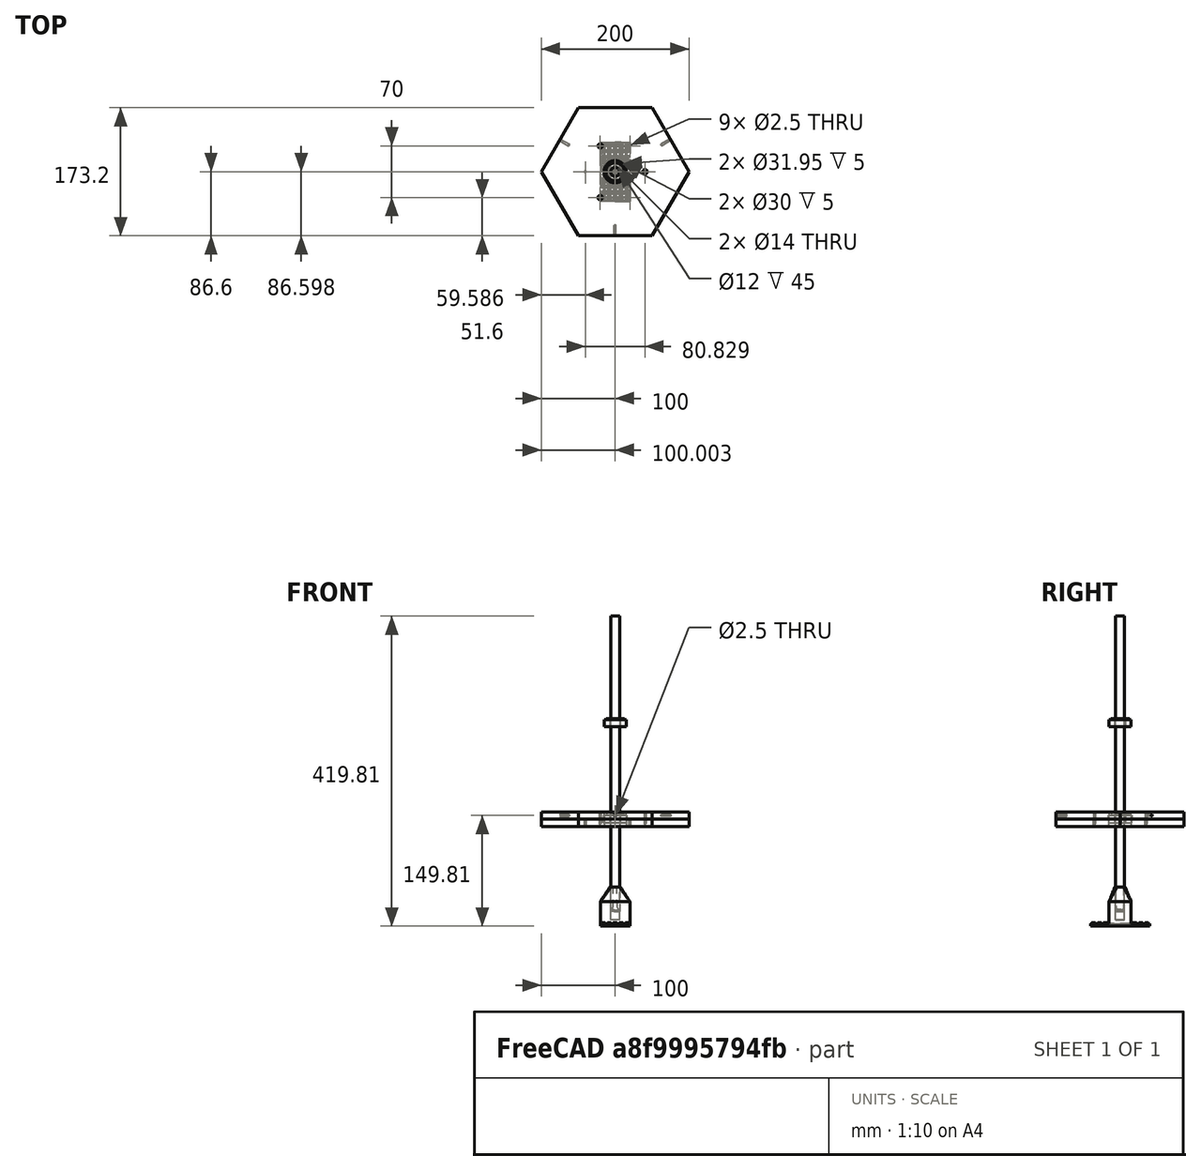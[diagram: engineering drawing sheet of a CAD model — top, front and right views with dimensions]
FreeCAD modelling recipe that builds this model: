
FCSTD DOCUMENT  (FreeCAD 0.20R29177 +426 (Git))
Label: assembly4
License: All rights reserved
LicenseURL: http://en.wikipedia.org/wiki/All_rights_reserved
objects: App::Link×35, Part::Feature×10, App::DocumentObjectGroup×5, App::Part×2, PartDesign::CoordinateSystem×1, App::FeaturePython×1, Part::MultiCommon×1
note: 12 computed .brp shape members not serialized (recipe doc carries the construction recipe); baked Part::Feature solids carry a one-line shape summary decoded from their .brp
EXTERNAL_REF file=lowershaftHolder.FCStd obj=LCS_1
EXTERNAL_REF file=lowershaftHolder.FCStd obj=Body
EXTERNAL_REF file=Main_Rod.FCStd obj=LCS_1
EXTERNAL_REF file=Main_Rod.FCStd obj=Body007
EXTERNAL_REF file=BearingRotator.FCStd obj=RotatorPosition
EXTERNAL_REF file=Main_Rod.FCStd obj=LCS_mid
EXTERNAL_REF file=BearingRotator.FCStd obj=Body
EXTERNAL_REF file=BearingRotator.FCStd obj=RotatorLCS
EXTERNAL_REF file=6201ZZ002_Bearing.FCStd obj=LCS_1
EXTERNAL_REF file=6201ZZ002_Bearing.FCStd obj=Body
EXTERNAL_REF file=Main_Rod.FCStd obj=LCS_mid_upper
EXTERNAL_REF file=mid_hexagon_cmmon_w_side_holes.FCStd obj=LCS_1
EXTERNAL_REF file=mid_hexagon_cmmon_w_side_holes.FCStd obj=Body019
EXTERNAL_REF file=6201ZZ002_Bearing.FCStd obj=bottom_LCS
EXTERNAL_REF file=mid_hexagon_cmmon.FCStd obj=LCS_1
EXTERNAL_REF file=mid_hexagon_cmmon.FCStd obj=Body002
EXTERNAL_REF file=classifier_middle_verPartial3.FCStd obj=LCS_1
EXTERNAL_REF file=mid_hexagon_cmmon_w_side_holes.FCStd obj=LCS_2
EXTERNAL_REF file=classifier_middle_verPartial3.FCStd obj=Body
EXTERNAL_REF file=mid_hexagon_cmmon_w_side_holes.FCStd obj=LCS_3
EXTERNAL_REF file=mid_hexagon_cmmon_w_side_holes.FCStd obj=LCS_4
EXTERNAL_REF file=classifier_middle_verPartial3.FCStd obj=LCS_3
EXTERNAL_REF file=classifier_part.FCStd obj=LCS_1
EXTERNAL_REF file=classifier_part.FCStd obj=Body
EXTERNAL_REF file=classifier_middle_verPartial3.FCStd obj=LCS_2
EXTERNAL_REF file=ImageRecogBox.FCStd obj=LCS_forRod
EXTERNAL_REF file=Main_Rod.FCStd obj=LCS_ImageRecogBox
EXTERNAL_REF file=ImageRecogBox.FCStd obj=Body
EXTERNAL_REF file=ImageRecogBox.FCStd obj=LCS_1
EXTERNAL_REF file=MG90S_servo_refined.FCStd obj=LCS_1
EXTERNAL_REF file=MG90S_servo_refined.FCStd obj=Body
EXTERNAL_REF file=ImageRecogBox.FCStd obj=LCS_cam
EXTERNAL_REF file=esp32camMountRefined.FCStd obj=LCS_1
EXTERNAL_REF file=esp32camMountRefined.FCStd obj=Body
EXTERNAL_REF file=MG90S_servo_refined.FCStd obj=LCS_2
EXTERNAL_REF file=PortalRotatorSketch.FCStd obj=LCS_Origin
EXTERNAL_REF file=PortalRotatorSketch.FCStd obj=PortalRotatorBody
EXTERNAL_REF file=PortalRotatorSketch.FCStd obj=LCSRotator
EXTERNAL_REF file=refinedHorn.FCStd obj=LCS_1
EXTERNAL_REF file=refinedHorn.FCStd obj=Body
EXTERNAL_REF file=hornHexagonModified.FCStd obj=hexagonPlacement
EXTERNAL_REF file=refinedHorn.FCStd obj=hexagonPlacement_LCS
EXTERNAL_REF file=hornHexagonModified.FCStd obj=Body
EXTERNAL_REF file=gear66.FCStd obj=LCS_1
EXTERNAL_REF file=mid_hexagon_cmmon.FCStd obj=LCS_bottom
EXTERNAL_REF file=gear66.FCStd obj=Body003
EXTERNAL_REF file=belt.FCStd obj=LCS_gear66
EXTERNAL_REF file=gear66.FCStd obj=LCS_belt
EXTERNAL_REF file=belt.FCStd obj=Body
EXTERNAL_REF file=belt.FCStd obj=LCS_gear60
EXTERNAL_REF file=gear60_upper.FCStd obj=LCS_belt
EXTERNAL_REF file=gear60_upper.FCStd obj=Body006
EXTERNAL_REF file=gear60_lower.FCStd obj=LCS_1
EXTERNAL_REF file=gear60_upper.FCStd obj=LCS_for_gear60lower
EXTERNAL_REF file=gear60_lower.FCStd obj=Body004
EXTERNAL_REF file=gear60_lower.FCStd obj=LCS_Belt
EXTERNAL_REF file=smallerBelt.FCStd obj=LCS_gear60
EXTERNAL_REF file=smallerBelt.FCStd obj=Body
EXTERNAL_REF file=gear20.FCStd obj=LCS_belt
EXTERNAL_REF file=smallerBelt.FCStd obj=LCS_gear20
EXTERNAL_REF file=gear20.FCStd obj=Body005
EXTERNAL_REF file=17HS4401S_stepper_motor.FCStd obj=LCS_shaft
EXTERNAL_REF file=gear20.FCStd obj=LCS_shaftStepper
EXTERNAL_REF file=17HS4401S_stepper_motor.FCStd obj=Part
EXTERNAL_REF file=17HS4401S_stepper_motor.FCStd obj=LCS_forStand
EXTERNAL_REF file=stepperMotorStand.FCStd obj=LCS_forStepper
EXTERNAL_REF file=stepperMotorStand.FCStd obj=Body
EXTERNAL_REF file=FallAnim.FCStd obj=LCS_Origin
EXTERNAL_REF file=ImageRecogBox.FCStd obj=LCS_fall
EXTERNAL_REF file=FallAnim.FCStd obj=fallSketchBody
EXTERNAL_REF file=FallAnim.FCStd obj=LCS_fallhandler
EXTERNAL_REF file=banana.FCStd obj=LCS_1
EXTERNAL_REF file=banana.FCStd obj=Body

FEATURE [App::DocumentObjectGroup] Parts
FEATURE [PartDesign::CoordinateSystem] LCS_Origin
  AttacherType = Attacher::AttachEngine3D
  MapMode = 2
  Support = -> [X_Axis]
FEATURE [App::DocumentObjectGroup] Constraints
FEATURE [App::FeaturePython] Variables  # WARN: FeaturePython — macro-defined, semantics opaque (R4)
  BearingRotatorVar = -120
  FallHandlerVar = 900
  PortalRotatorDeg = -70
  Type = App::PropertyContainer
FEATURE [App::DocumentObjectGroup] Configurations
FEATURE [App::Link] Body
  AttachedBy = #LCS_1
  AttachedTo = Parent Assembly#LCS_Origin
  AttachmentOffset = pos=(0,0,0) rot=(0.57735,0.57735,0.57735;2.0944rad)
  LinkPlacement = pos=(18.0427,39.9807,-19.8007) rot=(0.109739,0.239494,-0.964676;0.001284rad)
  LinkedObject = -> <external lowershaftHolder.FCStd>#Body
  Placement = pos=(18.0427,39.9807,-19.8007) rot=(0.109739,0.239494,-0.964676;0.001284rad)
  SolverId = Asm4EE
  expr: Placement = LCS_Origin.Placement * AttachmentOffset * lowershaftHolder#LCS_1.Placement ^ -1
FEATURE [App::Link] Rod
  AttachedBy = #LCS_1
  AttachedTo = Parent Assembly#LCS_Origin
  LinkPlacement = pos=(-9e-16,4e-16,400) rot=(0,0,1;0rad)
  LinkedObject = -> <external Main_Rod.FCStd>#Body007
  Placement = pos=(-9e-16,4e-16,400) rot=(0,0,1;0rad)
  SolverId = Asm4EE
  expr: Placement = LCS_Origin.Placement * AttachmentOffset * Main_Rod#LCS_1.Placement ^ -1
FEATURE [App::Link] RotatorBody
  AttachedBy = #RotatorPosition
  AttachedTo = Rod#LCS_mid
  LinkPlacement = pos=(2.7e-15,-1e-15,130) rot=(0,0,1;0rad)
  LinkedObject = -> <external BearingRotator.FCStd>#Body
  Placement = pos=(2.7e-15,-1e-15,130) rot=(0,0,1;0rad)
  SolverId = Asm4EE
  expr: Placement = Rod.Placement * Main_Rod#LCS_mid.Placement * AttachmentOffset * BearingRotator#RotatorPosition.Placement ^ -1
FEATURE [App::Link] Fake_bearing
  AttachedBy = #LCS_1
  AttachedTo = RotatorBody#RotatorLCS
  AttachmentOffset = pos=(0,0,0) rot=(1,0,0;4.71239rad)
  LinkPlacement = pos=(-3.4e-15,1.7e-15,120) rot=(0,0,-1;3.66519rad)
  LinkedObject = -> <external 6201ZZ002_Bearing.FCStd>#Body
  Placement = pos=(-3.4e-15,1.7e-15,120) rot=(0,0,-1;3.66519rad)
  SolverId = Asm4EE
  expr: Placement = RotatorBody.Placement * BearingRotator#RotatorLCS.Placement * AttachmentOffset * _201ZZ002_Bearing#LCS_1.Placement ^ -1
FEATURE [App::Link] RotatorBody001
  AttachedBy = #RotatorPosition
  AttachedTo = Rod#LCS_mid_upper
  LinkPlacement = pos=(2.7e-15,-1e-15,260) rot=(0,0,1;0rad)
  LinkedObject = -> <external BearingRotator.FCStd>#Body
  Placement = pos=(2.7e-15,-1e-15,260) rot=(0,0,1;0rad)
  SolverId = Asm4EE
  expr: Placement = Rod.Placement * Main_Rod#LCS_mid_upper.Placement * AttachmentOffset * BearingRotator#RotatorPosition.Placement ^ -1
FEATURE [App::Link] Fake_bearing001
  AttachedBy = #LCS_1
  AttachedTo = RotatorBody001#RotatorLCS
  AttachmentOffset = pos=(0,0,0) rot=(1,0,0;4.71239rad)
  LinkPlacement = pos=(-3.4e-15,1.7e-15,250) rot=(0,0,-1;3.66519rad)
  LinkedObject = -> <external 6201ZZ002_Bearing.FCStd>#Body
  Placement = pos=(-3.4e-15,1.7e-15,250) rot=(0,0,-1;3.66519rad)
  SolverId = Asm4EE
  expr: Placement = RotatorBody001.Placement * BearingRotator#RotatorLCS.Placement * AttachmentOffset * _201ZZ002_Bearing#LCS_1.Placement ^ -1
FEATURE [App::Link] Rod001
  AttachedBy = #LCS_1
  AttachedTo = Fake_bearing#LCS_1
  AttachmentOffset = pos=(0,0,0) rot=(1,0,0;1.5708rad)
  LinkPlacement = pos=(2.9e-15,-1.4e-15,125) rot=(0,0,-1;3.66519rad)
  LinkedObject = -> <external mid_hexagon_cmmon_w_side_holes.FCStd>#Body019
  Placement = pos=(2.9e-15,-1.4e-15,125) rot=(0,0,-1;3.66519rad)
  SolverId = Asm4EE
  expr: Placement = Fake_bearing.Placement * _201ZZ002_Bearing#LCS_1.Placement * AttachmentOffset * mid_hexagon_cmmon_w_side_holes#LCS_1.Placement ^ -1
FEATURE [App::Link] mid_hexagon
  AttachedBy = #LCS_1
  AttachedTo = Fake_bearing#bottom_LCS
  AttachmentOffset = pos=(0,0,0) rot=(1,0,0;4.71239rad)
  LinkPlacement = pos=(-3.7e-15,1.5e-15,125) rot=(-0.258819,-0.965926,0;3.14159rad)
  LinkedObject = -> <external mid_hexagon_cmmon.FCStd>#Body002
  Placement = pos=(-3.7e-15,1.5e-15,125) rot=(-0.258819,-0.965926,0;3.14159rad)
  SolverId = Asm4EE
  expr: Placement = Fake_bearing.Placement * _201ZZ002_Bearing#bottom_LCS.Placement * AttachmentOffset * mid_hexagon_cmmon#LCS_1.Placement ^ -1
FEATURE [App::Link] mid_hexagon_w_holes
  AttachedBy = #LCS_1
  AttachedTo = Fake_bearing001#LCS_1
  AttachmentOffset = pos=(0,0,0) rot=(1,0,0;1.5708rad)
  LinkPlacement = pos=(2.9e-15,-1.4e-15,255) rot=(0,0,-1;3.66519rad)
  LinkedObject = -> <external mid_hexagon_cmmon_w_side_holes.FCStd>#Body019
  Placement = pos=(2.9e-15,-1.4e-15,255) rot=(0,0,-1;3.66519rad)
  SolverId = Asm4EE
  expr: Placement = Fake_bearing001.Placement * _201ZZ002_Bearing#LCS_1.Placement * AttachmentOffset * mid_hexagon_cmmon_w_side_holes#LCS_1.Placement ^ -1
FEATURE [App::Link] mid_hexagon001
  AttachedBy = #LCS_1
  AttachedTo = Fake_bearing001#bottom_LCS
  AttachmentOffset = pos=(0,0,0) rot=(1,0,0;4.71239rad)
  LinkPlacement = pos=(-3.7e-15,1.5e-15,255) rot=(-0.258819,-0.965926,0;3.14159rad)
  LinkedObject = -> <external mid_hexagon_cmmon.FCStd>#Body002
  Placement = pos=(-3.7e-15,1.5e-15,255) rot=(-0.258819,-0.965926,0;3.14159rad)
  SolverId = Asm4EE
  expr: Placement = Fake_bearing001.Placement * _201ZZ002_Bearing#bottom_LCS.Placement * AttachmentOffset * mid_hexagon_cmmon#LCS_1.Placement ^ -1
FEATURE [Part::Feature] Body001
  Placement = pos=(18.0427,39.9807,-19.8007) rot=(0.109739,0.239494,-0.964676;0.001284rad)
  shape: bbox 40.09 x 80.05 x 53.21 mm, 12357 faces (baked)
FEATURE [Part::Feature] Rod002
  Placement = pos=(-1e-15,0,400) rot=(0,0,1;0rad)
  shape: bbox 25 x 25 x 400 mm, 11 faces (baked)
FEATURE [Part::Feature] Body002
  Placement = pos=(18.0427,39.9807,-19.8007) rot=(0.109739,0.239494,-0.964676;0.001284rad)
  shape: bbox 40.09 x 80.05 x 53.21 mm, 12357 faces (baked)
FEATURE [Part::Feature] Rod003
  Placement = pos=(-1e-15,0,400) rot=(0,0,1;0rad)
  shape: bbox 25 x 25 x 400 mm, 11 faces (baked)
FEATURE [Part::MultiCommon] Common  label="Common 1 - 1 - Body002 - Rod003"
  Shapes = -> [Body002,Rod003]
FEATURE [App::DocumentObjectGroup] Intersections
  Group = -> [Common]
FEATURE [Part::Feature] RotatorBody002
FEATURE [Part::Feature] Fake_bearing002
  Placement = pos=(2e-15,-8e-15,120) rot=(0,0,-1;1.5708rad)
  shape: bbox 30 x 30 x 10 mm, 4 faces (baked)
FEATURE [Part::Feature] RotatorBody001001
FEATURE [Part::Feature] Fake_bearing001001
  Placement = pos=(2e-15,-8e-15,250) rot=(0,0,-1;1.5708rad)
  shape: bbox 30 x 30 x 10 mm, 4 faces (baked)
FEATURE [Part::Feature] Rod001001
  Placement = pos=(3e-15,-1e-15,125) rot=(0,0,-1;1.5708rad)
  shape: bbox 200 x 173.2 x 10 mm, 23 faces (baked)
FEATURE [Part::Feature] mid_hexagon002
  Placement = pos=(3e-15,-8e-15,125) rot=(0.707107,-0.707107,0;3.14159rad)
  shape: bbox 200 x 173.2 x 10 mm, 20 faces (baked)
FEATURE [App::Part] Assembly_copy
  Group = -> [Body001,Rod002,RotatorBody002,Fake_bearing002,RotatorBody001001,Fake_bearing001001,Rod001001,mid_hexagon002]
  Origin = -> Origin001
FEATURE [App::DocumentObjectGroup] Interferences
  Group = -> [Assembly_copy,Intersections]
FEATURE [App::Link] MiddlePartialBody
  AttachedBy = #LCS_1
  AttachedTo = mid_hexagon_w_holes#LCS_2
  LinkPlacement = pos=(-25,43.3013,115) rot=(0,0,-1;5.75959rad)
  LinkedObject = -> <external classifier_middle_verPartial3.FCStd>#Body
  Placement = pos=(-25,43.3013,115) rot=(0,0,-1;5.75959rad)
  SolverId = Asm4EE
  expr: Placement = mid_hexagon_w_holes.Placement * mid_hexagon_cmmon_w_side_holes#LCS_2.Placement * AttachmentOffset * classifier_middle_verPartial3#LCS_1.Placement ^ -1
FEATURE [App::Link] MiddlePartialBody001
  AttachedBy = #LCS_1
  AttachedTo = mid_hexagon_w_holes#LCS_3
  LinkPlacement = pos=(-25,-43.3013,115) rot=(0,0,-1;3.66519rad)
  LinkedObject = -> <external classifier_middle_verPartial3.FCStd>#Body
  Placement = pos=(-25,-43.3013,115) rot=(0,0,-1;3.66519rad)
  SolverId = Asm4EE
  expr: Placement = mid_hexagon_w_holes.Placement * mid_hexagon_cmmon_w_side_holes#LCS_3.Placement * AttachmentOffset * classifier_middle_verPartial3#LCS_1.Placement ^ -1
FEATURE [App::Link] MiddlePartialBody002
  AttachedBy = #LCS_1
  AttachedTo = mid_hexagon_w_holes#LCS_4
  LinkPlacement = pos=(50,2e-16,115) rot=(0,0,1;4.71239rad)
  LinkedObject = -> <external classifier_middle_verPartial3.FCStd>#Body
  Placement = pos=(50,2e-16,115) rot=(0,0,1;4.71239rad)
  SolverId = Asm4EE
  expr: Placement = mid_hexagon_w_holes.Placement * mid_hexagon_cmmon_w_side_holes#LCS_4.Placement * AttachmentOffset * classifier_middle_verPartial3#LCS_1.Placement ^ -1
FEATURE [App::Link] ClassifierPartBody
  AttachedBy = #LCS_1
  AttachedTo = MiddlePartialBody002#LCS_3
  LinkPlacement = pos=(154.11,87.477,120) rot=(0,0,1;3.6566rad)
  LinkedObject = -> <external classifier_part.FCStd>#Body
  Placement = pos=(154.11,87.477,120) rot=(0,0,1;3.6566rad)
  SolverId = Asm4EE
  expr: Placement = MiddlePartialBody002.Placement * classifier_middle_verPartial3#LCS_3.Placement * AttachmentOffset * classifier_part#LCS_1.Placement ^ -1
FEATURE [App::Link] ClassifierPartBody001
  AttachedBy = #LCS_1
  AttachedTo = MiddlePartialBody001#LCS_3
  LinkPlacement = pos=(-1.29784,-177.202,120) rot=(0,0,-1;4.72098rad)
  LinkedObject = -> <external classifier_part.FCStd>#Body
  Placement = pos=(-1.29784,-177.202,120) rot=(0,0,-1;4.72098rad)
  SolverId = Asm4EE
  expr: Placement = MiddlePartialBody001.Placement * classifier_middle_verPartial3#LCS_3.Placement * AttachmentOffset * classifier_part#LCS_1.Placement ^ -1
FEATURE [App::Link] ClassifierPartBody002
  AttachedBy = #LCS_1
  AttachedTo = MiddlePartialBody#LCS_3
  LinkPlacement = pos=(-152.813,89.725,120) rot=(0,0,1;5.75099rad)
  LinkedObject = -> <external classifier_part.FCStd>#Body
  Placement = pos=(-152.813,89.725,120) rot=(0,0,1;5.75099rad)
  SolverId = Asm4EE
  expr: Placement = MiddlePartialBody.Placement * classifier_middle_verPartial3#LCS_3.Placement * AttachmentOffset * classifier_part#LCS_1.Placement ^ -1
FEATURE [App::Link] ClassifierPartBody003
  AttachedBy = #LCS_1
  AttachedTo = MiddlePartialBody001#LCS_2
  LinkPlacement = pos=(-153.088,-89.7186,120) rot=(0,0,-1;5.75959rad)
  LinkedObject = -> <external classifier_part.FCStd>#Body
  Placement = pos=(-153.088,-89.7186,120) rot=(0,0,-1;5.75959rad)
  SolverId = Asm4EE
  expr: Placement = MiddlePartialBody001.Placement * classifier_middle_verPartial3#LCS_2.Placement * AttachmentOffset * classifier_part#LCS_1.Placement ^ -1
FEATURE [App::Link] ClassifierPartBody004
  AttachedBy = #LCS_1
  AttachedTo = MiddlePartialBody002#LCS_2
  LinkPlacement = pos=(154.242,-87.7186,120) rot=(0,0,1;2.61799rad)
  LinkedObject = -> <external classifier_part.FCStd>#Body
  Placement = pos=(154.242,-87.7186,120) rot=(0,0,1;2.61799rad)
  SolverId = Asm4EE
  expr: Placement = MiddlePartialBody002.Placement * classifier_middle_verPartial3#LCS_2.Placement * AttachmentOffset * classifier_part#LCS_1.Placement ^ -1
FEATURE [App::Link] ClassifierPartBody005
  AttachedBy = #LCS_1
  AttachedTo = MiddlePartialBody#LCS_2
  LinkPlacement = pos=(-1.1547,177.437,120) rot=(0,0,1;4.71239rad)
  LinkedObject = -> <external classifier_part.FCStd>#Body
  Placement = pos=(-1.1547,177.437,120) rot=(0,0,1;4.71239rad)
  SolverId = Asm4EE
  expr: Placement = MiddlePartialBody.Placement * classifier_middle_verPartial3#LCS_2.Placement * AttachmentOffset * classifier_part#LCS_1.Placement ^ -1
FEATURE [App::Link] ImageRecogBox_body  label="ImageRecogBox-body"
  AttachedBy = #LCS_forRod
  AttachedTo = Rod#LCS_ImageRecogBox
  LinkPlacement = pos=(-0.00816561,-167.469,384) rot=(0,0,-1;0.523648rad)
  LinkedObject = -> <external ImageRecogBox.FCStd>#Body
  Placement = pos=(-0.00816561,-167.469,384) rot=(0,0,-1;0.523648rad)
  SolverId = Asm4EE
  expr: Placement = Rod.Placement * Main_Rod#LCS_ImageRecogBox.Placement * AttachmentOffset * ImageRecogBox#LCS_forRod.Placement ^ -1
FEATURE [App::Link] Body003
  AttachedBy = #LCS_1
  AttachedTo = ImageRecogBox_body#LCS_1
  AttachmentOffset = pos=(0,0,0) rot=(0.57735,0.57735,0.57735;2.0944rad)
  LinkPlacement = pos=(-1546.53,182.702,-393.809) rot=(0.774614,0.447198,0.447198;1.82346rad)
  LinkedObject = -> <external MG90S_servo_refined.FCStd>#Body
  Placement = pos=(-1546.53,182.702,-393.809) rot=(0.774614,0.447198,0.447198;1.82346rad)
  SolverId = Asm4EE
  expr: Placement = ImageRecogBox_body.Placement * ImageRecogBox#LCS_1.Placement * AttachmentOffset * MG90S_servo_refined#LCS_1.Placement ^ -1
FEATURE [App::Link] mountBody
  AttachedBy = #LCS_1
  AttachedTo = ImageRecogBox_body#LCS_cam
  LinkPlacement = pos=(3.98719,-262.811,482.589) rot=(-2e-06,-0.087156,-0.996195;3.14164rad)
  LinkedObject = -> <external esp32camMountRefined.FCStd>#Body
  Placement = pos=(3.98719,-262.811,482.589) rot=(-2e-06,-0.087156,-0.996195;3.14164rad)
  SolverId = Asm4EE
  expr: Placement = ImageRecogBox_body.Placement * ImageRecogBox#LCS_cam.Placement * AttachmentOffset * esp32camMountRefined#LCS_1.Placement ^ -1
FEATURE [App::Link] PortalRotatorBody
  AttachedBy = #LCS_Origin
  AttachedTo = Body003#LCS_2
  LinkPlacement = pos=(58.8831,-230.669,373.4) rot=(0,0,1;1.04715rad)
  LinkedObject = -> <external PortalRotatorSketch.FCStd>#PortalRotatorBody
  Placement = pos=(58.8831,-230.669,373.4) rot=(0,0,1;1.04715rad)
  SolverId = Asm4EE
  expr: Placement = Body003.Placement * MG90S_servo_refined#LCS_2.Placement * AttachmentOffset * PortalRotatorSketch#LCS_Origin.Placement ^ -1
FEATURE [App::Link] HornBody
  AttachedBy = #LCS_1
  AttachedTo = PortalRotatorBody#LCSRotator
  AttachmentOffset = pos=(0,0,0) rot=(1,0,0;4.71239rad)
  LinkPlacement = pos=(-154.381,-489.726,375.091) rot=(-0.893584,0.448895,0;3.14159rad)
  LinkedObject = -> <external refinedHorn.FCStd>#Body
  Placement = pos=(-154.381,-489.726,375.091) rot=(-0.893584,0.448895,0;3.14159rad)
  SolverId = Asm4EE
  expr: Placement = PortalRotatorBody.Placement * PortalRotatorSketch#LCSRotator.Placement * AttachmentOffset * refinedHorn#LCS_1.Placement ^ -1
FEATURE [App::Link] hornHexagonBody
  AttachedBy = #hexagonPlacement
  AttachedTo = HornBody#hexagonPlacement_LCS
  LinkPlacement = pos=(29.3352,-148.735,372.089) rot=(0,0,1;5.33754rad)
  LinkedObject = -> <external hornHexagonModified.FCStd>#Body
  Placement = pos=(29.3352,-148.735,372.089) rot=(0,0,1;5.33754rad)
  SolverId = Asm4EE
  expr: Placement = HornBody.Placement * refinedHorn#hexagonPlacement_LCS.Placement * AttachmentOffset * hornHexagonModified#hexagonPlacement.Placement ^ -1
FEATURE [App::Link] gear66Body
  AttachedBy = #LCS_1
  AttachedTo = mid_hexagon#LCS_bottom
  LinkPlacement = pos=(-5.9e-15,1.6e-14,88.5) rot=(0,0,1;2.61799rad)
  LinkedObject = -> <external gear66.FCStd>#Body003
  Placement = pos=(-5.9e-15,1.6e-14,88.5) rot=(0,0,1;2.61799rad)
  SolverId = Asm4EE
  expr: Placement = mid_hexagon.Placement * mid_hexagon_cmmon#LCS_bottom.Placement * AttachmentOffset * gear66#LCS_1.Placement ^ -1
FEATURE [App::Link] belt_Body
  AttachedBy = #LCS_gear66
  AttachedTo = gear66Body#LCS_belt
  AttachmentOffset = pos=(0,0,0) rot=(1,0,0;1.5708rad)
  LinkPlacement = pos=(15.0572,27.5548,87.5) rot=(0,0,1;1.07069rad)
  LinkedObject = -> <external belt.FCStd>#Body
  Placement = pos=(15.0572,27.5548,87.5) rot=(0,0,1;1.07069rad)
  SolverId = Asm4EE
  expr: Placement = gear66Body.Placement * gear66#LCS_belt.Placement * AttachmentOffset * belt#LCS_gear66.Placement ^ -1
FEATURE [App::Link] gear60_upperBody
  AttachedBy = #LCS_belt
  AttachedTo = belt_Body#LCS_gear60
  AttachmentOffset = pos=(0,0,0) rot=(1,0,0;4.71239rad)
  LinkPlacement = pos=(40.8358,74.7297,87.5) rot=(0,0,1;5.80656rad)
  LinkedObject = -> <external gear60_upper.FCStd>#Body006
  Placement = pos=(40.8358,74.7297,87.5) rot=(0,0,1;5.80656rad)
  SolverId = Asm4EE
  expr: Placement = belt_Body.Placement * belt#LCS_gear60.Placement * AttachmentOffset * gear60_upper#LCS_belt.Placement ^ -1
FEATURE [App::Link] gear60_lower_body
  AttachedBy = #LCS_1
  AttachedTo = gear60_upperBody#LCS_for_gear60lower
  LinkPlacement = pos=(40.8358,74.7297,76) rot=(0,0,1;5.80656rad)
  LinkedObject = -> <external gear60_lower.FCStd>#Body004
  Placement = pos=(40.8358,74.7297,76) rot=(0,0,1;5.80656rad)
  SolverId = Asm4EE
  expr: Placement = gear60_upperBody.Placement * gear60_upper#LCS_for_gear60lower.Placement * AttachmentOffset * gear60_lower#LCS_1.Placement ^ -1
FEATURE [App::Link] smallerBelt_Body
  AttachedBy = #LCS_gear60
  AttachedTo = gear60_lower_body#LCS_Belt
  LinkPlacement = pos=(-5.71516,89.0849,76) rot=(0,0,1;2.84247rad)
  LinkedObject = -> <external smallerBelt.FCStd>#Body
  Placement = pos=(-5.71516,89.0849,76) rot=(0,0,1;2.84247rad)
  SolverId = Asm4EE
  expr: Placement = gear60_lower_body.Placement * gear60_lower#LCS_Belt.Placement * AttachmentOffset * smallerBelt#LCS_gear60.Placement ^ -1
FEATURE [App::Link] gear20_body
  AttachedBy = #LCS_belt
  AttachedTo = smallerBelt_Body#LCS_gear20
  LinkPlacement = pos=(-32.2262,97.2603,76) rot=(0,0,1;3.01997rad)
  LinkedObject = -> <external gear20.FCStd>#Body005
  Placement = pos=(-32.2262,97.2603,76) rot=(0,0,1;3.01997rad)
  SolverId = Asm4EE
  expr: Placement = smallerBelt_Body.Placement * smallerBelt#LCS_gear20.Placement * AttachmentOffset * gear20#LCS_belt.Placement ^ -1
FEATURE [App::Link] _7HS4401S_Stepper_Motor  label="17HS4401S Stepper Motor"
  AttachedBy = #LCS_shaft
  AttachedTo = gear20_body#LCS_shaftStepper
  LinkPlacement = pos=(-68.0048,-76.3424,26.5) rot=(0,0,1;1.05307rad)
  LinkedObject = -> <external 17HS4401S_stepper_motor.FCStd>#Part
  Placement = pos=(-68.0048,-76.3424,26.5) rot=(0,0,1;1.05307rad)
  SolverId = Asm4EE
  expr: Placement = gear20_body.Placement * gear20#LCS_shaftStepper.Placement * AttachmentOffset * _7HS4401S_stepper_motor#LCS_shaft.Placement ^ -1
FEATURE [App::Link] stand_Body
  AttachedBy = #LCS_forStepper
  AttachedTo = _7HS4401S_Stepper_Motor#LCS_forStand
  AttachmentOffset = pos=(0,0,0) rot=(0,0,1;1.5708rad)
  LinkPlacement = pos=(-36.9523,-21.8204,-19.8) rot=(0,0,1;3.14747rad)
  LinkedObject = -> <external stepperMotorStand.FCStd>#Body
  Placement = pos=(-36.9523,-21.8204,-19.8) rot=(0,0,1;3.14747rad)
  SolverId = Asm4EE
  expr: Placement = _7HS4401S_Stepper_Motor.Placement * _7HS4401S_stepper_motor#LCS_forStand.Placement * AttachmentOffset * stepperMotorStand#LCS_forStepper.Placement ^ -1
FEATURE [App::Link] fallSketchBody
  AttachedBy = #LCS_Origin
  AttachedTo = ImageRecogBox_body#LCS_fall
  AttachmentOffset = pos=(0,0,0) rot=(0.57735,-0.57735,-0.57735;4.18879rad)
  LinkPlacement = pos=(-0.00912142,-187.071,984) rot=(0,0,-1;3.14164rad)
  LinkedObject = -> <external FallAnim.FCStd>#fallSketchBody
  Placement = pos=(-0.00912142,-187.071,984) rot=(0,0,-1;3.14164rad)
  SolverId = Asm4EE
  expr: Placement = ImageRecogBox_body.Placement * ImageRecogBox#LCS_fall.Placement * AttachmentOffset * FallAnim#LCS_Origin.Placement ^ -1
FEATURE [App::Link] Banana_Body
  AttachedBy = #LCS_1
  AttachedTo = fallSketchBody#LCS_fallhandler
  LinkPlacement = pos=(-0.00912142,-187.071,84) rot=(0,0,-1;3.14164rad)
  LinkedObject = -> <external banana.FCStd>#Body
  Placement = pos=(-0.00912142,-187.071,84) rot=(0,0,-1;3.14164rad)
  SolverId = Asm4EE
  expr: Placement = fallSketchBody.Placement * FallAnim#LCS_fallhandler.Placement * AttachmentOffset * banana#LCS_1.Placement ^ -1
FEATURE [App::Part] Assembly
  AssemblyType = Part::Link
  Group = -> [LCS_Origin,Constraints,Variables,Configurations,Body,Rod,RotatorBody,Fake_bearing,RotatorBody001,Fake_bearing001,Rod001,mid_hexagon,mid_hexagon_w_holes,mid_hexagon001,MiddlePartialBody,MiddlePartialBody001,MiddlePartialBody002,ClassifierPartBody,ClassifierPartBody001,ClassifierPartBody002,ClassifierPartBody003,ClassifierPartBody004,ClassifierPartBody005,ImageRecogBox_body,Body003,mountBody,+13 more]
  Origin = -> Origin
  Type = Assembly

RESOLVED EXTERNAL PARTS (link-assembly join: the EXTERNAL_REF files above that resolve inside this repo's crawl, each included once):
---- part 17HS4401S_stepper_motor.FCStd = doc fcstd_67801616e878 ----
FCSTD DOCUMENT  (FreeCAD 0.20R29177 +426 (Git))
Label: 17HS4401S_stepper_motor
License: All rights reserved
LicenseURL: http://en.wikipedia.org/wiki/All_rights_reserved
objects: Sketcher::SketchObject×18, PartDesign::Pad×10, PartDesign::Body×7, PartDesign::Pocket×5, PartDesign::Chamfer×4, Part::FeaturePython×4, PartDesign::Fillet×3, PartDesign::Revolution×2, PartDesign::CoordinateSystem×2, PartDesign::LinearPattern×1, App::Part×1
note: 80 computed .brp shape members not serialized (recipe doc carries the construction recipe); baked Part::Feature solids carry a one-line shape summary decoded from their .brp

FEATURE [PartDesign::Body] Body  label="rear end cap"
  Origin = -> Origin
FEATURE [Sketcher::SketchObject] Sketch  label=" rear outline"
  FullyConstrained = true
  MapMode = 5
  Support = -> [XY_Plane]
  sketch-geometry (17):
    g0: ArcOfCircle CenterX=0 CenterY=0 CenterZ=0 NormalX=0 NormalY=0 NormalZ=1 AngleXU=0 Radius=26.8 StartAngle=2.24118 EndAngle=2.47121
    g1: ArcOfCircle CenterX=0 CenterY=0 CenterZ=0 NormalX=0 NormalY=0 NormalZ=1 AngleXU=0 Radius=26.8 StartAngle=5.38277 EndAngle=5.6128
    g2: ArcOfCircle CenterX=0 CenterY=0 CenterZ=0 NormalX=0 NormalY=0 NormalZ=1 AngleXU=0 Radius=26.8 StartAngle=0.670386 EndAngle=0.900411
    g3: ArcOfCircle CenterX=0 CenterY=0 CenterZ=0 NormalX=0 NormalY=0 NormalZ=1 AngleXU=0 Radius=26.8 StartAngle=3.81198 EndAngle=4.042
    g4: LineSegment StartX=-16.6505 StartY=21 StartZ=0 EndX=16.6505 EndY=21 EndZ=0
    g5: LineSegment StartX=21 StartY=16.6505 StartZ=0 EndX=21 EndY=8.3 EndZ=0
    g6: LineSegment StartX=-16.6505 StartY=-21 StartZ=0 EndX=16.6505 EndY=-21 EndZ=0
    g7: LineSegment StartX=-21 StartY=16.6505 StartZ=0 EndX=-21 EndY=-16.6505 EndZ=0
    g8: Circle CenterX=0 CenterY=0 CenterZ=0 NormalX=0 NormalY=0 NormalZ=1 AngleXU=0 Radius=4.5
    g9: Circle CenterX=-15.5 CenterY=15.5 CenterZ=0 NormalX=0 NormalY=0 NormalZ=1 AngleXU=0 Radius=1.5
    g10: Circle CenterX=15.5 CenterY=15.5 CenterZ=0 NormalX=0 NormalY=0 NormalZ=1 AngleXU=0 Radius=1.5
    g11: Circle CenterX=15.5 CenterY=-15.5 CenterZ=0 NormalX=0 NormalY=0 NormalZ=1 AngleXU=0 Radius=1.5
    g12: Circle CenterX=-15.5 CenterY=-15.5 CenterZ=0 NormalX=0 NormalY=0 NormalZ=1 AngleXU=0 Radius=1.5
    g13: LineSegment StartX=21 StartY=8.3 StartZ=0 EndX=25.4 EndY=8.3 EndZ=0
    g14: LineSegment StartX=25.4 StartY=8.3 StartZ=0 EndX=25.4 EndY=-8.3 EndZ=0
    g15: LineSegment StartX=25.4 StartY=-8.3 StartZ=0 EndX=21 EndY=-8.3 EndZ=0
    g16: LineSegment StartX=21 StartY=-8.3 StartZ=0 EndX=21 EndY=-16.6505 EndZ=0
  constraints (50):
    c: Coincident(g0,g-1)
    c: Coincident(g1,g0)
    c: Coincident(g2,g0)
    c: Coincident(g3,g0)
    c: Equal(g0,g1)
    c: Equal(g1,g2)
    c: Equal(g2,g3)
    c: Radius(g0) = 26.8
    c: Coincident(g4,g0)
    c: Coincident(g4,g2)
    c: Horizontal(g4)
    c: Coincident(g5,g2)
    c: Coincident(g16,g1)
    c: Vertical(g5)
    c: Coincident(g6,g3)
    c: Coincident(g6,g1)
    c: Coincident(g7,g0)
    c: Coincident(g7,g3)
    c: Vertical(g7)
    c: Horizontal(g6)
    c: DistanceX(g0,g2) = 42
    c: DistanceY(g1,g2) = 42
    c: DistanceY(g0,g2) = 21
    c: DistanceX(g0,g0) = 21
    c: Coincident(g8,g0)
    c: Diameter(g8) = 9
    c: Vertical(g9,g12)
    c: Vertical(g11,g10)
    c: Horizontal(g9,g10)
    c: Horizontal(g12,g11)
    c: Equal(g9,g10)
    c: Equal(g11,g10)
    c: Equal(g11,g12)
    c: Diameter(g9) = 3
    c: DistanceX(g9,g10) = 31
    c: DistanceY(g11,g10) = 31
    c: DistanceY(g0,g10) = 15.5
    c: DistanceX(g0,g10) = 15.5
    c: Horizontal(g13)
    c: Coincident(g14,g13)
    c: Vertical(g14)
    c: Coincident(g15,g14)
    c: Horizontal(g15)
    c: DistanceY(g14,g14) = 16.6
    c: DistanceY(g0,g13) = 8.3
    c: DistanceX(g13,g13) = 4.4
    c: Coincident(g5,g13)
    c: Coincident(g16,g15)
    c: Vertical(g5,g15)
    c: Vertical(g16)
FEATURE [Sketcher::SketchObject] Sketch001  label="basic outline"
  FullyConstrained = true
  MapMode = 5
  Support = -> [XY_Plane001]
  sketch-geometry (13):
    g0: ArcOfCircle CenterX=0 CenterY=0 CenterZ=0 NormalX=0 NormalY=0 NormalZ=1 AngleXU=0 Radius=26.8 StartAngle=2.24118 EndAngle=2.47121
    g1: ArcOfCircle CenterX=0 CenterY=0 CenterZ=0 NormalX=0 NormalY=0 NormalZ=1 AngleXU=0 Radius=26.8 StartAngle=5.38277 EndAngle=5.6128
    g2: ArcOfCircle CenterX=0 CenterY=0 CenterZ=0 NormalX=0 NormalY=0 NormalZ=1 AngleXU=0 Radius=26.8 StartAngle=0.670386 EndAngle=0.900411
    g3: ArcOfCircle CenterX=0 CenterY=0 CenterZ=0 NormalX=0 NormalY=0 NormalZ=1 AngleXU=0 Radius=26.8 StartAngle=3.81198 EndAngle=4.042
    g4: LineSegment StartX=-16.6505 StartY=21 StartZ=0 EndX=16.6505 EndY=21 EndZ=0
    g5: LineSegment StartX=21 StartY=16.6505 StartZ=0 EndX=21 EndY=-16.6505 EndZ=0
    g6: LineSegment StartX=-16.6505 StartY=-21 StartZ=0 EndX=16.6505 EndY=-21 EndZ=0
    g7: LineSegment StartX=-21 StartY=16.6505 StartZ=0 EndX=-21 EndY=-16.6505 EndZ=0
    g8: Circle CenterX=0 CenterY=0 CenterZ=0 NormalX=0 NormalY=0 NormalZ=1 AngleXU=0 Radius=4.5
    g9: Circle CenterX=-15.5 CenterY=15.5 CenterZ=0 NormalX=0 NormalY=0 NormalZ=1 AngleXU=0 Radius=1.5
    g10: Circle CenterX=15.5 CenterY=15.5 CenterZ=0 NormalX=0 NormalY=0 NormalZ=1 AngleXU=0 Radius=1.5
    g11: Circle CenterX=15.5 CenterY=-15.5 CenterZ=0 NormalX=0 NormalY=0 NormalZ=1 AngleXU=0 Radius=1.5
    g12: Circle CenterX=-15.5 CenterY=-15.5 CenterZ=0 NormalX=0 NormalY=0 NormalZ=1 AngleXU=0 Radius=1.5
  constraints (38):
    c: Coincident(g0,g-1)
    c: Coincident(g1,g0)
    c: Coincident(g2,g0)
    c: Coincident(g3,g0)
    c: Equal(g0,g1)
    c: Equal(g1,g2)
    c: Equal(g2,g3)
    c: Radius(g0) = 26.8
    c: Coincident(g4,g0)
    c: Coincident(g4,g2)
    c: Horizontal(g4)
    c: Coincident(g5,g2)
    c: Coincident(g5,g1)
    c: Vertical(g5)
    c: Coincident(g6,g3)
    c: Coincident(g6,g1)
    c: Coincident(g7,g0)
    c: Coincident(g7,g3)
    c: Vertical(g7)
    c: Horizontal(g6)
    c: DistanceX(g0,g2) = 42
    c: DistanceY(g1,g2) = 42
    c: DistanceY(g0,g2) = 21
    c: DistanceX(g0,g0) = 21
    c: Coincident(g8,g0)
    c: Diameter(g8) = 9
    c: Vertical(g9,g12)
    c: Vertical(g11,g10)
    c: Horizontal(g9,g10)
    c: Horizontal(g12,g11)
    c: Equal(g9,g10)
    c: Equal(g11,g10)
    c: Equal(g11,g12)
    c: Diameter(g9) = 3
    c: DistanceX(g9,g10) = 31
    c: DistanceY(g11,g10) = 31
    c: DistanceY(g0,g10) = 15.5
    c: DistanceX(g0,g10) = 15.5
FEATURE [PartDesign::Pad] Pad
  Direction = (0,0,1)
  Length = 9.4
  Length2 = 10
  Profile = -> Sketch
  ReferenceAxis = -> Sketch [N_Axis]
  Type = 0
FEATURE [Sketcher::SketchObject] Sketch002
  FullyConstrained = true
  MapMode = 5
  Support = -> [XY_Plane]
  sketch-geometry (4):
    g0: Circle CenterX=-15.5 CenterY=15.5 CenterZ=0 NormalX=0 NormalY=0 NormalZ=1 AngleXU=0 Radius=3.2
    g1: Circle CenterX=15.5 CenterY=15.5 CenterZ=0 NormalX=0 NormalY=0 NormalZ=1 AngleXU=0 Radius=3.2
    g2: Circle CenterX=15.5 CenterY=-15.5 CenterZ=0 NormalX=0 NormalY=0 NormalZ=1 AngleXU=0 Radius=3.2
    g3: Circle CenterX=-15.5 CenterY=-15.5 CenterZ=0 NormalX=0 NormalY=0 NormalZ=1 AngleXU=0 Radius=3.2
  constraints (12):
    c: Equal(g0,g1)
    c: Equal(g1,g2)
    c: Equal(g2,g3)
    c: Horizontal(g0,g1)
    c: Horizontal(g3,g2)
    c: Vertical(g1,g2)
    c: Vertical(g0,g3)
    c: Diameter(g0) = 6.4
    c: DistanceY(g2,g1) = 31
    c: DistanceY(g2,g-1) = 15.5
    c: DistanceX(g0,g1) = 31
    c: DistanceX(g-1,g1) = 15.5
FEATURE [PartDesign::Pocket] Pocket  label="screw counterbore"
  BaseFeature = -> Pad
  Direction = (0,0,-1)
  Length = 3
  Length2 = 5
  Profile = -> Sketch002
  ReferenceAxis = -> Sketch002 [N_Axis]
  Reversed = true
  Type = 0
FEATURE [Sketcher::SketchObject] Sketch003
  AttachmentOffset = pos=(0,0,10) rot=(0,0,1;0rad)
  FullyConstrained = true
  MapMode = 5
  Placement = pos=(0,0,10) rot=(0,0,1;0rad)
  Support = -> [XY_Plane]
  sketch-geometry (1):
    g0: Circle CenterX=0 CenterY=0 CenterZ=0 NormalX=0 NormalY=0 NormalZ=1 AngleXU=0 Radius=8
  constraints (2):
    c: Coincident(g0,g-1)
    c: Diameter(g0) = 16
FEATURE [PartDesign::Pocket] Pocket001  label="bearing pocket"
  BaseFeature = -> Pocket
  Direction = (0,0,-1)
  Length = 8
  Length2 = 5
  Profile = -> Sketch003
  ReferenceAxis = -> Sketch003 [N_Axis]
  Type = 0
FEATURE [Sketcher::SketchObject] Sketch004
  AttachmentOffset = pos=(0,0,26) rot=(0,0,1;0rad)
  FullyConstrained = true
  MapMode = 5
  Placement = pos=(26,-5.8e-15,5.8e-15) rot=(0.57735,0.57735,0.57735;2.0944rad)
  Support = -> [YZ_Plane]
  sketch-geometry (4):
    g0: LineSegment StartX=-8.3 StartY=9.4 StartZ=0 EndX=8.3 EndY=9.4 EndZ=0
    g1: LineSegment StartX=8.3 StartY=9.4 StartZ=0 EndX=8.3 EndY=3 EndZ=0
    g2: LineSegment StartX=8.3 StartY=3 StartZ=0 EndX=-8.3 EndY=3 EndZ=0
    g3: LineSegment StartX=-8.3 StartY=3 StartZ=0 EndX=-8.3 EndY=9.4 EndZ=0
  constraints (12):
    c: Coincident(g0,g1)
    c: Coincident(g1,g2)
    c: Coincident(g2,g3)
    c: Coincident(g3,g0)
    c: Horizontal(g0)
    c: Horizontal(g2)
    c: Vertical(g1)
    c: Vertical(g3)
    c: DistanceX(g0,g0) = 16.6
    c: DistanceX(g-1,g0) = 8.3
    c: DistanceY(g-1,g0) = 9.4
    c: DistanceY(g-1,g1) = 3
FEATURE [PartDesign::Pocket] Pocket002
  BaseFeature = -> Pocket
  Direction = (-1,2e-16,-3e-16)
  Length = 10
  Length2 = 5
  Profile = -> Sketch004
  ReferenceAxis = -> Sketch004 [N_Axis]
  Type = 0
FEATURE [Sketcher::SketchObject] Sketch005
  FullyConstrained = true
  MapMode = 5
  Placement = pos=(0,0,0) rot=(1,0,0;1.5708rad)
  Support = -> [XZ_Plane002]
  sketch-geometry (12):
    g0: LineSegment StartX=2.5 StartY=2.55 StartZ=0 EndX=8 EndY=2.55 EndZ=0
    g1: LineSegment StartX=8 StartY=2.55 StartZ=0 EndX=8 EndY=-2.45 EndZ=0
    g2: LineSegment StartX=8 StartY=-2.45 StartZ=0 EndX=6.5 EndY=-2.45 EndZ=0
    g3: LineSegment StartX=2.5 StartY=-2.5 StartZ=0 EndX=2.5 EndY=2.55 EndZ=0
    g4: LineSegment StartX=4.2 StartY=-2.45 StartZ=0 EndX=4.1 EndY=-1.95 EndZ=0
    g5: LineSegment StartX=4.1 StartY=-1.95 StartZ=0 EndX=4 EndY=-2.5 EndZ=0
    g6: LineSegment StartX=5.2 StartY=-2.45 StartZ=0 EndX=6.13734 EndY=-1.97682 EndZ=0
    g7: LineSegment StartX=6.5 StartY=-2.2 StartZ=0 EndX=6.5 EndY=-2.45 EndZ=0
    g8: LineSegment StartX=4 StartY=-2.5 StartZ=0 EndX=2.5 EndY=-2.5 EndZ=0
    g9: LineSegment StartX=5.2 StartY=-2.45 StartZ=0 EndX=4.2 EndY=-2.45 EndZ=0
    g10: ArcOfCircle CenterX=6.25 CenterY=-2.2 CenterZ=0 NormalX=0 NormalY=0 NormalZ=1 AngleXU=0 Radius=0.25 StartAngle=2.03828 EndAngle=6.28319
    g11: LineSegment StartX=6.5 StartY=-2.45 StartZ=0 EndX=5.2 EndY=-2.45 EndZ=0
  constraints (34):
    c: Coincident(g0,g1)
    c: Coincident(g1,g2)
    c: Coincident(g8,g3)
    c: Coincident(g3,g0)
    c: Horizontal(g0)
    c: Horizontal(g2)
    c: Vertical(g1)
    c: Vertical(g3)
    c: Coincident(g5,g4)
    c: DistanceX(g-1,g8) = 2.5
    c: DistanceX(g-1,g1) = 8
    c: DistanceY(g1,g1) = 5
    c: DistanceY(g8,g-1) = 2.5
    c: Coincident(g9,g4)
    c: Coincident(g8,g5)
    c: Coincident(g9,g6)
    c: Coincident(g2,g7)
    c: Horizontal(g9)
    c: Horizontal(g8)
    c: Vertical(g7)
    c: Horizontal(g6,g2)
    c: DistanceX(g5,g4) = 0.2
    c: Coincident(g11,g2)
    c: Coincident(g11,g6)
    c: Diameter(g10) = 0.5
    c: DistanceX(g2,g2) = 1.5
    c: Tangent(g10,g11)
    c: DistanceX(g4,g4) = 0.1
    c: DistanceX(g8,g8) = 1.5
    c: DistanceX(g9,g9) = 1
    c: Tangent(g7,g10) = 1.5708
    c: Tangent(g6,g10) = 1.5708
    c: DistanceY(g4,g4) = 0.5
    c: DistanceY(g5,g4) = 0.05
FEATURE [PartDesign::Revolution] Revolution
  Angle = 360
  Axis = (0,2e-16,1)
  Base = (0,0,0)
  Placement = pos=(0,0,0) rot=(1,0,0;1.5708rad)
  Profile = -> Sketch005
  ReferenceAxis = -> Sketch005 [V_Axis]
  Reversed = true
FEATURE [PartDesign::Chamfer] Chamfer
  Angle = 45
  Base = -> Revolution [Edge11,Edge7]
  BaseFeature = -> Revolution
  ChamferType = 0
  FlipDirection = false
  Placement = pos=(0,0,0) rot=(1,0,0;1.5708rad)
  Size = 0.4
  Size2 = 1
  SupportTransform = false
  UseAllEdges = false
FEATURE [PartDesign::Body] Body001  label="rear bearing"
  Group = -> [Sketch005,Revolution,Chamfer]
  Origin = -> Origin002
  Placement = pos=(0,0,6.6) rot=(0,0,1;0rad)
  Tip = -> Chamfer
FEATURE [Sketcher::SketchObject] Sketch006
  AttachmentOffset = pos=(0,0,16) rot=(0,0,1;0rad)
  FullyConstrained = true
  MapMode = 5
  Placement = pos=(16,-3.6e-15,3.6e-15) rot=(0.57735,0.57735,0.57735;2.0944rad)
  Support = -> [YZ_Plane003]
  sketch-geometry (4):
    g0: LineSegment StartX=-7 StartY=3.8 StartZ=0 EndX=7 EndY=3.8 EndZ=0
    g1: LineSegment StartX=7 StartY=3.8 StartZ=0 EndX=7 EndY=3.2 EndZ=0
    g2: LineSegment StartX=7 StartY=3.2 StartZ=0 EndX=-7 EndY=3.2 EndZ=0
    g3: LineSegment StartX=-7 StartY=3.2 StartZ=0 EndX=-7 EndY=3.8 EndZ=0
  constraints (12):
    c: Coincident(g0,g1)
    c: Coincident(g1,g2)
    c: Coincident(g2,g3)
    c: Coincident(g3,g0)
    c: Horizontal(g0)
    c: Horizontal(g2)
    c: Vertical(g1)
    c: Vertical(g3)
    c: DistanceY(g1,g1) = 0.6
    c: DistanceX(g0,g0) = 14
    c: DistanceX(g-1,g0) = 7
    c: DistanceY(g-1,g1) = 3.2
FEATURE [PartDesign::Pad] Pad001  label="PCB"
  Direction = (1,-2e-16,3e-16)
  Length = 9.6
  Length2 = 10
  Placement = pos=(0,0,0) rot=(0.57735,0.57735,0.57735;2.0944rad)
  Profile = -> Sketch006
  ReferenceAxis = -> Sketch006 [N_Axis]
  Type = 0
FEATURE [Sketcher::SketchObject] Sketch007
  AttachmentOffset = pos=(0,0,16) rot=(0,0,1;0rad)
  FullyConstrained = true
  MapMode = 5
  Placement = pos=(16,-3.6e-15,3.6e-15) rot=(0.57735,0.57735,0.57735;2.0944rad)
  Support = -> [YZ_Plane003]
  sketch-geometry (11):
    g0: LineSegment StartX=7.8 StartY=8.8 StartZ=0 EndX=7.8 EndY=3.8 EndZ=0
    g1: LineSegment StartX=7.8 StartY=3.8 StartZ=0 EndX=0.5 EndY=3.8 EndZ=0
    g2: LineSegment StartX=-7.8 StartY=3.8 StartZ=0 EndX=-7.8 EndY=8.8 EndZ=0
    g3: LineSegment StartX=7.3 StartY=8.8 StartZ=0 EndX=7.3 EndY=4.2 EndZ=0
    g4: LineSegment StartX=7.3 StartY=4.2 StartZ=0 EndX=-7.3 EndY=4.2 EndZ=0
    g5: LineSegment StartX=-7.3 StartY=4.2 StartZ=0 EndX=-7.3 EndY=8.8 EndZ=0
    g6: LineSegment StartX=7.3 StartY=8.8 StartZ=0 EndX=7.8 EndY=8.8 EndZ=0
    g7: LineSegment StartX=-7.3 StartY=8.8 StartZ=0 EndX=-7.8 EndY=8.8 EndZ=0
    g8: LineSegment StartX=-0.5 StartY=3.8 StartZ=0 EndX=1e-16 EndY=3.4 EndZ=0
    g9: LineSegment StartX=0 StartY=3.4 StartZ=0 EndX=0.5 EndY=3.8 EndZ=0
    g10: LineSegment StartX=-0.5 StartY=3.8 StartZ=0 EndX=-7.8 EndY=3.8 EndZ=0
  constraints (33):
    c: Coincident(g0,g1)
    c: Coincident(g10,g2)
    c: Horizontal(g1)
    c: Vertical(g0)
    c: Vertical(g2)
    c: Coincident(g3,g4)
    c: Coincident(g4,g5)
    c: Horizontal(g4)
    c: Vertical(g3)
    c: Vertical(g5)
    c: DistanceX(g10,g0) = 15.6
    c: DistanceX(g-1,g0) = 7.8
    c: DistanceY(g-1,g0) = 3.8
    c: DistanceY(g10,g4) = 0.4
    c: DistanceX(g2,g5) = 0.5
    c: DistanceX(g3,g0) = 0.5
    c: Horizontal(g5,g3)
    c: DistanceY(g0,g0) = 5
    c: Coincident(g6,g3)
    c: Coincident(g6,g0)
    c: Coincident(g7,g5)
    c: Coincident(g7,g2)
    c: Horizontal(g7)
    c: Horizontal(g6)
    c: PointOnObject(g8,g-2)
    c: Coincident(g9,g8)
    c: DistanceX(g8,g9) = 1
    c: DistanceX(g-1,g9) = 0.5
    c: DistanceY(g8,g9) = 0.4
    c: Coincident(g1,g9)
    c: Coincident(g10,g8)
    c: Horizontal(g8,g1)
    c: Horizontal(g10)
FEATURE [PartDesign::Pad] Pad002  label="shell"
  BaseFeature = -> Pad001
  Direction = (1,-2e-16,3e-16)
  Length = 9
  Length2 = 10
  Placement = pos=(0,0,0) rot=(0.57735,0.57735,0.57735;2.0944rad)
  Profile = -> Sketch007
  ReferenceAxis = -> Sketch007 [N_Axis]
  Type = 0
FEATURE [Sketcher::SketchObject] Sketch008
  AttachmentOffset = pos=(0,0,16) rot=(0,0,1;0rad)
  FullyConstrained = true
  MapMode = 5
  Placement = pos=(16,-3.6e-15,3.6e-15) rot=(0.57735,0.57735,0.57735;2.0944rad)
  Support = -> [YZ_Plane003]
  sketch-geometry (8):
    g0: LineSegment StartX=-7 StartY=9.4 StartZ=0 EndX=7 EndY=9.4 EndZ=0
    g1: LineSegment StartX=7 StartY=9.4 StartZ=0 EndX=7 EndY=4.2 EndZ=0
    g2: LineSegment StartX=7 StartY=4.2 StartZ=0 EndX=6.1 EndY=4.2 EndZ=0
    g3: LineSegment StartX=-7 StartY=4.2 StartZ=0 EndX=-7 EndY=9.4 EndZ=0
    g4: LineSegment StartX=-6.1 StartY=4.2 StartZ=0 EndX=-6.1 EndY=4.5 EndZ=0
    g5: LineSegment StartX=-6.1 StartY=4.5 StartZ=0 EndX=6.1 EndY=4.5 EndZ=0
    g6: LineSegment StartX=6.1 StartY=4.5 StartZ=0 EndX=6.1 EndY=4.2 EndZ=0
    g7: LineSegment StartX=-6.1 StartY=4.2 StartZ=0 EndX=-7 EndY=4.2 EndZ=0
  constraints (24):
    c: Coincident(g0,g1)
    c: Coincident(g1,g2)
    c: Coincident(g7,g3)
    c: Coincident(g3,g0)
    c: Horizontal(g0)
    c: Horizontal(g2)
    c: Vertical(g1)
    c: Vertical(g3)
    c: DistanceX(g0,g0) = 14
    c: Vertical(g4)
    c: Coincident(g5,g4)
    c: Horizontal(g5)
    c: Coincident(g6,g5)
    c: Vertical(g6)
    c: Coincident(g2,g6)
    c: Coincident(g7,g4)
    c: DistanceY(g3,g3) = 5.2
    c: Horizontal(g7)
    c: Horizontal(g4,g2)
    c: DistanceY(g-1,g4) = 4.2
    c: DistanceX(g-1,g0) = 7
    c: DistanceY(g4,g4) = 0.3
    c: DistanceX(g7,g7) = 0.9
    c: DistanceX(g2,g2) = 0.9
FEATURE [PartDesign::Pad] Pad003  label="connectorBase"
  BaseFeature = -> Pad002
  Direction = (1,-2e-16,3e-16)
  Length = 6.4
  Length2 = 10
  Placement = pos=(0,0,0) rot=(0.57735,0.57735,0.57735;2.0944rad)
  Profile = -> Sketch008
  ReferenceAxis = -> Sketch008 [N_Axis]
  Type = 0
FEATURE [Sketcher::SketchObject] Sketch009
  FullyConstrained = true
  MapMode = 5
  Placement = pos=(22.4,-4.5e-15,4e-15) rot=(0.57735,0.57735,0.57735;2.0944rad)
  Support = -> [Pad003]
  sketch-geometry (24):
    g0: LineSegment StartX=-7 StartY=9.4 StartZ=0 EndX=-4 EndY=9.4 EndZ=0
    g1: LineSegment StartX=-4 StartY=9.4 StartZ=0 EndX=-4 EndY=8.8 EndZ=0
    g2: LineSegment StartX=-4 StartY=8.8 StartZ=0 EndX=-6.4 EndY=8.8 EndZ=0
    g3: LineSegment StartX=-6.4 StartY=8.8 StartZ=0 EndX=-6.4 EndY=7.8 EndZ=0
    g4: LineSegment StartX=-6.4 StartY=7.8 StartZ=0 EndX=-7 EndY=7.8 EndZ=0
    g5: LineSegment StartX=-7 StartY=7.8 StartZ=0 EndX=-7 EndY=9.4 EndZ=0
    g6: LineSegment StartX=4 StartY=9.4 StartZ=0 EndX=7 EndY=9.4 EndZ=0
    g7: LineSegment StartX=7 StartY=9.4 StartZ=0 EndX=7 EndY=7.8 EndZ=0
    g8: LineSegment StartX=7 StartY=7.8 StartZ=0 EndX=6.4 EndY=7.8 EndZ=0
    g9: LineSegment StartX=6.4 StartY=7.8 StartZ=0 EndX=6.4 EndY=8.8 EndZ=0
    g10: LineSegment StartX=6.4 StartY=8.8 StartZ=0 EndX=4 EndY=8.8 EndZ=0
    g11: LineSegment StartX=4 StartY=8.8 StartZ=0 EndX=4 EndY=9.4 EndZ=0
    g12: LineSegment StartX=7 StartY=7 StartZ=0 EndX=7 EndY=4.2 EndZ=0
    g13: LineSegment StartX=7 StartY=4.2 StartZ=0 EndX=6.1 EndY=4.2 EndZ=0
    g14: LineSegment StartX=6.1 StartY=4.2 StartZ=0 EndX=6.1 EndY=4.5 EndZ=0
    g15: LineSegment StartX=6.1 StartY=4.5 StartZ=0 EndX=-6.1 EndY=4.5 EndZ=0
    g16: LineSegment StartX=-6.1 StartY=4.5 StartZ=0 EndX=-6.1 EndY=4.2 EndZ=0
    g17: LineSegment StartX=-6.1 StartY=4.2 StartZ=0 EndX=-7 EndY=4.2 EndZ=0
    g18: LineSegment StartX=-7 StartY=4.2 StartZ=0 EndX=-7 EndY=7 EndZ=0
    g19: LineSegment StartX=-7 StartY=7 StartZ=0 EndX=-6.4 EndY=7 EndZ=0
    g20: LineSegment StartX=-6.4 StartY=7 StartZ=0 EndX=-6.4 EndY=5.3 EndZ=0
    g21: LineSegment StartX=-6.4 StartY=5.3 StartZ=0 EndX=6.4 EndY=5.3 EndZ=0
    g22: LineSegment StartX=6.4 StartY=5.3 StartZ=0 EndX=6.4 EndY=7 EndZ=0
    g23: LineSegment StartX=6.4 StartY=7 StartZ=0 EndX=7 EndY=7 EndZ=0
  constraints (72):
    c: Horizontal(g0)
    c: Coincident(g0,g1)
    c: Coincident(g1,g2)
    c: Horizontal(g2)
    c: Coincident(g2,g3)
    c: Vertical(g3)
    c: Coincident(g3,g4)
    c: Coincident(g4,g5)
    c: Coincident(g5,g0)
    c: Vertical(g5)
    c: Horizontal(g6)
    c: Coincident(g6,g7)
    c: Vertical(g7)
    c: Coincident(g7,g8)
    c: Horizontal(g8)
    c: Coincident(g8,g9)
    c: Vertical(g9)
    c: Coincident(g9,g10)
    c: Horizontal(g10)
    c: Coincident(g10,g11)
    c: Coincident(g11,g6)
    c: Vertical(g12)
    c: Coincident(g12,g13)
    c: Coincident(g13,g14)
    c: Coincident(g14,g15)
    c: Horizontal(g15)
    c: Coincident(g15,g16)
    c: Coincident(g16,g17)
    c: Coincident(g17,g18)
    c: Vertical(g18)
    c: Coincident(g18,g19)
    c: Horizontal(g19)
    c: Coincident(g19,g20)
    c: Vertical(g20)
    c: Coincident(g20,g21)
    c: Horizontal(g21)
    c: Coincident(g21,g22)
    c: Vertical(g22)
    c: Coincident(g22,g23)
    c: Coincident(g23,g12)
    c: Vertical(g14)
    c: Vertical(g11)
    c: Vertical(g1)
    c: Vertical(g16)
    c: Horizontal(g17)
    c: Horizontal(g13)
    c: Horizontal(g23)
    c: Horizontal(g4)
    c: DistanceY(g15,g20) = 0.8
    c: DistanceX(g17,g17) = 0.9
    c: DistanceX(g13,g13) = 0.9
    c: DistanceX(g17,g12) = 14
    c: DistanceX(g-1,g12) = 7
    c: DistanceY(g16,g16) = 0.3
    c: DistanceY(g-1,g16) = 4.2
    c: Horizontal(g19,g22)
    c: DistanceX(g23,g23) = 0.6
    c: DistanceX(g19,g19) = 0.6
    c: DistanceY(g18,g18) = 2.8
    c: Horizontal(g16,g13)
    c: Vertical(g8,g22)
    c: Vertical(g19,g3)
    c: Vertical(g4,g18)
    c: Vertical(g7,g12)
    c: Horizontal(g0,g6)
    c: Horizontal(g1,g10)
    c: DistanceY(g12,g6) = 5.2
    c: DistanceY(g7,g7) = 1.6
    c: Horizontal(g3,g8)
    c: DistanceY(g1,g1) = 0.6
    c: DistanceX(g0,g6) = 8
    c: DistanceX(g-1,g6) = 4
FEATURE [PartDesign::Pad] Pad004  label="connectorShell"
  BaseFeature = -> Pad003
  Direction = (1,-7e-16,3e-16)
  Length = 4.4
  Length2 = 10
  Placement = pos=(0,0,0) rot=(0.57735,0.57735,0.57735;2.0944rad)
  Profile = -> Sketch009
  ReferenceAxis = -> Sketch009 [N_Axis]
  Type = 0
FEATURE [Sketcher::SketchObject] Sketch010
  FullyConstrained = true
  MapMode = 5
  Placement = pos=(22.4,-4.5e-15,4e-15) rot=(0.57735,0.57735,0.57735;2.0944rad)
  Support = -> [Pad004]
  sketch-geometry (24):
    g0: LineSegment StartX=-5.3 StartY=7.7 StartZ=0 EndX=-4.7 EndY=7.7 EndZ=0
    g1: LineSegment StartX=-4.7 StartY=7.7 StartZ=0 EndX=-4.7 EndY=7.1 EndZ=0
    g2: LineSegment StartX=-4.7 StartY=7.1 StartZ=0 EndX=-5.3 EndY=7.1 EndZ=0
    g3: LineSegment StartX=-5.3 StartY=7.1 StartZ=0 EndX=-5.3 EndY=7.7 EndZ=0
    g4: LineSegment StartX=-3.3 StartY=7.7 StartZ=0 EndX=-2.7 EndY=7.7 EndZ=0
    g5: LineSegment StartX=-2.7 StartY=7.7 StartZ=0 EndX=-2.7 EndY=7.1 EndZ=0
    g6: LineSegment StartX=-2.7 StartY=7.1 StartZ=0 EndX=-3.3 EndY=7.1 EndZ=0
    g7: LineSegment StartX=-3.3 StartY=7.1 StartZ=0 EndX=-3.3 EndY=7.7 EndZ=0
    g8: LineSegment StartX=-1.3 StartY=7.7 StartZ=0 EndX=-0.7 EndY=7.7 EndZ=0
    g9: LineSegment StartX=-0.7 StartY=7.7 StartZ=0 EndX=-0.7 EndY=7.1 EndZ=0
    g10: LineSegment StartX=-0.7 StartY=7.1 StartZ=0 EndX=-1.3 EndY=7.1 EndZ=0
    g11: LineSegment StartX=-1.3 StartY=7.1 StartZ=0 EndX=-1.3 EndY=7.7 EndZ=0
    g12: LineSegment StartX=0.7 StartY=7.7 StartZ=0 EndX=1.3 EndY=7.7 EndZ=0
    g13: LineSegment StartX=1.3 StartY=7.7 StartZ=0 EndX=1.3 EndY=7.1 EndZ=0
    g14: LineSegment StartX=1.3 StartY=7.1 StartZ=0 EndX=0.7 EndY=7.1 EndZ=0
    g15: LineSegment StartX=0.7 StartY=7.1 StartZ=0 EndX=0.7 EndY=7.7 EndZ=0
    g16: LineSegment StartX=2.7 StartY=7.7 StartZ=0 EndX=3.3 EndY=7.7 EndZ=0
    g17: LineSegment StartX=3.3 StartY=7.7 StartZ=0 EndX=3.3 EndY=7.1 EndZ=0
    g18: LineSegment StartX=3.3 StartY=7.1 StartZ=0 EndX=2.7 EndY=7.1 EndZ=0
    g19: LineSegment StartX=2.7 StartY=7.1 StartZ=0 EndX=2.7 EndY=7.7 EndZ=0
    g20: LineSegment StartX=4.7 StartY=7.7 StartZ=0 EndX=5.3 EndY=7.7 EndZ=0
    g21: LineSegment StartX=5.3 StartY=7.7 StartZ=0 EndX=5.3 EndY=7.1 EndZ=0
    g22: LineSegment StartX=5.3 StartY=7.1 StartZ=0 EndX=4.7 EndY=7.1 EndZ=0
    g23: LineSegment StartX=4.7 StartY=7.1 StartZ=0 EndX=4.7 EndY=7.7 EndZ=0
  constraints (72):
    c: Coincident(g0,g1)
    c: Coincident(g1,g2)
    c: Coincident(g2,g3)
    c: Coincident(g3,g0)
    c: Horizontal(g0)
    c: Horizontal(g2)
    c: Vertical(g1)
    c: Vertical(g3)
    c: Coincident(g4,g5)
    c: Coincident(g5,g6)
    c: Coincident(g6,g7)
    c: Coincident(g7,g4)
    c: Horizontal(g4)
    c: Horizontal(g6)
    c: Vertical(g5)
    c: Vertical(g7)
    c: Coincident(g8,g9)
    c: Coincident(g9,g10)
    c: Coincident(g10,g11)
    c: Coincident(g11,g8)
    c: Horizontal(g8)
    c: Horizontal(g10)
    c: Vertical(g9)
    c: Vertical(g11)
    c: Coincident(g12,g13)
    c: Coincident(g13,g14)
    c: Coincident(g14,g15)
    c: Coincident(g15,g12)
    c: Horizontal(g12)
    c: Horizontal(g14)
    c: Vertical(g13)
    c: Vertical(g15)
    c: Coincident(g16,g17)
    c: Coincident(g17,g18)
    c: Coincident(g18,g19)
    c: Coincident(g19,g16)
    c: Horizontal(g16)
    c: Horizontal(g18)
    c: Vertical(g17)
    c: Vertical(g19)
    c: Coincident(g20,g21)
    c: Coincident(g21,g22)
    c: Coincident(g22,g23)
    c: Coincident(g23,g20)
    c: Horizontal(g20)
    c: Horizontal(g22)
    c: Vertical(g21)
    c: Vertical(g23)
    c: Horizontal(g0,g4)
    c: Horizontal(g4,g8)
    c: Horizontal(g8,g12)
    c: Horizontal(g12,g16)
    c: Horizontal(g16,g20)
    c: Horizontal(g1,g6)
    c: Horizontal(g5,g10)
    c: Horizontal(g9,g14)
    c: Horizontal(g13,g18)
    c: Horizontal(g17,g22)
    c: Equal(g2,g6)
    c: Equal(g6,g10)
    c: Equal(g10,g14)
    c: Equal(g14,g18)
    c: Equal(g18,g22)
    c: DistanceX(g0,g0) = 0.6
    c: DistanceY(g3,g3) = 0.6
    c: Distance(g0,g4) = 2
    c: Distance(g4,g8) = 2
    c: Distance(g8,g12) = 2
    c: Distance(g12,g16) = 2
    c: Distance(g16,g20) = 2
    c: DistanceX(g-1,g14) = 0.7
    c: DistanceY(g-1,g14) = 7.1
FEATURE [PartDesign::Pad] Pad005  label="connectorPins"
  BaseFeature = -> Pad004
  Direction = (1,-6e-16,3e-16)
  Length = 3.5
  Length2 = 10
  Placement = pos=(0,0,0) rot=(0.57735,0.57735,0.57735;2.0944rad)
  Profile = -> Sketch010
  ReferenceAxis = -> Sketch010 [N_Axis]
  Type = 0
FEATURE [PartDesign::Body] Body002  label="connector"
  Group = -> [Sketch006,Pad001,Sketch007,Pad002,Sketch008,Pad003,Sketch009,Pad004,Sketch010,Pad005]
  Origin = -> Origin003
  Tip = -> Pad005
FEATURE [PartDesign::Body] Body003  label="shaft"
  Origin = -> Origin004
  Placement = pos=(0,0,2.8) rot=(0,0,1;0rad)
FEATURE [Sketcher::SketchObject] Sketch012
  FullyConstrained = true
  MapMode = 5
  Support = -> [XY_Plane004]
  sketch-geometry (1):
    g0: Circle CenterX=0 CenterY=0 CenterZ=0 NormalX=0 NormalY=0 NormalZ=1 AngleXU=0 Radius=2.5
  constraints (2):
    c: Coincident(g0,g-1)
    c: Diameter(g0) = 5
FEATURE [PartDesign::Pad] Pad006
  Direction = (0,0,1)
  Length = 58
  Length2 = 10
  Profile = -> Sketch012
  ReferenceAxis = -> Sketch012 [N_Axis]
  Type = 0
FEATURE [Sketcher::SketchObject] Sketch013
  FullyConstrained = true
  MapMode = 5
  Placement = pos=(0,0,58) rot=(0,0,1;0rad)
  Support = -> [Pad006]
  sketch-geometry (2):
    g0: ArcOfCircle CenterX=0 CenterY=0 CenterZ=0 NormalX=0 NormalY=0 NormalZ=1 AngleXU=0 Radius=2.5 StartAngle=5.63968 EndAngle=6.92669
    g1: LineSegment StartX=2 StartY=1.5 StartZ=0 EndX=2 EndY=-1.5 EndZ=0
  constraints (6):
    c: Coincident(g0,g-1)
    c: Coincident(g1,g0)
    c: Coincident(g1,g0)
    c: Vertical(g1)
    c: Diameter(g0) = 5
    c: DistanceX(g0,g0) = 2
FEATURE [PartDesign::Pocket] Pocket003
  Direction = (0,0,-1)
  Length = 18
  Length2 = 5
  Profile = -> Sketch013
  ReferenceAxis = -> Sketch013 [N_Axis]
  Type = 0
FEATURE [Sketcher::SketchObject] Sketch014  label="basic outline001"
  FullyConstrained = true
  MapMode = 5
  Support = -> [XY_Plane005]
  sketch-geometry (9):
    g0: ArcOfCircle CenterX=0 CenterY=0 CenterZ=0 NormalX=0 NormalY=0 NormalZ=1 AngleXU=0 Radius=25.2 StartAngle=2.15648 EndAngle=2.55591
    g1: ArcOfCircle CenterX=0 CenterY=0 CenterZ=0 NormalX=0 NormalY=0 NormalZ=1 AngleXU=0 Radius=25.2 StartAngle=5.29807 EndAngle=5.6975
    g2: ArcOfCircle CenterX=0 CenterY=0 CenterZ=0 NormalX=0 NormalY=0 NormalZ=1 AngleXU=0 Radius=25.2 StartAngle=0.585686 EndAngle=0.985111
    g3: ArcOfCircle CenterX=0 CenterY=0 CenterZ=0 NormalX=0 NormalY=0 NormalZ=1 AngleXU=0 Radius=25.2 StartAngle=3.72728 EndAngle=4.1267
    g4: LineSegment StartX=-13.9298 StartY=21 StartZ=0 EndX=13.9298 EndY=21 EndZ=0
    g5: LineSegment StartX=21 StartY=13.9298 StartZ=0 EndX=21 EndY=-13.9298 EndZ=0
    g6: LineSegment StartX=-13.9298 StartY=-21 StartZ=0 EndX=13.9298 EndY=-21 EndZ=0
    g7: LineSegment StartX=-21 StartY=13.9298 StartZ=0 EndX=-21 EndY=-13.9298 EndZ=0
    g8: Circle CenterX=0 CenterY=0 CenterZ=0 NormalX=0 NormalY=0 NormalZ=1 AngleXU=0 Radius=4.5
  constraints (26):
    c: Coincident(g0,g-1)
    c: Coincident(g1,g0)
    c: Coincident(g2,g0)
    c: Coincident(g3,g0)
    c: Equal(g0,g1)
    c: Equal(g1,g2)
    c: Equal(g2,g3)
    c: Coincident(g4,g0)
    c: Coincident(g4,g2)
    c: Horizontal(g4)
    c: Coincident(g5,g2)
    c: Coincident(g5,g1)
    c: Vertical(g5)
    c: Coincident(g6,g3)
    c: Coincident(g6,g1)
    c: Coincident(g7,g0)
    c: Coincident(g7,g3)
    c: Vertical(g7)
    c: Horizontal(g6)
    c: DistanceX(g0,g2) = 42
    c: DistanceY(g1,g2) = 42
    c: DistanceY(g0,g2) = 21
    c: DistanceX(g0,g0) = 21
    c: Coincident(g8,g0)
    c: Diameter(g8) = 9
    c: Diameter(g0) = 50.4
FEATURE [PartDesign::Pad] Pad007  label="statorLamination"
  Direction = (0,0,1)
  Length = 0.52
  Length2 = 10
  Profile = -> Sketch014
  ReferenceAxis = -> Sketch014 [N_Axis]
  Type = 0
FEATURE [PartDesign::LinearPattern] LinearPattern  label="stack"
  BaseFeature = -> Pad007
  Direction = -> Z_Axis005
  Length = 19.48
  Occurrences = 40
  Originals = -> [Pad007]
FEATURE [PartDesign::Body] Body004  label="stator"
  Group = -> [Sketch014,Pad007,LinearPattern]
  Origin = -> Origin005
  Placement = pos=(0,0,9.4) rot=(0,0,1;0rad)
  Tip = -> LinearPattern
FEATURE [Sketcher::SketchObject] Sketch015  label="basic outline002"
  FullyConstrained = true
  MapMode = 5
  Support = -> [XY_Plane006]
  sketch-geometry (13):
    g0: ArcOfCircle CenterX=0 CenterY=0 CenterZ=0 NormalX=0 NormalY=0 NormalZ=1 AngleXU=0 Radius=26.8 StartAngle=2.24118 EndAngle=2.47121
    g1: ArcOfCircle CenterX=0 CenterY=0 CenterZ=0 NormalX=0 NormalY=0 NormalZ=1 AngleXU=0 Radius=26.8 StartAngle=5.38277 EndAngle=5.6128
    g2: ArcOfCircle CenterX=0 CenterY=0 CenterZ=0 NormalX=0 NormalY=0 NormalZ=1 AngleXU=0 Radius=26.8 StartAngle=0.670386 EndAngle=0.900411
    g3: ArcOfCircle CenterX=0 CenterY=0 CenterZ=0 NormalX=0 NormalY=0 NormalZ=1 AngleXU=0 Radius=26.8 StartAngle=3.81198 EndAngle=4.042
    g4: LineSegment StartX=-16.6505 StartY=21 StartZ=0 EndX=16.6505 EndY=21 EndZ=0
    g5: LineSegment StartX=21 StartY=16.6505 StartZ=0 EndX=21 EndY=-16.6505 EndZ=0
    g6: LineSegment StartX=-16.6505 StartY=-21 StartZ=0 EndX=16.6505 EndY=-21 EndZ=0
    g7: LineSegment StartX=-21 StartY=16.6505 StartZ=0 EndX=-21 EndY=-16.6505 EndZ=0
    g8: Circle CenterX=0 CenterY=0 CenterZ=0 NormalX=0 NormalY=0 NormalZ=1 AngleXU=0 Radius=4.5
    g9: Circle CenterX=-15.5 CenterY=15.5 CenterZ=0 NormalX=0 NormalY=0 NormalZ=1 AngleXU=0 Radius=1.5
    g10: Circle CenterX=15.5 CenterY=15.5 CenterZ=0 NormalX=0 NormalY=0 NormalZ=1 AngleXU=0 Radius=1.5
    g11: Circle CenterX=15.5 CenterY=-15.5 CenterZ=0 NormalX=0 NormalY=0 NormalZ=1 AngleXU=0 Radius=1.5
    g12: Circle CenterX=-15.5 CenterY=-15.5 CenterZ=0 NormalX=0 NormalY=0 NormalZ=1 AngleXU=0 Radius=1.5
  constraints (38):
    c: Coincident(g0,g-1)
    c: Coincident(g1,g0)
    c: Coincident(g2,g0)
    c: Coincident(g3,g0)
    c: Equal(g0,g1)
    c: Equal(g1,g2)
    c: Equal(g2,g3)
    c: Radius(g0) = 26.8
    c: Coincident(g4,g0)
    c: Coincident(g4,g2)
    c: Horizontal(g4)
    c: Coincident(g5,g2)
    c: Coincident(g5,g1)
    c: Vertical(g5)
    c: Coincident(g6,g3)
    c: Coincident(g6,g1)
    c: Coincident(g7,g0)
    c: Coincident(g7,g3)
    c: Vertical(g7)
    c: Horizontal(g6)
    c: DistanceX(g0,g2) = 42
    c: DistanceY(g1,g2) = 42
    c: DistanceY(g0,g2) = 21
    c: DistanceX(g0,g0) = 21
    c: Coincident(g8,g0)
    c: Diameter(g8) = 9
    c: Vertical(g9,g12)
    c: Vertical(g11,g10)
    c: Horizontal(g9,g10)
    c: Horizontal(g12,g11)
    c: Equal(g9,g10)
    c: Equal(g11,g10)
    c: Equal(g11,g12)
    c: Diameter(g9) = 3
    c: DistanceX(g9,g10) = 31
    c: DistanceY(g11,g10) = 31
    c: DistanceY(g0,g10) = 15.5
    c: DistanceX(g0,g10) = 15.5
FEATURE [PartDesign::Pad] Pad008
  Direction = (0,0,1)
  Length = 8
  Length2 = 10
  Profile = -> Sketch015
  ReferenceAxis = -> Sketch015 [N_Axis]
  Type = 0
FEATURE [Sketcher::SketchObject] Sketch016
  FullyConstrained = true
  MapMode = 5
  Placement = pos=(0,0,8) rot=(0,0,1;0rad)
  Support = -> [Pad008]
  sketch-geometry (2):
    g0: Circle CenterX=0 CenterY=0 CenterZ=0 NormalX=0 NormalY=0 NormalZ=1 AngleXU=0 Radius=4.5
    g1: Circle CenterX=0 CenterY=0 CenterZ=0 NormalX=0 NormalY=0 NormalZ=1 AngleXU=0 Radius=11
  constraints (4):
    c: Coincident(g0,g-1)
    c: Coincident(g1,g0)
    c: Diameter(g1) = 22
    c: Diameter(g0) = 9
FEATURE [PartDesign::Pad] Pad009  label="locating boss"
  BaseFeature = -> Pad008
  Direction = (0,0,1)
  Length = 2
  Length2 = 10
  Profile = -> Sketch016
  ReferenceAxis = -> Sketch016 [N_Axis]
  Type = 0
FEATURE [Sketcher::SketchObject] Sketch017
  FullyConstrained = true
  MapMode = 5
  Support = -> [XY_Plane006]
  sketch-geometry (1):
    g0: Circle CenterX=0 CenterY=0 CenterZ=0 NormalX=0 NormalY=0 NormalZ=1 AngleXU=0 Radius=8
  constraints (2):
    c: Coincident(g0,g-1)
    c: Diameter(g0) = 16
FEATURE [PartDesign::Pocket] Pocket004
  BaseFeature = -> Pad009
  Direction = (0,0,-1)
  Length = 8.4
  Length2 = 5
  Profile = -> Sketch017
  ReferenceAxis = -> Sketch017 [N_Axis]
  Reversed = true
  Type = 0
FEATURE [Sketcher::SketchObject] Sketch018
  FullyConstrained = true
  MapMode = 5
  Placement = pos=(0,0,0) rot=(1,0,0;1.5708rad)
  Support = -> [XZ_Plane007]
  sketch-geometry (12):
    g0: LineSegment StartX=2.5 StartY=2.55 StartZ=0 EndX=8 EndY=2.55 EndZ=0
    g1: LineSegment StartX=8 StartY=2.55 StartZ=0 EndX=8 EndY=-2.45 EndZ=0
    g2: LineSegment StartX=8 StartY=-2.45 StartZ=0 EndX=6.5 EndY=-2.45 EndZ=0
    g3: LineSegment StartX=2.5 StartY=-2.5 StartZ=0 EndX=2.5 EndY=2.55 EndZ=0
    g4: LineSegment StartX=4.2 StartY=-2.45 StartZ=0 EndX=4.1 EndY=-1.95 EndZ=0
    g5: LineSegment StartX=4.1 StartY=-1.95 StartZ=0 EndX=4 EndY=-2.5 EndZ=0
    g6: LineSegment StartX=5.2 StartY=-2.45 StartZ=0 EndX=6.13734 EndY=-1.97682 EndZ=0
    g7: LineSegment StartX=6.5 StartY=-2.2 StartZ=0 EndX=6.5 EndY=-2.45 EndZ=0
    g8: LineSegment StartX=4 StartY=-2.5 StartZ=0 EndX=2.5 EndY=-2.5 EndZ=0
    g9: LineSegment StartX=5.2 StartY=-2.45 StartZ=0 EndX=4.2 EndY=-2.45 EndZ=0
    g10: ArcOfCircle CenterX=6.25 CenterY=-2.2 CenterZ=0 NormalX=0 NormalY=0 NormalZ=1 AngleXU=0 Radius=0.25 StartAngle=2.03828 EndAngle=6.28319
    g11: LineSegment StartX=6.5 StartY=-2.45 StartZ=0 EndX=5.2 EndY=-2.45 EndZ=0
  constraints (34):
    c: Coincident(g0,g1)
    c: Coincident(g1,g2)
    c: Coincident(g8,g3)
    c: Coincident(g3,g0)
    c: Horizontal(g0)
    c: Horizontal(g2)
    c: Vertical(g1)
    c: Vertical(g3)
    c: Coincident(g5,g4)
    c: DistanceX(g-1,g8) = 2.5
    c: DistanceX(g-1,g1) = 8
    c: DistanceY(g1,g1) = 5
    c: DistanceY(g8,g-1) = 2.5
    c: Coincident(g9,g4)
    c: Coincident(g8,g5)
    c: Coincident(g9,g6)
    c: Coincident(g2,g7)
    c: Horizontal(g9)
    c: Horizontal(g8)
    c: Vertical(g7)
    c: Horizontal(g6,g2)
    c: DistanceX(g5,g4) = 0.2
    c: Coincident(g11,g2)
    c: Coincident(g11,g6)
    c: Diameter(g10) = 0.5
    c: DistanceX(g2,g2) = 1.5
    c: Tangent(g10,g11)
    c: DistanceX(g4,g4) = 0.1
    c: DistanceX(g8,g8) = 1.5
    c: DistanceX(g9,g9) = 1
    c: Tangent(g7,g10) = 1.5708
    c: Tangent(g6,g10) = 1.5708
    c: DistanceY(g4,g4) = 0.5
    c: DistanceY(g5,g4) = 0.05
FEATURE [PartDesign::Revolution] Revolution001
  Angle = 360
  Axis = (0,2e-16,1)
  Base = (0,0,0)
  Placement = pos=(0,0,0) rot=(1,0,0;1.5708rad)
  Profile = -> Sketch018
  ReferenceAxis = -> Sketch018 [V_Axis]
  Reversed = true
FEATURE [PartDesign::Chamfer] Chamfer001
  Angle = 45
  Base = -> Revolution001 [Edge11,Edge7]
  BaseFeature = -> Revolution001
  ChamferType = 0
  FlipDirection = false
  Placement = pos=(0,0,0) rot=(1,0,0;1.5708rad)
  Size = 0.4
  Size2 = 1
  SupportTransform = false
  UseAllEdges = false
FEATURE [PartDesign::Body] Body006  label="front bearing"
  Group = -> [Sketch018,Revolution001,Chamfer001]
  Origin = -> Origin007
  Placement = pos=(0,0,34.6) rot=(0,1,0;3.14159rad)
  Tip = -> Chamfer001
FEATURE [PartDesign::Chamfer] Chamfer002
  Angle = 45
  Base = -> Pocket003 [Edge5,Edge1]
  ChamferType = 1
  FlipDirection = false
  Size = 0.8
  Size2 = 0.4
  SupportTransform = false
  UseAllEdges = false
FEATURE [PartDesign::Chamfer] Chamfer003
  Angle = 45
  Base = -> Pocket004 [Edge42,Edge30,Edge28,Edge26,Edge27,Edge44,Edge43]
  BaseFeature = -> Pocket004
  ChamferType = 0
  FlipDirection = false
  Size = 0.2
  Size2 = 1
  SupportTransform = false
  UseAllEdges = false
FEATURE [PartDesign::Fillet] Fillet
  Base = -> Pocket002 [Edge48,Edge5,Edge40,Edge45,Edge52,Edge53,Edge50,Edge47,Edge44,Edge9,Edge2,Edge1,Edge24,Edge21,Edge22,Edge25]
  BaseFeature = -> Pocket002
  Radius = 0.4
  SupportTransform = false
  UseAllEdges = false
FEATURE [PartDesign::Fillet] Fillet001
  Base = -> Pocket002
  BaseFeature = -> Pocket002
  Radius = 0.4
  SupportTransform = false
  UseAllEdges = false
FEATURE [PartDesign::Fillet] Fillet002
  Base = -> Chamfer003 [Edge17,Edge16,Edge19,Edge23,Edge29,Edge27,Edge25,Edge21]
  BaseFeature = -> Chamfer003
  Radius = 0.4
  SupportTransform = false
  UseAllEdges = false
FEATURE [PartDesign::Body] Body005  label="front end cap"
  Group = -> [Sketch015,Pad008,Sketch016,Pad009,Sketch017,Pocket004,Chamfer003,Fillet002]
  Origin = -> Origin006
  Placement = pos=(0,0,29.4) rot=(0,0,1;0rad)
  Tip = -> Fillet002
FEATURE [Part::FeaturePython] Screw  label="M3x10-Screw"  # WARN: FeaturePython — macro-defined, semantics opaque (R4)
  Diameter = 1
  Invert = false
  LeftHanded = false
  Length = 2
  LengthCustom = 10
  MatchOuter = false
  OffsetAngle = 0
  Placement = pos=(15.5,15.5,2) rot=(0,1,0;3.14159rad)
  Thread = false
  Type = 85
FEATURE [Part::FeaturePython] Screw001  label="M3x10-Screw004"  # WARN: FeaturePython — macro-defined, semantics opaque (R4)
  Diameter = 1
  Invert = false
  LeftHanded = false
  Length = 2
  LengthCustom = 10
  MatchOuter = false
  OffsetAngle = 0
  Placement = pos=(15.5,-15.5,2) rot=(0,1,0;3.14159rad)
  Thread = false
  Type = 85
FEATURE [Part::FeaturePython] Screw002  label="M3x10-Screw005"  # WARN: FeaturePython — macro-defined, semantics opaque (R4)
  Diameter = 1
  Invert = false
  LeftHanded = false
  Length = 2
  LengthCustom = 10
  MatchOuter = false
  OffsetAngle = 0
  Placement = pos=(-15.5,15.5,2) rot=(0,1,0;3.14159rad)
  Thread = false
  Type = 85
FEATURE [Part::FeaturePython] Screw003  label="M3x10-Screw006"  # WARN: FeaturePython — macro-defined, semantics opaque (R4)
  Diameter = 1
  Invert = false
  LeftHanded = false
  Length = 2
  LengthCustom = 10
  MatchOuter = false
  OffsetAngle = 0
  Placement = pos=(-15.5,-15.5,2) rot=(0,1,0;3.14159rad)
  Thread = false
  Type = 85
FEATURE [PartDesign::CoordinateSystem] LCS_shaft
  AttacherType = Attacher::AttachEngine3D
  MapMode = 45
  Placement = pos=(-0.226119,0,58) rot=(0,0,1;0rad)
  Support = -> [Chamfer002]
FEATURE [PartDesign::CoordinateSystem] LCS_forStand
  AttacherType = Attacher::AttachEngine3D
  MapMode = 45
  Placement = pos=(1.05365,6.3e-15,0) rot=(0,0,1;1.5708rad)
  Support = -> [Fillet001]
FEATURE [App::Part] Part  label="17HS4401S Stepper Motor"
  Group = -> [Body,Sketch001,Body001,Body002,Body003,Body004,Body005,Body006,Screw,Screw001,Screw002,Screw003,Sketch012,Pad006,Sketch013,Pocket003,Chamfer002,LCS_shaft,Fillet,Fillet001,Sketch,Sketch003,Pocket001,Pocket002,Pocket,Sketch004,Sketch002,Pad,LCS_forStand]
  Origin = -> Origin001
---- part 6201ZZ002_Bearing.FCStd = doc fcstd_81c71e17948a ----
FCSTD DOCUMENT  (FreeCAD 0.20R29177 +426 (Git))
Label: 6201ZZ002_Bearing
License: All rights reserved
LicenseURL: http://en.wikipedia.org/wiki/All_rights_reserved
objects: PartDesign::CoordinateSystem×2, Sketcher::SketchObject×1, PartDesign::Pad×1, PartDesign::Body×1
note: 6 computed .brp shape members not serialized (recipe doc carries the construction recipe); baked Part::Feature solids carry a one-line shape summary decoded from their .brp

FEATURE [Sketcher::SketchObject] Sketch
  FullyConstrained = true
  MapMode = 5
  Support = -> [XY_Plane]
  sketch-geometry (2):
    g0: Circle CenterX=0 CenterY=0 CenterZ=0 NormalX=0 NormalY=0 NormalZ=1 AngleXU=0 Radius=15
    g1: Circle CenterX=0 CenterY=0 CenterZ=0 NormalX=0 NormalY=0 NormalZ=1 AngleXU=0 Radius=7
  constraints (4):
    c: Coincident(g0,g-1)
    c: Diameter(g0) = 30
    c: Coincident(g1,g0)
    c: Diameter(g1) = 14
FEATURE [PartDesign::Pad] Pad
  Direction = (0,0,1)
  Length = 10
  Length2 = 10
  Profile = -> Sketch
  ReferenceAxis = -> Sketch [N_Axis]
  Type = 0
FEATURE [PartDesign::CoordinateSystem] LCS_1
  AttacherType = Attacher::AttachEngine3D
  MapMode = 45
  Placement = pos=(-7.1e-15,-9e-16,10) rot=(0,0,1;0rad)
  Support = -> [Pad]
FEATURE [PartDesign::CoordinateSystem] bottom_LCS
  AttacherType = Attacher::AttachEngine3D
  MapMode = 12
  Placement = pos=(0,0,0) rot=(1,0,0;1.5708rad)
  Support = -> [Pad]
FEATURE [PartDesign::Body] Body  label="Fake_bearing"
  Group = -> [Sketch,Pad,LCS_1,bottom_LCS]
  Origin = -> Origin
  Tip = -> Pad
---- part BearingRotator.FCStd = doc fcstd_1fdbf57dca91 ----
FCSTD DOCUMENT  (FreeCAD 0.20R29177 +426 (Git))
Label: BearingRotator
License: All rights reserved
LicenseURL: http://en.wikipedia.org/wiki/All_rights_reserved
objects: PartDesign::CoordinateSystem×2, Sketcher::SketchObject×1, PartDesign::Body×1
note: 4 computed .brp shape members not serialized (recipe doc carries the construction recipe); baked Part::Feature solids carry a one-line shape summary decoded from their .brp
EXTERNAL_REF file=assembly4.FCStd obj=Variables

FEATURE [Sketcher::SketchObject] Sketch  label="RotatorSketch"
  FullyConstrained = true
  MapMode = 5
  Support = -> [XY_Plane]
  expr: Constraints[2] = assembly4#Variables.BearingRotatorVar
  sketch-geometry (1):
    g0: LineSegment StartX=0 StartY=0 StartZ=0 EndX=-20 EndY=-34.641 EndZ=0
  constraints (3):
    c: Coincident(g0,g-1)
    c: Distance(g0) = 40
    c: Angle(g-1,g0) = -2.0944
FEATURE [PartDesign::CoordinateSystem] RotatorLCS
  AttacherType = Attacher::AttachEngine3D
  MapMode = 7
  Placement = pos=(0,0,0) rot=(0.186157,0.694747,0.694747;2.77349rad)
  Support = -> [Sketch]
FEATURE [PartDesign::CoordinateSystem] RotatorPosition
  AttacherType = Attacher::AttachEngine3D
FEATURE [PartDesign::Body] Body  label="RotatorBody"
  Group = -> [Sketch,RotatorLCS,RotatorPosition]
  Origin = -> Origin
---- part FallAnim.FCStd = doc fcstd_4c6df93f8716 ----
FCSTD DOCUMENT  (FreeCAD 0.20R29177 +426 (Git))
Label: FallAnim
License: All rights reserved
LicenseURL: http://en.wikipedia.org/wiki/All_rights_reserved
objects: PartDesign::CoordinateSystem×2, Sketcher::SketchObject×1, PartDesign::Body×1
note: 4 computed .brp shape members not serialized (recipe doc carries the construction recipe); baked Part::Feature solids carry a one-line shape summary decoded from their .brp
EXTERNAL_REF file=assembly4.FCStd obj=Variables

FEATURE [PartDesign::CoordinateSystem] LCS_Origin
  AttacherType = Attacher::AttachEngine3D
  MapMode = 2
  Support = -> [X_Axis]
FEATURE [Sketcher::SketchObject] Sketch
  FullyConstrained = true
  MapMode = 5
  Placement = pos=(0,0,0) rot=(1,0,0;1.5708rad)
  Support = -> [XZ_Plane]
  expr: Constraints[2] = assembly4#Variables.FallHandlerVar
  sketch-geometry (1):
    g0: LineSegment StartX=0 StartY=0 StartZ=0 EndX=0 EndY=-900 EndZ=0
  constraints (3):
    c: Coincident(g0,g-1)
    c: PointOnObject(g0,g-2)
    c: DistanceY(g0,g0) = 900
FEATURE [PartDesign::CoordinateSystem] LCS_fallhandler
  AttacherType = Attacher::AttachEngine3D
  MapMode = 7
  Placement = pos=(0,1.998e-13,-900) rot=(0,0,1;0rad)
  Support = -> [Sketch]
FEATURE [PartDesign::Body] fallSketchBody
  Group = -> [LCS_Origin,Sketch,LCS_fallhandler]
  Origin = -> Origin
---- part ImageRecogBox.FCStd = doc fcstd_bc312f18e636 ----
FCSTD DOCUMENT  (FreeCAD 0.20R29177 +426 (Git))
Label: ImageRecogBox
License: All rights reserved
LicenseURL: http://en.wikipedia.org/wiki/All_rights_reserved
objects: Sketcher::SketchObject×17, PartDesign::Pad×12, PartDesign::CoordinateSystem×5, PartDesign::Chamfer×4, PartDesign::Pocket×3, PartDesign::Hole×2, PartDesign::Body×1
note: 65 computed .brp shape members not serialized (recipe doc carries the construction recipe); baked Part::Feature solids carry a one-line shape summary decoded from their .brp

FEATURE [Sketcher::SketchObject] Sketch
  FullyConstrained = true
  MapMode = 5
  Support = -> [XY_Plane]
  sketch-geometry (14):
    g0: LineSegment StartX=86.6025 StartY=50 StartZ=0 EndX=0 EndY=100 EndZ=0
    g1: LineSegment StartX=4.3e-15 StartY=100 StartZ=0 EndX=-86.6025 EndY=50 EndZ=0
    g2: LineSegment StartX=-86.6025 StartY=50 StartZ=0 EndX=-86.6025 EndY=-50 EndZ=0
    g3: LineSegment StartX=-86.6025 StartY=-50 StartZ=0 EndX=0 EndY=-100 EndZ=0
    g4: LineSegment StartX=0 StartY=-100 StartZ=0 EndX=86.6025 EndY=-50 EndZ=0
    g5: LineSegment StartX=86.6025 StartY=-50 StartZ=0 EndX=86.6025 EndY=50 EndZ=0
    g6: Circle CenterX=0 CenterY=0 CenterZ=0 NormalX=0 NormalY=0 NormalZ=1 AngleXU=0 Radius=100
    g7: LineSegment StartX=87.4686 StartY=-50.5 StartZ=0 EndX=87.4686 EndY=50.5 EndZ=0
    g8: LineSegment StartX=87.4686 StartY=50.5 StartZ=0 EndX=-1.42e-14 EndY=101 EndZ=0
    g9: LineSegment StartX=-1.48e-14 StartY=101 StartZ=0 EndX=-87.4686 EndY=50.5 EndZ=0
    g10: LineSegment StartX=-87.4686 StartY=50.5 StartZ=0 EndX=-87.4686 EndY=-50.5 EndZ=0
    g11: LineSegment StartX=-87.4686 StartY=-50.5 StartZ=0 EndX=0 EndY=-101 EndZ=0
    g12: LineSegment StartX=0 StartY=-101 StartZ=0 EndX=87.4686 EndY=-50.5 EndZ=0
    g13: Circle CenterX=0 CenterY=0 CenterZ=0 NormalX=0 NormalY=0 NormalZ=1 AngleXU=0 Radius=101
  constraints (33):
    c: Coincident(g0,g1)
    c: Coincident(g1,g2)
    c: Coincident(g2,g3)
    c: Coincident(g3,g4)
    c: Coincident(g4,g5)
    c: Coincident(g5,g0)
    c: Equal(g0, g1-g5) x5
    c: PointOnObject(g0,g6)
    c: PointOnObject(g1,g6)
    c: PointOnObject(g2,g6)
    c: PointOnObject(g3,g6)
    c: PointOnObject(g4,g6)
    c: PointOnObject(g5,g6)
    c: Coincident(g6,g-1)
    c: Vertical(g5)
    c: Coincident(g7,g8)
    c: Coincident(g8,g9)
    c: Coincident(g9,g10)
    c: Coincident(g10,g11)
    c: Coincident(g11,g12)
    c: Coincident(g12,g7)
    c: Equal(g7, g8-g12) x5
    c: PointOnObject(g7,g13)
    c: PointOnObject(g8,g13)
    c: PointOnObject(g9,g13)
    c: PointOnObject(g10,g13)
    c: PointOnObject(g11,g13)
    c: PointOnObject(g12,g13)
    c: Coincident(g13,g6)
    c: Vertical(g7)
    c: Diameter(g6) = 200
    c: DistanceY(g5,g5) = 100
    c: Diameter(g13) = 202
FEATURE [PartDesign::Pad] Pad
  Direction = (0,0,1)
  Length = 150
  Length2 = 10
  Profile = -> Sketch
  ReferenceAxis = -> Sketch [N_Axis]
  Type = 0
FEATURE [Sketcher::SketchObject] Sketch001
  ExternalGeometry = -> [Pad]
  FullyConstrained = true
  MapMode = 5
  Placement = pos=(0,0,0) rot=(1,0,0;3.14159rad)
  Support = -> [Pad]
  sketch-geometry (4):
    g0: LineSegment StartX=103.603 StartY=0 StartZ=0 EndX=86.6025 EndY=0 EndZ=0
    g1: LineSegment StartX=86.6025 StartY=0 StartZ=0 EndX=86.6025 EndY=-10 EndZ=0
    g2: LineSegment StartX=86.6025 StartY=-10 StartZ=0 EndX=103.603 EndY=-10 EndZ=0
    g3: LineSegment StartX=103.603 StartY=-10 StartZ=0 EndX=103.603 EndY=0 EndZ=0
  constraints (12):
    c: Coincident(g0,g1)
    c: Coincident(g1,g2)
    c: Coincident(g2,g3)
    c: Coincident(g3,g0)
    c: Horizontal(g0)
    c: Horizontal(g2)
    c: Vertical(g1)
    c: Vertical(g3)
    c: PointOnObject(g1,g-3)
    c: DistanceX(g2,g2) = 17
    c: DistanceY(g3,g3) = 10
    c: PointOnObject(g0,g-1)
FEATURE [PartDesign::Pad] Pad001
  BaseFeature = -> Pad
  Direction = (0,0,-1)
  Length = 25
  Length2 = 10
  Profile = -> Sketch001
  ReferenceAxis = -> Sketch001 [N_Axis]
  Type = 0
FEATURE [Sketcher::SketchObject] Sketch002
  ExternalGeometry = -> [Pad001]
  FullyConstrained = true
  MapMode = 5
  Placement = pos=(0,0,-25) rot=(1,0,0;3.14159rad)
  Support = -> [Pad001]
  sketch-geometry (4):
    g0: LineSegment StartX=103.603 StartY=-10 StartZ=0 EndX=73.6025 EndY=-10 EndZ=0
    g1: LineSegment StartX=73.6025 StartY=-10 StartZ=0 EndX=73.6025 EndY=50 EndZ=0
    g2: LineSegment StartX=73.6025 StartY=50 StartZ=0 EndX=103.603 EndY=50 EndZ=0
    g3: LineSegment StartX=103.603 StartY=50 StartZ=0 EndX=103.603 EndY=-10 EndZ=0
  constraints (11):
    c: Coincident(g0,g1)
    c: Coincident(g2,g3)
    c: Coincident(g3,g0)
    c: Horizontal(g0)
    c: Vertical(g3)
    c: Coincident(g0,g-4)
    c: Coincident(g2,g1)
    c: Horizontal(g2)
    c: Horizontal(g2,g-6)
    c: Vertical(g1)
    c: DistanceX(g0,g0) = 30
FEATURE [PartDesign::Pad] Pad002
  BaseFeature = -> Pad001
  Direction = (0,0,-1)
  Length = 8
  Length2 = 10
  Profile = -> Sketch002
  ReferenceAxis = -> Sketch002 [N_Axis]
  Type = 0
FEATURE [Sketcher::SketchObject] Sketch003
  ExternalGeometry = -> [Pad002]
  FullyConstrained = true
  MapMode = 5
  Placement = pos=(0,0,-25) rot=(0,0,1;0rad)
  Support = -> [Pad002]
  sketch-geometry (6):
    g0: LineSegment StartX=76.1025 StartY=-8 StartZ=0 EndX=89.1025 EndY=-8 EndZ=0
    g1: LineSegment StartX=89.1025 StartY=-8 StartZ=0 EndX=89.1025 EndY=-32 EndZ=0
    g2: LineSegment StartX=89.1025 StartY=-32 StartZ=0 EndX=76.1025 EndY=-32 EndZ=0
    g3: LineSegment StartX=76.1025 StartY=-32 StartZ=0 EndX=76.1025 EndY=-8 EndZ=0
    g4: GeomPoint X=82.6025 Y=-20 Z=0
    g5: GeomPoint X=88.6025 Y=-20 Z=0
  constraints (14):
    c: Coincident(g0,g1)
    c: Coincident(g1,g2)
    c: Coincident(g2,g3)
    c: Coincident(g3,g0)
    c: Horizontal(g0)
    c: Horizontal(g2)
    c: Vertical(g1)
    c: Vertical(g3)
    c: DistanceY(g1,g1) = 24
    c: DistanceX(g2,g2) = 13
    c: Symmetric(g1,g0,g4)
    c: Symmetric(g-5,g-3,g5)
    c: DistanceX(g4,g5) = 6
    c: Horizontal(g5,g4)
FEATURE [PartDesign::Pocket] Pocket
  BaseFeature = -> Pad002
  Direction = (0,0,-1)
  Length = 19
  Length2 = 5
  Profile = -> Sketch003
  ReferenceAxis = -> Sketch003 [N_Axis]
  Type = 1
FEATURE [Sketcher::SketchObject] Sketch004
  ExternalGeometry = -> [Pocket]
  FullyConstrained = false
  MapMode = 5
  Placement = pos=(0,0,-25) rot=(0,0,1;0rad)
  Support = -> [Pocket]
  sketch-geometry (5):
    g0: GeomPoint X=82.6025 Y=-6.3796 Z=0
    g1: GeomPoint X=82.6025 Y=-33.3796 Z=0
    g2: Circle CenterX=82.6025 CenterY=-6.3796 CenterZ=0 NormalX=0 NormalY=0 NormalZ=1 AngleXU=0 Radius=1
    g3: Circle CenterX=82.6025 CenterY=-33.3796 CenterZ=0 NormalX=0 NormalY=0 NormalZ=1 AngleXU=0 Radius=1
    g4: GeomPoint X=82.6025 Y=-20 Z=0
  constraints (8):
    c: DistanceY(g1,g0) = 27
    c: Coincident(g2,g0)
    c: Coincident(g3,g1)
    c: Equal(g3,g2)
    c: Diameter(g2) = 2
    c: Symmetric(g-6,g-5,g4)
    c: Vertical(g2,g3)
    c: Vertical(g3,g4)
FEATURE [PartDesign::Hole] Hole
  BaseFeature = -> Pocket
  CustomThreadClearance = 0
  Depth = 25
  DepthType = 0
  Diameter = 1.6
  DrillForDepth = false
  DrillPoint = 1
  DrillPointAngle = 118
  HoleCutCountersinkAngle = 90
  HoleCutCustomValues = false
  HoleCutDepth = 0
  HoleCutDiameter = 6.1
  HoleCutType = 0
  ModelThread = false
  Profile = -> Sketch004
  Tapered = false
  TaperedAngle = 90
  ThreadClass = 0
  ThreadDepth = 25
  ThreadDepthType = 0
  ThreadDirection = 0
  ThreadFit = 0
  ThreadSize = 6
  ThreadType = 1
  Threaded = true
  UseCustomThreadClearance = false
FEATURE [PartDesign::CoordinateSystem] LCS_1
  AttacherType = Attacher::AttachEngine3D
  MapMode = 45
  Placement = pos=(82.6025,-6.3796,-25) rot=(0,0,1;0rad)
  Support = -> [Hole]
FEATURE [PartDesign::CoordinateSystem] LCS_2  label="LCS_origin"
  AttacherType = Attacher::AttachEngine3D
FEATURE [PartDesign::Chamfer] Chamfer
  Angle = 45
  Base = -> Hole [Edge4]
  BaseFeature = -> Hole
  ChamferType = 0
  FlipDirection = false
  Size = 16
  Size2 = 1
  SupportTransform = false
  UseAllEdges = false
FEATURE [PartDesign::Chamfer] Chamfer001
  Angle = 45
  Base = -> Chamfer [Edge12,Edge49]
  BaseFeature = -> Chamfer
  ChamferType = 0
  FlipDirection = false
  Size = 3
  Size2 = 1
  SupportTransform = false
  UseAllEdges = false
FEATURE [Sketcher::SketchObject] Sketch005
  ExternalGeometry = -> [Chamfer001]
  FullyConstrained = true
  MapMode = 5
  Placement = pos=(0,0,0) rot=(1,0,0;3.14159rad)
  Support = -> [Chamfer001]
  sketch-geometry (8):
    g0: LineSegment StartX=86.6025 StartY=-10 StartZ=0 EndX=86.6025 EndY=-50 EndZ=0
    g1: LineSegment StartX=86.6025 StartY=-50 StartZ=0 EndX=0 EndY=-100 EndZ=0
    g2: LineSegment StartX=0 StartY=-100 StartZ=0 EndX=-86.6025 EndY=-50 EndZ=0
    g3: LineSegment StartX=-86.6025 StartY=-50 StartZ=0 EndX=-87.4686 EndY=-50.5 EndZ=0
    g4: LineSegment StartX=-87.4686 StartY=-50.5 StartZ=0 EndX=-1.42e-14 EndY=-101 EndZ=0
    g5: LineSegment StartX=-1.42e-14 StartY=-101 StartZ=0 EndX=87.4686 EndY=-50.5 EndZ=0
    g6: LineSegment StartX=87.4686 StartY=-50.5 StartZ=0 EndX=87.4686 EndY=-10 EndZ=0
    g7: LineSegment StartX=87.4686 StartY=-10 StartZ=0 EndX=86.6025 EndY=-10 EndZ=0
  constraints (16):
    c: Coincident(g-7,g0)
    c: Coincident(g0,g-7)
    c: Coincident(g0,g1)
    c: Coincident(g1,g-4)
    c: Coincident(g1,g2)
    c: Coincident(g2,g-3)
    c: Coincident(g2,g3)
    c: Coincident(g3,g-5)
    c: Coincident(g3,g4)
    c: Coincident(g4,g-6)
    c: Coincident(g4,g5)
    c: Coincident(g5,g-8)
    c: Coincident(g5,g6)
    c: Coincident(g6,g-8)
    c: Coincident(g6,g7)
    c: Coincident(g7,g0)
FEATURE [PartDesign::Pad] Pad003
  BaseFeature = -> Chamfer001
  Direction = (0,0,-1)
  Length = 12
  Length2 = 10
  Profile = -> Sketch005
  ReferenceAxis = -> Sketch005 [N_Axis]
  Type = 0
FEATURE [Sketcher::SketchObject] Sketch006
  ExternalGeometry = -> [Pad003]
  FullyConstrained = true
  MapMode = 5
  Placement = pos=(0,0,-12) rot=(1,0,0;3.14159rad)
  Support = -> [Pad003]
  sketch-geometry (17):
    g0: LineSegment StartX=87.4686 StartY=-10 StartZ=0 EndX=77.4686 EndY=-10 EndZ=0
    g1: LineSegment StartX=77.4686 StartY=-44.7265 StartZ=0 EndX=77.4686 EndY=-10 EndZ=0
    g2: LineSegment StartX=-77.4686 StartY=44.7265 StartZ=0 EndX=-77.4686 EndY=-44.7265 EndZ=0
    g3: LineSegment StartX=-77.4686 StartY=-44.7265 StartZ=0 EndX=1.42e-14 EndY=-89.453 EndZ=0
    g4: LineSegment StartX=1.42e-14 StartY=-89.453 StartZ=0 EndX=77.4686 EndY=-44.7265 EndZ=0
    g5: Circle CenterX=0 CenterY=0 CenterZ=0 NormalX=0 NormalY=0 NormalZ=1 AngleXU=0 Radius=89.453
    g6: LineSegment StartX=87.4686 StartY=-10 StartZ=0 EndX=87.4686 EndY=-50.5 EndZ=0
    g7: LineSegment StartX=87.4686 StartY=-50.5 StartZ=0 EndX=0 EndY=-101 EndZ=0
    g8: LineSegment StartX=0 StartY=-101 StartZ=0 EndX=-87.4686 EndY=-50.5 EndZ=0
    g9: LineSegment StartX=-87.4686 StartY=-50.5 StartZ=0 EndX=-87.4686 EndY=50.5 EndZ=0
    g10: LineSegment StartX=-87.4686 StartY=50.5 StartZ=0 EndX=1.42e-14 EndY=101 EndZ=0
    g11: LineSegment StartX=1.42e-14 StartY=101 StartZ=0 EndX=90 EndY=101 EndZ=0
    g12: LineSegment StartX=90 StartY=101 StartZ=0 EndX=172.942 EndY=53.1132 EndZ=0
    g13: LineSegment StartX=-77.4686 StartY=44.7265 StartZ=0 EndX=0 EndY=89.453 EndZ=0
    g14: LineSegment StartX=0 StartY=89.453 StartZ=0 EndX=90 EndY=89.453 EndZ=0
    g15: LineSegment StartX=90 StartY=89.453 StartZ=0 EndX=167.942 EndY=44.453 EndZ=0
    g16: LineSegment StartX=172.942 StartY=53.1132 StartZ=0 EndX=167.942 EndY=44.453 EndZ=0
  constraints (44):
    c: Coincident(g-3,g0)
    c: Horizontal(g0)
    c: DistanceX(g0,g0) = 10
    c: Coincident(g2,g3)
    c: Coincident(g3,g4)
    c: Coincident(g4,g1)
    c: PointOnObject(g2,g5)
    c: PointOnObject(g2,g5)
    c: PointOnObject(g3,g5)
    c: PointOnObject(g4,g5)
    c: Coincident(g5,g-1)
    c: Vertical(g1)
    c: Coincident(g6,g0)
    c: Coincident(g6,g-4)
    c: Coincident(g7,g6)
    c: Coincident(g7,g-5)
    c: Coincident(g8,g7)
    c: Coincident(g8,g-6)
    c: Coincident(g9,g8)
    c: Coincident(g9,g-6)
    c: Coincident(g1,g0)
    c: Parallel(g-8,g4)
    c: Parallel(g3,g-9)
    c: Vertical(g2)
    c: DistanceX(g8,g2) = 10
    c: Coincident(g10,g9)
    c: Coincident(g10,g-11)
    c: Coincident(g11,g10)
    c: Horizontal(g11)
    c: Coincident(g12,g11)
    c: Parallel(g12,g3)
    c: Coincident(g13,g2)
    c: PointOnObject(g13,g5)
    c: Parallel(g13,g10)
    c: Coincident(g14,g13)
    c: Horizontal(g14)
    c: Vertical(g14,g11)
    c: DistanceX(g14,g14) = 90
    c: Coincident(g15,g14)
    c: Coincident(g16,g12)
    c: Coincident(g16,g15)
    c: Parallel(g15,g12)
    c: Perpendicular(g12,g16)
    c: Distance(g15) = 90
FEATURE [PartDesign::Pad] Pad004
  BaseFeature = -> Pad003
  Direction = (0,0,-1)
  Length = 5
  Length2 = 10
  Profile = -> Sketch006
  ReferenceAxis = -> Sketch006 [N_Axis]
  Type = 0
FEATURE [Sketcher::SketchObject] Sketch007
  ExternalGeometry = -> [Pad004]
  FullyConstrained = true
  MapMode = 5
  Placement = pos=(43.7343,-75.75,0) rot=(0.935113,0.250563,0.250563;1.63783rad)
  Support = -> [Pad004]
  sketch-geometry (5):
    g0: LineSegment StartX=-30 StartY=130 StartZ=0 EndX=30 EndY=130 EndZ=0
    g1: LineSegment StartX=30 StartY=130 StartZ=0 EndX=30 EndY=60 EndZ=0
    g2: LineSegment StartX=30 StartY=60 StartZ=0 EndX=-30 EndY=60 EndZ=0
    g3: LineSegment StartX=-30 StartY=60 StartZ=0 EndX=-30 EndY=130 EndZ=0
    g4: GeomPoint X=0 Y=130 Z=0
  constraints (13):
    c: Coincident(g0,g1)
    c: Coincident(g1,g2)
    c: Coincident(g2,g3)
    c: Coincident(g3,g0)
    c: Horizontal(g0)
    c: Horizontal(g2)
    c: Vertical(g1)
    c: Vertical(g3)
    c: PointOnObject(g4,g-2)
    c: Symmetric(g0,g0,g4)
    c: DistanceX(g0,g0) = 60
    c: DistanceY(g0,g-3) = 20
    c: DistanceY(g1,g1) = 70
FEATURE [PartDesign::Pad] Pad005
  BaseFeature = -> Pad004
  Direction = (0.5,-0.866025,0)
  Length = 30
  Length2 = 10
  Profile = -> Sketch007
  ReferenceAxis = -> Sketch007 [N_Axis]
  Type = 0
FEATURE [Sketcher::SketchObject] Sketch008
  ExternalGeometry = -> [Pad005]
  FullyConstrained = true
  MapMode = 5
  Placement = pos=(43.3013,-75,0) rot=(-0.186157,0.694747,0.694747;3.50969rad)
  Support = -> [Pad005]
  sketch-geometry (4):
    g0: LineSegment StartX=-25 StartY=58 StartZ=0 EndX=25 EndY=58 EndZ=0
    g1: LineSegment StartX=25 StartY=58 StartZ=0 EndX=25 EndY=132 EndZ=0
    g2: LineSegment StartX=25 StartY=132 StartZ=0 EndX=-25 EndY=132 EndZ=0
    g3: LineSegment StartX=-25 StartY=132 StartZ=0 EndX=-25 EndY=58 EndZ=0
  constraints (12):
    c: Coincident(g0,g1)
    c: Coincident(g1,g2)
    c: Coincident(g2,g3)
    c: Coincident(g3,g0)
    c: Horizontal(g0)
    c: Horizontal(g2)
    c: Vertical(g1)
    c: Vertical(g3)
    c: DistanceY(g-4,g1) = 2
    c: DistanceX(g1,g-4) = 5
    c: DistanceX(g-5,g2) = 5
    c: DistanceY(g0,g-6) = 2
FEATURE [PartDesign::Pocket] Pocket001
  BaseFeature = -> Pad005
  Direction = (0.5,-0.866025,-1e-16)
  Length = 5
  Length2 = 5
  Profile = -> Sketch008
  ReferenceAxis = -> Sketch008 [N_Axis]
  Type = 1
FEATURE [Sketcher::SketchObject] Sketch009
  ExternalGeometry = -> [Pocket001]
  FullyConstrained = true
  MapMode = 5
  Placement = pos=(25.9808,15,0) rot=(0.377964,0.654654,0.654654;2.41886rad)
  Support = -> [Pocket001]
  sketch-geometry (2):
    g0: Circle CenterX=-102.469 CenterY=110 CenterZ=0 NormalX=0 NormalY=0 NormalZ=1 AngleXU=0 Radius=3
    g1: GeomPoint X=-102.469 Y=130 Z=0
  constraints (4):
    c: Diameter(g0) = 6
    c: Symmetric(g-3,g-4,g1)
    c: Vertical(g1,g0)
    c: DistanceY(g0,g1) = 20
FEATURE [PartDesign::Hole] Hole001
  BaseFeature = -> Pocket001
  CustomThreadClearance = 0
  Depth = 25
  DepthType = 0
  Diameter = 2.5
  DrillForDepth = false
  DrillPoint = 1
  DrillPointAngle = 118
  HoleCutCountersinkAngle = 90
  HoleCutCustomValues = false
  HoleCutDepth = 0
  HoleCutDiameter = 6.1
  HoleCutType = 2
  ModelThread = false
  Profile = -> Sketch009
  Tapered = false
  TaperedAngle = 90
  ThreadClass = 0
  ThreadDepth = 25
  ThreadDepthType = 0
  ThreadDirection = 0
  ThreadFit = 0
  ThreadSize = 9
  ThreadType = 1
  Threaded = true
  UseCustomThreadClearance = false
FEATURE [PartDesign::CoordinateSystem] LCS_cam
  AttacherType = Attacher::AttachEngine3D
  AttachmentOffset = pos=(0,0,0) rot=(-0.766044,-0.642788,0;3.14159rad)
  MapMode = 45
  Placement = pos=(72.8849,-76.2404,110) rot=(0.754536,-0.528332,-0.389282;1.75037rad)
  Support = -> [Hole001]
FEATURE [Sketcher::SketchObject] Sketch010
  FullyConstrained = true
  MapMode = 5
  Placement = pos=(-43.7343,75.75,0) rot=(-0.186157,0.694747,0.694747;3.50969rad)
  Support = -> [Hole001]
  sketch-geometry (5):
    g0: LineSegment StartX=10 StartY=56 StartZ=0 EndX=10 EndY=36 EndZ=0
    g1: LineSegment StartX=10 StartY=36 StartZ=0 EndX=-10 EndY=36 EndZ=0
    g2: LineSegment StartX=-10 StartY=36 StartZ=0 EndX=-10 EndY=56 EndZ=0
    g3: LineSegment StartX=-10 StartY=56 StartZ=0 EndX=10 EndY=56 EndZ=0
    g4: GeomPoint X=0 Y=46 Z=0
  constraints (13):
    c: Coincident(g0,g1)
    c: Coincident(g1,g2)
    c: Coincident(g2,g3)
    c: Coincident(g3,g0)
    c: Horizontal(g1)
    c: Horizontal(g3)
    c: Vertical(g0)
    c: Vertical(g2)
    c: Symmetric(g1,g0,g4)
    c: PointOnObject(g4,g-2)
    c: DistanceX(g1,g1) = 20
    c: DistanceY(g0,g0) = 20
    c: DistanceY(g-1,g0) = 36
FEATURE [PartDesign::Pad] Pad006
  BaseFeature = -> Hole001
  Direction = (-0.5,0.866025,1e-16)
  Length = 90
  Length2 = 10
  Profile = -> Sketch010
  ReferenceAxis = -> Sketch010 [N_Axis]
  Type = 0
FEATURE [Sketcher::SketchObject] Sketch011
  ExternalGeometry = -> [Pad006]
  FullyConstrained = true
  MapMode = 5
  Placement = pos=(2.2e-15,-3.6e-15,36) rot=(1,0,0;3.14159rad)
  Support = -> [Pad006]
  sketch-geometry (4):
    g0: LineSegment StartX=-97.3945 StartY=-148.692 StartZ=0 EndX=-87.3945 EndY=-131.372 EndZ=0
    g1: LineSegment StartX=-87.3945 StartY=-131.372 StartZ=0 EndX=-70.074 EndY=-141.372 EndZ=0
    g2: LineSegment StartX=-70.074 StartY=-141.372 StartZ=0 EndX=-80.074 EndY=-158.692 EndZ=0
    g3: LineSegment StartX=-80.074 StartY=-158.692 StartZ=0 EndX=-97.3945 EndY=-148.692 EndZ=0
  constraints (10):
    c: Coincident(g-5,g0)
    c: PointOnObject(g0,g-4)
    c: Coincident(g0,g1)
    c: PointOnObject(g1,g-3)
    c: Coincident(g1,g2)
    c: Coincident(g2,g-5)
    c: Coincident(g2,g3)
    c: Coincident(g3,g0)
    c: Perpendicular(g2,g1)
    c: Equal(g2,g3)
FEATURE [PartDesign::Pad] Pad007
  BaseFeature = -> Pad006
  Direction = (-1e-16,1e-16,-1)
  Length = 40
  Length2 = 10
  Profile = -> Sketch011
  ReferenceAxis = -> Sketch011 [N_Axis]
  Type = 0
FEATURE [Sketcher::SketchObject] Sketch012
  ExternalGeometry = -> [Pad007]
  FullyConstrained = true
  MapMode = 5
  Placement = pos=(-7e-16,1.2e-15,-4) rot=(1,0,0;3.14159rad)
  Support = -> [Pad007]
  sketch-geometry (1):
    g0: Circle CenterX=-83.7343 CenterY=-145.032 CenterZ=0 NormalX=0 NormalY=0 NormalZ=1 AngleXU=0 Radius=3
  constraints (2):
    c: Diameter(g0) = 6
    c: Symmetric(g-5,g-6,g0)
FEATURE [PartDesign::Pocket] Pocket002
  BaseFeature = -> Pad007
  Direction = (2e-16,-3e-16,1)
  Length = 20
  Length2 = 5
  Profile = -> Sketch012
  ReferenceAxis = -> Sketch012 [N_Axis]
  Type = 0
FEATURE [PartDesign::Chamfer] Chamfer002
  Angle = 45
  Base = -> Pocket002 [Edge200,Edge207,Edge209,Edge205]
  BaseFeature = -> Pocket002
  ChamferType = 0
  FlipDirection = false
  Size = 4
  Size2 = 1
  SupportTransform = false
  UseAllEdges = false
FEATURE [PartDesign::CoordinateSystem] LCS_forRod
  AttacherType = Attacher::AttachEngine3D
  AttachmentOffset = pos=(0,0,0) rot=(0,0,1;0.523599rad)
  MapMode = 45
  Placement = pos=(-83.7343,145.032,16) rot=(0,0,1;0.523648rad)
  Support = -> [Chamfer002]
FEATURE [Sketcher::SketchObject] Sketch013
  FullyConstrained = true
  MapMode = 5
  Placement = pos=(-43.7343,-75.75,0) rot=(0.935113,-0.250563,-0.250563;1.63783rad)
  Support = -> [Chamfer002]
  sketch-geometry (5):
    g0: LineSegment StartX=10 StartY=46 StartZ=0 EndX=10 EndY=26 EndZ=0
    g1: LineSegment StartX=10 StartY=26 StartZ=0 EndX=-10 EndY=26 EndZ=0
    g2: LineSegment StartX=-10 StartY=26 StartZ=0 EndX=-10 EndY=46 EndZ=0
    g3: LineSegment StartX=-10 StartY=46 StartZ=0 EndX=10 EndY=46 EndZ=0
    g4: GeomPoint X=0 Y=36 Z=0
  constraints (13):
    c: Coincident(g0,g1)
    c: Coincident(g1,g2)
    c: Coincident(g2,g3)
    c: Coincident(g3,g0)
    c: Horizontal(g1)
    c: Horizontal(g3)
    c: Vertical(g0)
    c: Vertical(g2)
    c: Symmetric(g1,g0,g4)
    c: PointOnObject(g4,g-2)
    c: DistanceY(g0,g0) = 20
    c: Equal(g3,g0)
    c: DistanceY(g-1,g4) = 36
FEATURE [PartDesign::Pad] Pad008
  BaseFeature = -> Chamfer002
  Direction = (-0.5,-0.866025,-1e-16)
  Length = 200
  Length2 = 10
  Profile = -> Sketch013
  ReferenceAxis = -> Sketch013 [N_Axis]
  Type = 0
FEATURE [Sketcher::SketchObject] Sketch014
  ExternalGeometry = -> [Pad008]
  FullyConstrained = true
  MapMode = 5
  Placement = pos=(-1.6e-15,-2.6e-15,26) rot=(1,0,0;3.14159rad)
  Support = -> [Pad008]
  sketch-geometry (4):
    g0: LineSegment StartX=-152.395 StartY=243.955 StartZ=0 EndX=-135.074 EndY=253.955 EndZ=0
    g1: LineSegment StartX=-135.074 StartY=253.955 StartZ=0 EndX=-125.074 EndY=236.635 EndZ=0
    g2: LineSegment StartX=-125.074 StartY=236.635 StartZ=0 EndX=-142.395 EndY=226.635 EndZ=0
    g3: LineSegment StartX=-142.395 StartY=226.635 StartZ=0 EndX=-152.395 EndY=243.955 EndZ=0
  constraints (10):
    c: Coincident(g-4,g0)
    c: Coincident(g0,g-5)
    c: Coincident(g0,g1)
    c: PointOnObject(g1,g-5)
    c: Coincident(g1,g2)
    c: PointOnObject(g2,g-4)
    c: Coincident(g2,g3)
    c: Coincident(g3,g0)
    c: Perpendicular(g1,g2)
    c: Equal(g1,g0)
FEATURE [PartDesign::Pad] Pad009
  BaseFeature = -> Pad008
  Direction = (1e-16,1e-16,-1)
  Length = 430
  Length2 = 10
  Profile = -> Sketch014
  ReferenceAxis = -> Sketch014 [N_Axis]
  Type = 0
FEATURE [Sketcher::SketchObject] Sketch015
  FullyConstrained = true
  MapMode = 5
  Placement = pos=(87.4686,0,0) rot=(0.57735,0.57735,0.57735;2.0944rad)
  Support = -> [Pad009]
  sketch-geometry (5):
    g0: LineSegment StartX=-10 StartY=46 StartZ=0 EndX=-10 EndY=26 EndZ=0
    g1: LineSegment StartX=-10 StartY=26 StartZ=0 EndX=10 EndY=26 EndZ=0
    g2: LineSegment StartX=10 StartY=26 StartZ=0 EndX=10 EndY=46 EndZ=0
    g3: LineSegment StartX=10 StartY=46 StartZ=0 EndX=-10 EndY=46 EndZ=0
    g4: GeomPoint X=0 Y=36 Z=0
  constraints (13):
    c: Coincident(g0,g1)
    c: Coincident(g1,g2)
    c: Coincident(g2,g3)
    c: Coincident(g3,g0)
    c: Horizontal(g1)
    c: Horizontal(g3)
    c: Vertical(g0)
    c: Vertical(g2)
    c: Symmetric(g1,g0,g4)
    c: PointOnObject(g4,g-2)
    c: DistanceY(g2,g2) = 20
    c: Equal(g3,g2)
    c: DistanceY(g-1,g4) = 36
FEATURE [PartDesign::Pad] Pad010
  BaseFeature = -> Pad009
  Direction = (1,0,0)
  Length = 200
  Length2 = 10
  Profile = -> Sketch015
  ReferenceAxis = -> Sketch015 [N_Axis]
  Type = 0
FEATURE [Sketcher::SketchObject] Sketch016
  ExternalGeometry = -> [Pad010]
  FullyConstrained = true
  MapMode = 5
  Placement = pos=(0,0,26) rot=(1,0,0;3.14159rad)
  Support = -> [Pad010]
  sketch-geometry (4):
    g0: LineSegment StartX=287.469 StartY=10 StartZ=0 EndX=287.469 EndY=-10 EndZ=0
    g1: LineSegment StartX=287.469 StartY=-10 StartZ=0 EndX=267.469 EndY=-10 EndZ=0
    g2: LineSegment StartX=267.469 StartY=-10 StartZ=0 EndX=267.469 EndY=10 EndZ=0
    g3: LineSegment StartX=267.469 StartY=10 StartZ=0 EndX=287.469 EndY=10 EndZ=0
  constraints (10):
    c: Coincident(g-4,g0)
    c: Coincident(g0,g-5)
    c: Coincident(g0,g1)
    c: PointOnObject(g1,g-5)
    c: Coincident(g1,g2)
    c: PointOnObject(g2,g-4)
    c: Vertical(g2)
    c: Coincident(g2,g3)
    c: Coincident(g3,g0)
    c: Equal(g0,g3)
FEATURE [PartDesign::Pad] Pad011
  BaseFeature = -> Pad010
  Direction = (0,0,-1)
  Length = 430
  Length2 = 10
  Profile = -> Sketch016
  ReferenceAxis = -> Sketch016 [N_Axis]
  Type = 0
FEATURE [PartDesign::Chamfer] Chamfer003
  Angle = 45
  Base = -> Pad011 [Edge134,Edge132,Edge133,Edge138,Edge226,Edge137,Edge141,Edge231,Edge183,Edge176,Edge181,Edge244,Edge179,Edge184,Edge250]
  BaseFeature = -> Pad011
  ChamferType = 0
  FlipDirection = false
  Size = 3
  Size2 = 1
  SupportTransform = false
  UseAllEdges = false
FEATURE [PartDesign::CoordinateSystem] LCS_fall
  AttacherType = Attacher::AttachEngine3D
  AttachmentOffset = pos=(67,600,0) rot=(0,0,1;0rad)
  MapMode = 45
  Placement = pos=(9.80127,-16.9763,600) rot=(0.377964,0.654654,0.654654;2.41886rad)
  Support = -> [Chamfer003]
FEATURE [PartDesign::Body] Body  label="ImageRecogBox-body"
  Group = -> [Sketch,Pad,Sketch001,Pad001,Sketch002,Pad002,Sketch003,Pocket,Sketch004,Hole,LCS_1,LCS_2,Chamfer,Chamfer001,Sketch005,Pad003,Sketch006,Pad004,Sketch007,Pad005,Sketch008,Pocket001,Sketch009,Hole001,LCS_cam,Sketch010,Pad006,Sketch011,Pad007,Sketch012,Pocket002,Chamfer002,LCS_forRod,Sketch013,Pad008,Sketch014,Pad009,Sketch015,Pad010,Sketch016,Pad011,Chamfer003,LCS_fall]
  Origin = -> Origin
  Tip = -> Chamfer003
---- part MG90S_servo_refined.FCStd = doc fcstd_32f2eeedc879 ----
FCSTD DOCUMENT  (FreeCAD 0.20R29177 +426 (Git))
Label: MG90S_servo_refined
License: All rights reserved
LicenseURL: http://en.wikipedia.org/wiki/All_rights_reserved
objects: App::MeasureDistance×9, PartDesign::CoordinateSystem×2, Mesh::Feature×1, Part::Feature×1, Part::Refine×1, PartDesign::FeatureBase×1, Sketcher::SketchObject×1, PartDesign::Body×1
note: 7 computed .brp shape members not serialized (recipe doc carries the construction recipe); baked Part::Feature solids carry a one-line shape summary decoded from their .brp

FEATURE [Mesh::Feature] ImageToStl_com_MG90S  label="ImageToStl.com_MG90S"
FEATURE [Part::Feature] ImageToStl_com_MG90S001
  shape: bbox 33 x 32.4 x 12.2 mm, 2058 faces, 0 solids (baked)
FEATURE [Part::Refine] ImageToStl_com_MG90S001001
  Source = -> ImageToStl_com_MG90S001
FEATURE [App::MeasureDistance] Distance  label="Distance: 4,98 mm"
  Distance = 4.981
  P1 = (466.695,752.809,1601.93)
  P2 = (461.739,752.809,1601.42)
FEATURE [App::MeasureDistance] Distance001  label="Distance: 2,10 mm"
  Distance = 2.10355
  P1 = (466.695,752.809,1597.49)
  P2 = (464.591,752.809,1597.49)
FEATURE [App::MeasureDistance] Distance002  label="Distance: 3,08 mm"
  Distance = 3.07833
  P1 = (466.695,752.809,1595.55)
  P2 = (463.617,752.809,1595.61)
FEATURE [App::MeasureDistance] Distance003  label="Distance: 17,99 mm"
  Distance = 17.9941
  P1 = (461.695,752.809,1603.09)
  P2 = (461.695,734.815,1603.09)
FEATURE [App::MeasureDistance] Distance004  label="Distance: 12,20 mm"
  Distance = 12.2
  P1 = (461.695,734.809,1603.09)
  P2 = (461.695,734.809,1590.89)
FEATURE [App::MeasureDistance] Distance005  label="Distance: 22,96 mm"
  Distance = 22.963
  P1 = (438.732,734.809,1590.94)
  P2 = (461.695,734.809,1590.89)
FEATURE [App::MeasureDistance] Distance006  label="Distance: 1,85 mm"
  Distance = 1.84541
  P1 = (461.786,752.809,1595.51)
  P2 = (463.631,752.809,1595.56)
FEATURE [App::MeasureDistance] Distance007  label="Distance: 1,97 mm"
  Distance = 1.96716
  P1 = (461.782,752.809,1594.87)
  P2 = (463.745,752.809,1594.75)
FEATURE [App::MeasureDistance] Distance008  label="Distance: 2,48 mm"
  Distance = 2.48096
  P1 = (462.797,755.29,1603.09)
  P2 = (462.745,752.809,1603.09)
FEATURE [PartDesign::FeatureBase] BaseFeature
  BaseFeature = -> ImageToStl_com_MG90S001001
FEATURE [PartDesign::CoordinateSystem] LCS_1
  AttacherType = Attacher::AttachEngine3D
  AttachmentOffset = pos=(1,0,0) rot=(0,0,1;0rad)
  MapMode = 45
  Placement = pos=(463.698,752.809,1596.99) rot=(0,0,1;0rad)
  Support = -> [BaseFeature]
FEATURE [PartDesign::CoordinateSystem] LCS_2
  AttacherType = Attacher::AttachEngine3D
  MapMode = 45
  Placement = pos=(444.795,767.209,1596.99) rot=(-1,0,0;1.5708rad)
  Support = -> [BaseFeature]
FEATURE [Sketcher::SketchObject] Sketch
  ExternalGeometry = -> [BaseFeature]
  FullyConstrained = false
  MapMode = 5
  Placement = pos=(0,752.809,0) rot=(1,0,0;1.5708rad)
  Support = -> [BaseFeature]
  sketch-geometry (3):
    g0: GeomPoint X=462.698 Y=1596.99 Z=0
    g1: GeomPoint X=463.698 Y=1596.99 Z=0
    g2: Circle CenterX=463.698 CenterY=1596.99 CenterZ=0 NormalX=0 NormalY=0 NormalZ=1 AngleXU=0 Radius=1.15
  constraints (3):
    c: Symmetric(g-3,g-3,g0)
    c: Coincident(g2,g1)
    c: Diameter(g2) = 2.3
FEATURE [PartDesign::Body] Body
  BaseFeature = -> ImageToStl_com_MG90S001001
  Group = -> [BaseFeature,LCS_1,LCS_2,Sketch]
  Origin = -> Origin
  Tip = -> BaseFeature
---- part Main_Rod.FCStd = doc fcstd_1ec1eb526770 ----
FCSTD DOCUMENT  (FreeCAD 0.20R29177 +426 (Git))
Label: Main_Rod
License: All rights reserved
LicenseURL: http://en.wikipedia.org/wiki/All_rights_reserved
objects: PartDesign::CoordinateSystem×4, Sketcher::SketchObject×3, PartDesign::Pad×3, PartDesign::Body×1
note: 14 computed .brp shape members not serialized (recipe doc carries the construction recipe); baked Part::Feature solids carry a one-line shape summary decoded from their .brp

FEATURE [Sketcher::SketchObject] Sketch019
  FullyConstrained = true
  MapMode = 5
  sketch-geometry (1):
    g0: Circle CenterX=0 CenterY=0 CenterZ=0 NormalX=0 NormalY=0 NormalZ=1 AngleXU=0 Radius=6
  constraints (2):
    c: Coincident(g0,g-1)
    c: Diameter(g0) = 12
FEATURE [PartDesign::Pad] Pad010
  Direction = (0,0,1)
  Length = 400
  Length2 = 10
  Profile = -> Sketch019
  ReferenceAxis = -> Sketch019 [N_Axis]
  Refine = true
  Reversed = true
  Type = 0
FEATURE [Sketcher::SketchObject] Sketch071
  AttachmentOffset = pos=(0,0,-270) rot=(0,0,1;0rad)
  FullyConstrained = true
  MapMode = 5
  Placement = pos=(0,0,-270) rot=(0,0,1;0rad)
  Support = -> [Pad010]
  sketch-geometry (1):
    g0: Circle CenterX=0 CenterY=0 CenterZ=0 NormalX=0 NormalY=0 NormalZ=1 AngleXU=0 Radius=12.5
  constraints (2):
    c: Coincident(g0,g-1)
    c: Diameter(g0) = 25
FEATURE [PartDesign::Pad] Pad
  BaseFeature = -> Pad010
  Direction = (0,0,1)
  Length = 1
  Length2 = 10
  Profile = -> Sketch071
  ReferenceAxis = -> Sketch071 [N_Axis]
  Type = 0
FEATURE [Sketcher::SketchObject] Sketch
  AttachmentOffset = pos=(0,0,-140) rot=(0,0,1;0rad)
  FullyConstrained = true
  MapMode = 5
  Placement = pos=(0,0,-140) rot=(0,0,1;0rad)
  Support = -> [Pad]
  sketch-geometry (1):
    g0: Circle CenterX=0 CenterY=0 CenterZ=0 NormalX=0 NormalY=0 NormalZ=1 AngleXU=0 Radius=12.5
  constraints (2):
    c: Coincident(g0,g-1)
    c: Diameter(g0) = 25
FEATURE [PartDesign::Pad] Pad011
  BaseFeature = -> Pad
  Direction = (0,0,1)
  Length = 1
  Length2 = 10
  Profile = -> Sketch
  ReferenceAxis = -> Sketch [N_Axis]
  Type = 0
FEATURE [PartDesign::CoordinateSystem] LCS_1
  AttacherType = Attacher::AttachEngine3D
  MapMode = 45
  Placement = pos=(9e-16,-4e-16,-400) rot=(0,0,1;0rad)
  Support = -> [Pad011]
FEATURE [PartDesign::CoordinateSystem] LCS_mid  label="LCS_mid_lower"
  AttacherType = Attacher::AttachEngine3D
  MapMode = 45
  Placement = pos=(3.6e-15,-1.4e-15,-270) rot=(0,0,1;0rad)
  Support = -> [Pad011]
FEATURE [PartDesign::CoordinateSystem] LCS_mid_upper
  AttacherType = Attacher::AttachEngine3D
  MapMode = 45
  Placement = pos=(3.6e-15,-1.4e-15,-140) rot=(0,0,1;0rad)
  Support = -> [Pad011]
FEATURE [PartDesign::CoordinateSystem] LCS_ImageRecogBox
  AttacherType = Attacher::AttachEngine3D
  MapMode = 45
  Placement = pos=(9e-16,-4e-16,0) rot=(0,0,1;0rad)
  Support = -> [Pad011]
FEATURE [PartDesign::Body] Body007  label="Rod"
  Group = -> [Sketch019,Pad010,Sketch071,Pad,Sketch,Pad011,LCS_1,LCS_mid,LCS_mid_upper,LCS_ImageRecogBox]
  Origin = -> Origin007
  Placement = pos=(3,54.9,405.8) rot=(0,0,1;0rad)
  Tip = -> Pad011
---- part PortalRotatorSketch.FCStd = doc fcstd_fcd322103c07 ----
FCSTD DOCUMENT  (FreeCAD 0.20R29177 +426 (Git))
Label: PortalRotatorSketch
License: All rights reserved
LicenseURL: http://en.wikipedia.org/wiki/All_rights_reserved
objects: PartDesign::CoordinateSystem×2, Sketcher::SketchObject×1, PartDesign::Body×1
note: 4 computed .brp shape members not serialized (recipe doc carries the construction recipe); baked Part::Feature solids carry a one-line shape summary decoded from their .brp
EXTERNAL_REF file=assembly4.FCStd obj=Variables

FEATURE [PartDesign::CoordinateSystem] LCS_Origin
  AttacherType = Attacher::AttachEngine3D
  MapMode = 2
  Support = -> [X_Axis]
FEATURE [Sketcher::SketchObject] Sketch
  FullyConstrained = true
  MapMode = 5
  Support = -> [XY_Plane]
  expr: Constraints[0] = assembly4#Variables.PortalRotatorDeg
  sketch-geometry (1):
    g0: LineSegment StartX=0 StartY=0 StartZ=0 EndX=6.8404 EndY=18.7939 EndZ=0
  constraints (3):
    c: Angle(g0,g-1) = -1.22173
    c: Coincident(g0,g-1)
    c: Distance(g0) = 20
FEATURE [PartDesign::CoordinateSystem] LCSRotator
  AttacherType = Attacher::AttachEngine3D
  MapMode = 7
  Placement = pos=(0,0,0) rot=(0.970288,-0.171088,-0.171088;1.60095rad)
  Support = -> [Sketch]
FEATURE [PartDesign::Body] PortalRotatorBody
  Group = -> [LCS_Origin,Sketch,LCSRotator]
  Origin = -> Origin
---- part banana.FCStd = doc fcstd_84346e96579b ----
FCSTD DOCUMENT  (FreeCAD 0.20R29177 +426 (Git))
Label: banana
License: All rights reserved
LicenseURL: http://en.wikipedia.org/wiki/All_rights_reserved
objects: Part::Feature×2, Mesh::Feature×1, Part::Refine×1, PartDesign::FeatureBase×1, PartDesign::CoordinateSystem×1, PartDesign::Body×1
note: 6 computed .brp shape members not serialized (recipe doc carries the construction recipe); baked Part::Feature solids carry a one-line shape summary decoded from their .brp

FEATURE [Mesh::Feature] banana
FEATURE [Part::Feature] banana001
  shape: bbox 86 x 98 x 13 mm, 400 faces, 0 solids (baked)
FEATURE [Part::Refine] banana001001
  Source = -> banana001
FEATURE [Part::Feature] banana001001_solid  label="banana001001 (Solid)"
  shape: bbox 86 x 98 x 13 mm, 284 faces (baked)
FEATURE [PartDesign::FeatureBase] BaseFeature
  BaseFeature = -> banana001001_solid
FEATURE [PartDesign::CoordinateSystem] LCS_1
  AttacherType = Attacher::AttachEngine3D
FEATURE [PartDesign::Body] Body  label="Banana_Body"
  BaseFeature = -> banana001001_solid
  Group = -> [BaseFeature,LCS_1]
  Origin = -> Origin
  Tip = -> BaseFeature
---- part belt.FCStd = doc fcstd_626cba47067e ----
FCSTD DOCUMENT  (FreeCAD 0.20R29177 +426 (Git))
Label: belt
License: All rights reserved
LicenseURL: http://en.wikipedia.org/wiki/All_rights_reserved
objects: PartDesign::CoordinateSystem×2, Sketcher::SketchObject×1, PartDesign::Pad×1, PartDesign::Body×1
note: 6 computed .brp shape members not serialized (recipe doc carries the construction recipe); baked Part::Feature solids carry a one-line shape summary decoded from their .brp

FEATURE [Sketcher::SketchObject] Sketch
  FullyConstrained = false
  MapMode = 5
  Support = -> [XY_Plane]
  sketch-geometry (8):
    g0: ArcOfCircle CenterX=-31.4005 CenterY=0 CenterZ=0 NormalX=0 NormalY=0 NormalZ=1 AngleXU=0 Radius=21.5 StartAngle=1.54731 EndAngle=4.73588
    g1: ArcOfCircle CenterX=53.7587 CenterY=0 CenterZ=0 NormalX=0 NormalY=0 NormalZ=1 AngleXU=0 Radius=19.5 StartAngle=4.73588 EndAngle=7.83049
    g2: LineSegment StartX=-30.8955 StartY=21.4941 StartZ=0 EndX=54.2167 EndY=19.4946 EndZ=0
    g3: LineSegment StartX=-30.8955 StartY=-21.4941 StartZ=0 EndX=54.2167 EndY=-19.4946 EndZ=0
    g4: ArcOfCircle CenterX=-31.4005 CenterY=0 CenterZ=0 NormalX=0 NormalY=0 NormalZ=1 AngleXU=0 Radius=22 StartAngle=1.54731 EndAngle=4.73588
    g5: ArcOfCircle CenterX=53.7587 CenterY=0 CenterZ=0 NormalX=0 NormalY=0 NormalZ=1 AngleXU=0 Radius=20 StartAngle=4.73588 EndAngle=7.83049
    g6: LineSegment StartX=-30.8838 StartY=21.9939 StartZ=0 EndX=54.2284 EndY=19.9945 EndZ=0
    g7: LineSegment StartX=-30.8838 StartY=-21.9939 StartZ=0 EndX=54.2284 EndY=-19.9945 EndZ=0
  constraints (16):
    c: PointOnObject(g0,g-1)
    c: Diameter(g0) = 43
    c: PointOnObject(g1,g-1)
    c: Diameter(g1) = 39
    c: Tangent(g0,g3) = -1.5708
    c: Tangent(g0,g2) = 1.5708
    c: Tangent(g1,g2) = 1.5708
    c: Tangent(g1,g3) = -1.5708
    c: Diameter(g4) = 44
    c: Diameter(g5) = 40
    c: Tangent(g4,g7) = -1.5708
    c: Tangent(g4,g6) = 1.5708
    c: Tangent(g5,g6) = 1.5708
    c: Tangent(g5,g7) = -1.5708
    c: Coincident(g4,g0)
    c: Coincident(g5,g1)
FEATURE [PartDesign::Pad] Pad
  Direction = (0,0,1)
  Length = 6
  Length2 = 10
  Profile = -> Sketch
  ReferenceAxis = -> Sketch [N_Axis]
  Type = 0
FEATURE [PartDesign::CoordinateSystem] LCS_gear60
  AttacherType = Attacher::AttachEngine3D
  MapMode = 12
  Placement = pos=(53.7587,-3.3e-15,6) rot=(0.58639,-0.572777,-0.572777;2.08089rad)
  Support = -> [Pad]
FEATURE [PartDesign::CoordinateSystem] LCS_gear66
  AttacherType = Attacher::AttachEngine3D
  AttachmentOffset = pos=(0,-5,0) rot=(0,0,1;0rad)
  MapMode = 12
  Placement = pos=(-31.4005,4.1e-15,1) rot=(0.58639,0.572777,0.572777;2.08089rad)
  Support = -> [Pad]
FEATURE [PartDesign::Body] Body  label="belt_Body"
  Group = -> [Sketch,Pad,LCS_gear60,LCS_gear66]
  Origin = -> Origin
  Tip = -> Pad
---- part classifier_middle_verPartial3.FCStd = doc fcstd_8c34b2b6bfdd ----
FCSTD DOCUMENT  (FreeCAD 0.20R29177 +426 (Git))
Label: classifier_middle_verPartial3
License: All rights reserved
LicenseURL: https://en.wikipedia.org/wiki/All_rights_reserved
objects: Sketcher::SketchObject×11, PartDesign::Pad×3, PartDesign::Pocket×3, PartDesign::CoordinateSystem×3, PartDesign::Hole×3, PartDesign::Body×1
note: 33 computed .brp shape members not serialized (recipe doc carries the construction recipe); baked Part::Feature solids carry a one-line shape summary decoded from their .brp

FEATURE [Sketcher::SketchObject] Sketch
  FullyConstrained = false
  MapMode = 5
  Support = -> [XY_Plane]
  sketch-geometry (40):
    g0: LineSegment StartX=84.6025 StartY=1.1547 StartZ=0 EndX=0 EndY=50 EndZ=0
    g1: LineSegment StartX=0 StartY=50 StartZ=0 EndX=-86.6025 EndY=-1.42e-14 EndZ=0
    g2: Circle CenterX=-2.18504 CenterY=-45.0607 CenterZ=0 NormalX=0 NormalY=0 NormalZ=1 AngleXU=0 Radius=95.0858
    g3: LineSegment StartX=87.6025 StartY=1.73205 StartZ=0 EndX=69.282 EndY=12.3094 EndZ=0
    g4: LineSegment StartX=0 StartY=52.3094 StartZ=0 EndX=-17.8205 EndY=42.0207 EndZ=0
    g5: Circle CenterX=-2.18504 CenterY=-45.0607 CenterZ=0 NormalX=0 NormalY=0 NormalZ=1 AngleXU=0 Radius=97.3946
    g6: GeomPoint X=-43.8013 Y=27.0207 Z=0
    g7: LineSegment StartX=-69.782 StartY=12.0207 StartZ=0 EndX=-75.782 EndY=22.413 EndZ=0
    g8: LineSegment StartX=-75.782 StartY=22.413 StartZ=0 EndX=-23.8205 EndY=52.413 EndZ=0
    g9: LineSegment StartX=-23.8205 StartY=52.413 StartZ=0 EndX=-17.8205 EndY=42.0207 EndZ=0
    g10: LineSegment StartX=-71.684 StartY=21.315 StartZ=0 EndX=-69.684 EndY=17.8509 EndZ=0
    g11: LineSegment StartX=-69.684 StartY=17.8509 StartZ=0 EndX=-22.6865 EndY=44.4489 EndZ=0
    g12: LineSegment StartX=-22.6865 StartY=44.4489 StartZ=0 EndX=-24.6865 EndY=47.913 EndZ=0
    g13: LineSegment StartX=-24.6865 StartY=47.913 StartZ=0 EndX=-71.684 EndY=21.315 EndZ=0
    g14: LineSegment StartX=-23.8205 StartY=52.413 StartZ=0 EndX=-22.0885 EndY=49.413 EndZ=0
    g15: LineSegment StartX=-26.4186 StartY=50.913 StartZ=0 EndX=-24.6865 EndY=47.913 EndZ=0
    g16: LineSegment StartX=-24.6865 StartY=47.913 StartZ=0 EndX=-22.0885 EndY=49.413 EndZ=0
    g17: LineSegment StartX=-23.8205 StartY=52.413 StartZ=0 EndX=-26.4186 EndY=50.913 EndZ=0
    g18: LineSegment StartX=-71.684 StartY=21.315 StartZ=0 EndX=-73.184 EndY=23.913 EndZ=0
    g19: LineSegment StartX=-71.684 StartY=21.315 StartZ=0 EndX=-74.282 EndY=19.815 EndZ=0
    g20: LineSegment StartX=75.282 StartY=22.7017 StartZ=0 EndX=69.282 EndY=12.3094 EndZ=0
    g21: LineSegment StartX=23.3205 StartY=52.7017 StartZ=0 EndX=75.282 EndY=22.7017 EndZ=0
    g22: LineSegment StartX=72.684 StartY=24.2017 StartZ=0 EndX=71.184 EndY=21.6036 EndZ=0
    g23: LineSegment StartX=71.184 StartY=21.6036 StartZ=0 EndX=73.782 EndY=20.1036 EndZ=0
    g24: LineSegment StartX=69.184 StartY=18.1395 StartZ=0 EndX=71.184 EndY=21.6036 EndZ=0
    g25: LineSegment StartX=71.184 StartY=21.6036 StartZ=0 EndX=24.4186 EndY=48.6036 EndZ=0
    g26: LineSegment StartX=22.4186 StartY=45.1395 StartZ=0 EndX=69.184 EndY=18.1395 EndZ=0
    g27: LineSegment StartX=24.4186 StartY=48.6036 StartZ=0 EndX=22.4186 EndY=45.1395 EndZ=0
    g28: LineSegment StartX=24.4186 StartY=48.6036 StartZ=0 EndX=25.9186 EndY=51.2017 EndZ=0
    g29: LineSegment StartX=24.4186 StartY=48.6036 StartZ=0 EndX=21.8205 EndY=50.1036 EndZ=0
    g30: LineSegment StartX=17.3205 StartY=42.3094 StartZ=0 EndX=23.3205 EndY=52.7017 EndZ=0
    g31: LineSegment StartX=17.3205 StartY=42.3094 StartZ=0 EndX=0 EndY=52.3094 EndZ=0
    g32: LineSegment StartX=86.6025 StartY=0 StartZ=0 EndX=86.6025 EndY=-15 EndZ=0
    g33: LineSegment StartX=86.6025 StartY=-15 StartZ=0 EndX=84.6025 EndY=-15 EndZ=0
    g34: LineSegment StartX=84.6025 StartY=-15 StartZ=0 EndX=84.6025 EndY=1.1547 EndZ=0
    g35: LineSegment StartX=-86.6025 StartY=0 StartZ=0 EndX=-87.6025 EndY=1.73205 EndZ=0
    g36: LineSegment StartX=-87.6025 StartY=1.73205 StartZ=0 EndX=-69.782 EndY=12.0207 EndZ=0
    g37: LineSegment StartX=84.6025 StartY=1.1547 StartZ=0 EndX=86.6025 EndY=0 EndZ=0
    g38: LineSegment StartX=87.6025 StartY=1.73205 StartZ=0 EndX=86.6025 EndY=0 EndZ=0
    g39: LineSegment StartX=0 StartY=50 StartZ=0 EndX=1 EndY=51.7321 EndZ=0
  constraints (114):
    c: PointOnObject(g0,g2)
    c: Coincident(g31,g4)
    c: PointOnObject(g31,g5)
    c: PointOnObject(g31,g-2)
    c: Parallel(g1,g4)
    c: Coincident(g2,g5)
    c: Coincident(g7,g8)
    c: Coincident(g8,g9)
    c: Parallel(g7,g9)
    c: Distance(g9) = 12
    c: Equal(g7,g9)
    c: Distance(g8) = 60
    c: Symmetric(g9,g7,g6)
    c: Coincident(g10,g11)
    c: Coincident(g11,g12)
    c: Coincident(g13,g10)
    c: Parallel(g12,g10)
    c: Parallel(g10,g7)
    c: Parallel(g11,g13)
    c: Coincident(g14,g8)
    c: PointOnObject(g15,g8)
    c: Coincident(g15,g12)
    c: Equal(g15,g14)
    c: Coincident(g13,g12)
    c: Parallel(g15,g14)
    c: DistanceY(g14,g14) = 3
    c: Coincident(g16,g12)
    c: Coincident(g16,g14)
    c: Coincident(g17,g8)
    c: Distance(g17) = 3
    c: Equal(g16,g17)
    c: Parallel(g17,g16)
    c: PointOnObject(g16,g9)
    c: Coincident(g18,g10)
    c: PointOnObject(g18,g8)
    c: Coincident(g19,g10)
    c: PointOnObject(g19,g7)
    c: Parallel(g18,g7)
    c: Parallel(g8,g19)
    c: Distance(g18) = 3
    c: Distance(g19) = 3
    c: Distance(g12) = 4
    c: Coincident(g30,g21)
    c: Coincident(g21,g20)
    c: Parallel(g30,g20)
    c: Distance(g20) = 12
    c: Equal(g30,g20)
    c: Distance(g21) = 60
    c: Coincident(g27,g26)
    c: Coincident(g26,g24)
    c: Coincident(g25,g27)
    c: Parallel(g24,g27)
    c: Parallel(g27,g30)
    c: Parallel(g26,g25)
    c: PointOnObject(g22,g21)
    c: Coincident(g22,g24)
    c: Coincident(g25,g24)
    c: Coincident(g23,g24)
    c: PointOnObject(g23,g20)
    c: Coincident(g28,g27)
    c: PointOnObject(g28,g21)
    c: Coincident(g29,g27)
    c: PointOnObject(g29,g30)
    c: Parallel(g28,g30)
    c: Parallel(g21,g29)
    c: Distance(g28) = 3
    c: Distance(g29) = 3
    c: Distance(g24) = 4
    c: Parallel(g23,g21)
    c: Parallel(g22,g20)
    c: Parallel(g25,g21)
    c: Equal(g23,g29)
    c: Vertical(g32)
    c: Coincident(g33,g32)
    c: Horizontal(g33)
    c: Coincident(g34,g33)
    c: Vertical(g34)
    c: Coincident(g0,g34)
    c: Distance(g31) = 20
    c: Distance(g32,g0) = 100
    c: Perpendicular(g8,g9)
    c: Coincident(g35,g1)
    c: Distance(g35) = 2
    c: Perpendicular(g35,g1)
    c: PointOnObject(g35,g5)
    c: Coincident(g4,g9)
    c: Coincident(g36,g35)
    c: Coincident(g36,g7)
    c: Perpendicular(g35,g36)
    c: Equal(g4,g36)
    c: Coincident(g37,g0)
    c: Coincident(g38,g3)
    c: Coincident(g38,g37)
    c: Distance(g38) = 2
    c: Perpendicular(g3,g20)
    c: Coincident(g3,g20)
    c: Parallel(g37,g3)
    c: Parallel(g0,g31)
    c: Coincident(g30,g31)
    c: Coincident(g0,g1)
    c: PointOnObject(g0,g-2)
    c: Perpendicular(g24,g25)
    c: PointOnObject(g38,g-1)
    c: Perpendicular(g37,g38)
    c: Coincident(g39,g0)
    c: PointOnObject(g39,g31)
    c: Perpendicular(g39,g0)
    c: Distance(g39) = 2
    c: Angle(g-2,g0) = 1.0472
    c: Coincident(g32,g38)
    c: PointOnObject(g1,g-1)
    c: Distance(g1) = 100
    c: DistanceX(g33,g33) = 2
    c: DistanceY(g32,g32) = 15
FEATURE [PartDesign::Pad] Pad
  Direction = (0,0,1)
  Length = 150
  Length2 = 10
  Profile = -> Sketch
  ReferenceAxis = -> Sketch [N_Axis]
  Refine = true
  Type = 0
FEATURE [Sketcher::SketchObject] Sketch001
  ExternalGeometry = -> [Pad]
  FullyConstrained = false
  MapMode = 5
  Placement = pos=(84.6025,0,0) rot=(0.57735,-0.57735,-0.57735;2.0944rad)
  Support = -> [Pad]
  sketch-geometry (8):
    g0: LineSegment StartX=31.3251 StartY=0 StartZ=0 EndX=-1.1547 EndY=0 EndZ=0
    g1: LineSegment StartX=-1.1547 StartY=0 StartZ=0 EndX=-1.1547 EndY=60 EndZ=0
    g2: LineSegment StartX=-1.1547 StartY=60 StartZ=0 EndX=31.3251 EndY=60 EndZ=0
    g3: LineSegment StartX=31.3251 StartY=60 StartZ=0 EndX=31.3251 EndY=0 EndZ=0
    g4: LineSegment StartX=-1.1547 StartY=150 StartZ=0 EndX=35.4561 EndY=150 EndZ=0
    g5: LineSegment StartX=35.4561 StartY=150 StartZ=0 EndX=35.4561 EndY=90 EndZ=0
    g6: LineSegment StartX=35.4561 StartY=90 StartZ=0 EndX=-1.1547 EndY=90 EndZ=0
    g7: LineSegment StartX=-1.1547 StartY=90 StartZ=0 EndX=-1.1547 EndY=150 EndZ=0
  constraints (21):
    c: Coincident(g0,g1)
    c: Coincident(g1,g2)
    c: Coincident(g2,g3)
    c: Coincident(g3,g0)
    c: Horizontal(g0)
    c: Horizontal(g2)
    c: Vertical(g1)
    c: Vertical(g3)
    c: PointOnObject(g0,g-1)
    c: PointOnObject(g1,g-6)
    c: DistanceY(g3,g3) = 60
    c: Coincident(g4,g5)
    c: Coincident(g5,g6)
    c: Coincident(g6,g7)
    c: Coincident(g7,g4)
    c: Horizontal(g4)
    c: Horizontal(g6)
    c: Vertical(g5)
    c: Vertical(g7)
    c: Coincident(g4,g-6)
    c: DistanceY(g5,g5) = 60
FEATURE [PartDesign::Pocket] Pocket
  BaseFeature = -> Pad
  Direction = (1,0,0)
  Length = 5
  Length2 = 5
  Profile = -> Sketch001
  ReferenceAxis = -> Sketch001 [N_Axis]
  Type = 0
FEATURE [PartDesign::CoordinateSystem] LCS_1
  AttacherType = Attacher::AttachEngine3D
  AttachmentOffset = pos=(0,0,75) rot=(0,0,1;2.0944rad)
  MapMode = 45
  Placement = pos=(0,50,150) rot=(0,0,1;2.0944rad)
  Support = -> [Pocket]
FEATURE [Sketcher::SketchObject] Sketch002
  ExternalGeometry = -> [Pocket]
  FullyConstrained = true
  MapMode = 5
  Placement = pos=(86.6025,0,0) rot=(0.57735,0.57735,0.57735;2.0944rad)
  Support = -> [Pocket]
  sketch-geometry (3):
    g0: Circle CenterX=-7.5 CenterY=80 CenterZ=0 NormalX=0 NormalY=0 NormalZ=1 AngleXU=0 Radius=3
    g1: Circle CenterX=-7.5 CenterY=70 CenterZ=0 NormalX=0 NormalY=0 NormalZ=1 AngleXU=0 Radius=3
    g2: GeomPoint X=-7.5 Y=75 Z=0
  constraints (9):
    c: Symmetric(g-3,g-4,g2)
    c: Symmetric(g0,g1,g2)
    c: DistanceY(g-4,g1) = 10
    c: Equal(g1,g0)
    c: Diameter(g0) = 6
    c: Vertical(g1,g0)
    c: DistanceX(g1,g-4) = 7.5
    c: DistanceY(g-1,g1) = 70
    c: DistanceY(g1,g0) = 10
FEATURE [Sketcher::SketchObject] Sketch003
  ExternalGeometry = -> [Pocket]
  FullyConstrained = true
  MapMode = 5
  Placement = pos=(-22.6506,39.2321,0) rot=(-0.186157,0.694747,0.694747;3.50969rad)
  Support = -> [Pocket]
  sketch-geometry (2):
    g0: Circle CenterX=67.5 CenterY=80 CenterZ=0 NormalX=0 NormalY=0 NormalZ=1 AngleXU=0 Radius=3
    g1: Circle CenterX=67.5 CenterY=70 CenterZ=0 NormalX=0 NormalY=0 NormalZ=1 AngleXU=0 Radius=3
  constraints (6):
    c: Equal(g0,g1)
    c: Diameter(g0) = 6
    c: Vertical(g0,g1)
    c: DistanceX(g1,g-4) = 7.5
    c: DistanceY(g-4,g1) = 70
    c: DistanceY(g1,g0) = 10
FEATURE [Sketcher::SketchObject] Sketch004
  ExternalGeometry = -> [Pocket]
  FullyConstrained = true
  MapMode = 5
  Placement = pos=(-21.6506,37.5,0) rot=(0.935113,0.250563,0.250563;1.63783rad)
  Support = -> [Pocket]
  sketch-geometry (7):
    g0: GeomPoint X=-67.5 Y=70 Z=0
    g1: GeomPoint X=-67.5 Y=80 Z=0
    g2: GeomPoint X=-67.5 Y=75 Z=0
    g3: LineSegment StartX=-72.5 StartY=85 StartZ=0 EndX=-62.5 EndY=85 EndZ=0
    g4: LineSegment StartX=-62.5 StartY=85 StartZ=0 EndX=-62.5 EndY=65 EndZ=0
    g5: LineSegment StartX=-62.5 StartY=65 StartZ=0 EndX=-72.5 EndY=65 EndZ=0
    g6: LineSegment StartX=-72.5 StartY=65 StartZ=0 EndX=-72.5 EndY=85 EndZ=0
  constraints (16):
    c: Vertical(g0,g1)
    c: DistanceY(g0,g1) = 10
    c: DistanceY(g-1,g0) = 70
    c: Symmetric(g1,g0,g2)
    c: DistanceX(g-3,g2) = 7.5
    c: Coincident(g3,g4)
    c: Coincident(g4,g5)
    c: Coincident(g5,g6)
    c: Coincident(g6,g3)
    c: Horizontal(g3)
    c: Horizontal(g5)
    c: Vertical(g4)
    c: Vertical(g6)
    c: Symmetric(g4,g3,g2)
    c: DistanceY(g4,g4) = 20
    c: DistanceX(g3,g3) = 10
FEATURE [Sketcher::SketchObject] Sketch005
  ExternalGeometry = -> [Pocket]
  FullyConstrained = false
  MapMode = 5
  Placement = pos=(28.6506,49.6244,0) rot=(0.186157,0.694747,0.694747;2.77349rad)
  Support = -> [Pocket]
  sketch-geometry (8):
    g0: LineSegment StartX=-63.2639 StartY=150 StartZ=0 EndX=17.1472 EndY=150 EndZ=0
    g1: LineSegment StartX=17.1472 StartY=150 StartZ=0 EndX=17.1472 EndY=125 EndZ=0
    g2: LineSegment StartX=17.1472 StartY=125 StartZ=0 EndX=-63.2639 EndY=125 EndZ=0
    g3: LineSegment StartX=-63.2639 StartY=125 StartZ=0 EndX=-63.2639 EndY=150 EndZ=0
    g4: LineSegment StartX=-62.0783 StartY=25 StartZ=0 EndX=16.1272 EndY=25 EndZ=0
    g5: LineSegment StartX=16.1272 StartY=25 StartZ=0 EndX=16.1272 EndY=0 EndZ=0
    g6: LineSegment StartX=16.1272 StartY=0 StartZ=0 EndX=-62.0783 EndY=0 EndZ=0
    g7: LineSegment StartX=-62.0783 StartY=0 StartZ=0 EndX=-62.0783 EndY=25 EndZ=0
  constraints (20):
    c: Coincident(g0,g1)
    c: Coincident(g1,g2)
    c: Coincident(g2,g3)
    c: Coincident(g3,g0)
    c: Horizontal(g0)
    c: Horizontal(g2)
    c: Vertical(g1)
    c: Vertical(g3)
    c: Coincident(g4,g5)
    c: Coincident(g5,g6)
    c: Coincident(g6,g7)
    c: Coincident(g7,g4)
    c: Horizontal(g4)
    c: Horizontal(g6)
    c: Vertical(g5)
    c: Vertical(g7)
    c: Horizontal(g-3,g0)
    c: DistanceY(g1,g1) = 25
    c: DistanceY(g5,g5) = 25
    c: Horizontal(g5,g-1)
FEATURE [Sketcher::SketchObject] Sketch006
  ExternalGeometry = -> [Pocket]
  FullyConstrained = false
  MapMode = 5
  Placement = pos=(-28.6506,49.6244,0) rot=(-0.186157,0.694747,0.694747;3.50969rad)
  Support = -> [Pocket]
  sketch-geometry (8):
    g0: LineSegment StartX=-12.5353 StartY=150 StartZ=0 EndX=61.9692 EndY=150 EndZ=0
    g1: LineSegment StartX=61.9692 StartY=150 StartZ=0 EndX=61.9692 EndY=125 EndZ=0
    g2: LineSegment StartX=61.9692 StartY=125 StartZ=0 EndX=-12.5353 EndY=125 EndZ=0
    g3: LineSegment StartX=-12.5353 StartY=125 StartZ=0 EndX=-12.5353 EndY=150 EndZ=0
    g4: LineSegment StartX=-12.3717 StartY=25 StartZ=0 EndX=60.4768 EndY=25 EndZ=0
    g5: LineSegment StartX=60.4768 StartY=25 StartZ=0 EndX=60.4768 EndY=0 EndZ=0
    g6: LineSegment StartX=60.4768 StartY=0 StartZ=0 EndX=-12.3717 EndY=0 EndZ=0
    g7: LineSegment StartX=-12.3717 StartY=0 StartZ=0 EndX=-12.3717 EndY=25 EndZ=0
  constraints (20):
    c: Coincident(g0,g1)
    c: Coincident(g1,g2)
    c: Coincident(g2,g3)
    c: Coincident(g3,g0)
    c: Horizontal(g0)
    c: Horizontal(g2)
    c: Vertical(g1)
    c: Vertical(g3)
    c: Coincident(g4,g5)
    c: Coincident(g5,g6)
    c: Coincident(g6,g7)
    c: Coincident(g7,g4)
    c: Horizontal(g4)
    c: Horizontal(g6)
    c: Vertical(g5)
    c: Vertical(g7)
    c: Equal(g5,g1)
    c: DistanceY(g1,g1) = 25
    c: Horizontal(g-1,g5)
    c: Horizontal(g0,g-3)
FEATURE [Sketcher::SketchObject] Sketch007
  ExternalGeometry = -> [Pocket]
  FullyConstrained = true
  MapMode = 5
  Placement = pos=(84.6025,0,0) rot=(0.57735,-0.57735,-0.57735;2.0944rad)
  Support = -> [Pocket]
  sketch-geometry (5):
    g0: LineSegment StartX=1.92265 StartY=85 StartZ=0 EndX=11.9226 EndY=85 EndZ=0
    g1: LineSegment StartX=11.9226 StartY=85 StartZ=0 EndX=11.9226 EndY=65 EndZ=0
    g2: LineSegment StartX=11.9226 StartY=65 StartZ=0 EndX=1.92265 EndY=65 EndZ=0
    g3: LineSegment StartX=1.92265 StartY=65 StartZ=0 EndX=1.92265 EndY=85 EndZ=0
    g4: GeomPoint X=6.92265 Y=75 Z=0
  constraints (12):
    c: Coincident(g0,g1)
    c: Coincident(g1,g2)
    c: Coincident(g2,g3)
    c: Coincident(g3,g0)
    c: Horizontal(g0)
    c: Horizontal(g2)
    c: Vertical(g1)
    c: Vertical(g3)
    c: Symmetric(g-3,g-4,g4)
    c: Symmetric(g0,g2,g4)
    c: DistanceY(g1,g1) = 20
    c: DistanceX(g0,g0) = 10
FEATURE [Sketcher::SketchObject] Sketch009
  ExternalGeometry = -> [Pocket]
  FullyConstrained = true
  MapMode = 5
  Placement = pos=(21.6506,37.5,0) rot=(0.935113,-0.250563,-0.250563;1.63783rad)
  Support = -> [Pocket]
  expr: Constraints[1] = Sketch008.Constraints[1]
  expr: Constraints[4] = Sketch008.Constraints[3]
  expr: Constraints[5] = Sketch008.Constraints[4]
  sketch-geometry (7):
    g0: Circle CenterX=23.8453 CenterY=145 CenterZ=0 NormalX=0 NormalY=0 NormalZ=1 AngleXU=0 Radius=3
    g1: Circle CenterX=23.8453 CenterY=15 CenterZ=0 NormalX=0 NormalY=0 NormalZ=1 AngleXU=0 Radius=3
    g2: GeomPoint X=23.8453 Y=150 Z=0
    g3: LineSegment StartX=-10 StartY=21.5 StartZ=0 EndX=57.6906 EndY=21.5 EndZ=0
    g4: LineSegment StartX=57.6906 StartY=21.5 StartZ=0 EndX=57.6906 EndY=20.5 EndZ=0
    g5: LineSegment StartX=57.6906 StartY=20.5 StartZ=0 EndX=-10 EndY=20.5 EndZ=0
    g6: LineSegment StartX=-10 StartY=20.5 StartZ=0 EndX=-10 EndY=21.5 EndZ=0
  constraints (19):
    c: Equal(g0,g1)
    c: Diameter(g0) = 6
    c: Symmetric(g-3,g-3,g2)
    c: Vertical(g2,g0)
    c: DistanceY(g0,g2) = 5
    c: DistanceY(g-1,g1) = 15
    c: Vertical(g1,g2)
    c: Coincident(g3,g4)
    c: Coincident(g4,g5)
    c: Coincident(g5,g6)
    c: Coincident(g6,g3)
    c: Horizontal(g3)
    c: Horizontal(g5)
    c: Vertical(g4)
    c: Vertical(g6)
    c: DistanceX(g3,g-4) = 15
    c: DistanceX(g-5,g3) = 15
    c: DistanceY(g1,g4) = 5.5
    c: DistanceY(g4,g4) = 1
FEATURE [PartDesign::Pad] Pad001
  BaseFeature = -> Pocket
  Direction = (-1,0,0)
  Length = 10
  Length2 = 10
  Profile = -> Sketch007
  ReferenceAxis = -> Sketch007 [N_Axis]
  Type = 0
FEATURE [PartDesign::Hole] Hole
  BaseFeature = -> Pad001
  CustomThreadClearance = 0
  Depth = 25
  DepthType = 0
  Diameter = 2.5
  DrillForDepth = false
  DrillPoint = 1
  DrillPointAngle = 118
  HoleCutCountersinkAngle = 90
  HoleCutCustomValues = false
  HoleCutDepth = 0
  HoleCutDiameter = 6.1
  HoleCutType = 0
  ModelThread = false
  Profile = -> Sketch002
  Tapered = false
  TaperedAngle = 90
  ThreadClass = 0
  ThreadDepth = 25
  ThreadDepthType = 0
  ThreadDirection = 0
  ThreadFit = 0
  ThreadSize = 9
  ThreadType = 1
  Threaded = true
  UseCustomThreadClearance = false
FEATURE [PartDesign::Hole] Hole001
  BaseFeature = -> Hole
  CustomThreadClearance = 0
  Depth = 25
  DepthType = 0
  Diameter = 2.5
  DrillForDepth = false
  DrillPoint = 1
  DrillPointAngle = 118
  HoleCutCountersinkAngle = 90
  HoleCutCustomValues = false
  HoleCutDepth = 0
  HoleCutDiameter = 6.1
  HoleCutType = 2
  ModelThread = false
  Profile = -> Sketch003
  Tapered = false
  TaperedAngle = 90
  ThreadClass = 0
  ThreadDepth = 25
  ThreadDepthType = 0
  ThreadDirection = 0
  ThreadFit = 0
  ThreadSize = 9
  ThreadType = 1
  Threaded = true
  UseCustomThreadClearance = false
FEATURE [PartDesign::Pocket] Pocket001
  BaseFeature = -> Hole001
  Direction = (0.5,-0.866025,-1e-16)
  Length = 11
  Length2 = 5
  Profile = -> Sketch006
  ReferenceAxis = -> Sketch006 [N_Axis]
  Type = 0
FEATURE [PartDesign::Pocket] Pocket002
  BaseFeature = -> Pocket001
  Direction = (-0.5,-0.866025,0)
  Length = 11
  Length2 = 5
  Profile = -> Sketch005
  ReferenceAxis = -> Sketch005 [N_Axis]
  Type = 0
FEATURE [PartDesign::Pad] Pad002
  BaseFeature = -> Pocket002
  Direction = (-0.5,-0.866025,0)
  Length = 10
  Length2 = 10
  Profile = -> Sketch009
  ReferenceAxis = -> Sketch009 [N_Axis]
  Type = 0
FEATURE [Sketcher::SketchObject] Sketch008
  ExternalGeometry = -> [Pocket]
  FullyConstrained = true
  MapMode = 5
  Placement = pos=(23.1506,40.0981,-9e-16) rot=(0.186157,0.694747,0.694747;2.77349rad)
  Support = -> [Pocket002]
  sketch-geometry (3):
    g0: Circle CenterX=-23.8453 CenterY=145 CenterZ=0 NormalX=0 NormalY=0 NormalZ=1 AngleXU=0 Radius=3
    g1: Circle CenterX=-23.8453 CenterY=15 CenterZ=0 NormalX=0 NormalY=0 NormalZ=1 AngleXU=0 Radius=3
    g2: GeomPoint X=-23.8453 Y=150 Z=0
  constraints (7):
    c: Equal(g0,g1)
    c: Diameter(g0) = 6
    c: Vertical(g2,g0)
    c: DistanceY(g0,g2) = 5
    c: DistanceY(g-1,g1) = 15
    c: Vertical(g1,g2)
    c: Symmetric(g-4,g-3,g2)
FEATURE [Sketcher::SketchObject] Sketch010
  ExternalGeometry = -> [Pad002]
  FullyConstrained = true
  MapMode = 5
  Placement = pos=(-23.1506,40.0981,8.8e-15) rot=(-0.186157,0.694747,0.694747;3.50969rad)
  Support = -> [Pad002]
  sketch-geometry (3):
    g0: Circle CenterX=24.9226 CenterY=145 CenterZ=0 NormalX=0 NormalY=0 NormalZ=1 AngleXU=0 Radius=3
    g1: Circle CenterX=24.9226 CenterY=15 CenterZ=0 NormalX=0 NormalY=0 NormalZ=1 AngleXU=0 Radius=3
    g2: GeomPoint X=24.4226 Y=150 Z=0
  constraints (7):
    c: Equal(g0,g1)
    c: Diameter(g0) = 6
    c: Symmetric(g-3,g-4,g2)
    c: DistanceY(g0,g2) = 5
    c: DistanceY(g-1,g1) = 15
    c: Vertical(g0,g1)
    c: DistanceX(g2,g0) = 0.5
FEATURE [PartDesign::Hole] Hole002
  BaseFeature = -> Pad002
  CustomThreadClearance = 0
  Depth = 25
  DepthType = 0
  Diameter = 2.5
  DrillForDepth = false
  DrillPoint = 1
  DrillPointAngle = 118
  HoleCutCountersinkAngle = 90
  HoleCutCustomValues = false
  HoleCutDepth = 0
  HoleCutDiameter = 6.1
  HoleCutType = 2
  ModelThread = false
  Profile = -> Sketch010
  Tapered = false
  TaperedAngle = 90
  ThreadClass = 0
  ThreadDepth = 25
  ThreadDepthType = 0
  ThreadDirection = 0
  ThreadFit = 0
  ThreadSize = 9
  ThreadType = 1
  Threaded = true
  UseCustomThreadClearance = false
FEATURE [PartDesign::CoordinateSystem] LCS_2
  AttacherType = Attacher::AttachEngine3D
  AttachmentOffset = pos=(0,0,0) rot=(-1,0,0;1.5708rad)
  MapMode = 45
  Placement = pos=(45.8013,31.6395,125) rot=(0,0,1;1.0472rad)
  Support = -> [Hole002]
FEATURE [PartDesign::CoordinateSystem] LCS_3
  AttacherType = Attacher::AttachEngine3D
  AttachmentOffset = pos=(0,0,0) rot=(-1,0,0;1.5708rad)
  MapMode = 45
  Placement = pos=(-46.1852,31.1499,125) rot=(0,0,1;2.0858rad)
  Support = -> [Hole002]
FEATURE [PartDesign::Body] Body  label="MiddlePartialBody"
  Group = -> [Sketch,Pad,Sketch001,Pocket,LCS_1,Sketch002,Sketch003,Sketch004,Sketch005,Sketch006,Sketch007,Sketch008,Sketch009,Pad001,Hole,Hole001,Pocket001,Pocket002,Pad002,Sketch010,Hole002,LCS_2,LCS_3]
  Origin = -> Origin
  Tip = -> Hole002
---- part classifier_part.FCStd = doc fcstd_71d70442dcd3 ----
FCSTD DOCUMENT  (FreeCAD 0.20R29177 +426 (Git))
Label: classifier_part
License: All rights reserved
LicenseURL: http://en.wikipedia.org/wiki/All_rights_reserved
objects: Sketcher::SketchObject×14, PartDesign::Pad×12, PartDesign::Pocket×2, PartDesign::CoordinateSystem×1, PartDesign::Body×1
note: 44 computed .brp shape members not serialized (recipe doc carries the construction recipe); baked Part::Feature solids carry a one-line shape summary decoded from their .brp

FEATURE [Sketcher::SketchObject] Sketch007
  FullyConstrained = true
  MapMode = 5
  Support = -> [XY_Plane]
  sketch-geometry (14):
    g0: LineSegment StartX=86.6025 StartY=50 StartZ=0 EndX=1.42e-14 EndY=100 EndZ=0
    g1: LineSegment StartX=1.42e-14 StartY=100 StartZ=0 EndX=-86.6025 EndY=50 EndZ=0
    g2: LineSegment StartX=-86.6025 StartY=50 StartZ=0 EndX=-86.6025 EndY=-50 EndZ=0
    g3: LineSegment StartX=-86.6025 StartY=-50 StartZ=0 EndX=0 EndY=-100 EndZ=0
    g4: LineSegment StartX=0 StartY=-100 StartZ=0 EndX=86.6025 EndY=-50 EndZ=0
    g5: LineSegment StartX=86.6025 StartY=-50 StartZ=0 EndX=86.6025 EndY=50 EndZ=0
    g6: Circle CenterX=0 CenterY=0 CenterZ=0 NormalX=0 NormalY=0 NormalZ=1 AngleXU=0 Radius=100
    g7: LineSegment StartX=88.3346 StartY=51 StartZ=0 EndX=0 EndY=102 EndZ=0
    g8: LineSegment StartX=0 StartY=102 StartZ=0 EndX=-88.3346 EndY=51 EndZ=0
    g9: LineSegment StartX=-88.3346 StartY=51 StartZ=0 EndX=-88.3346 EndY=-51 EndZ=0
    g10: LineSegment StartX=-88.3346 StartY=-51 StartZ=0 EndX=1.42e-14 EndY=-102 EndZ=0
    g11: LineSegment StartX=1.42e-14 StartY=-102 StartZ=0 EndX=88.3346 EndY=-51 EndZ=0
    g12: LineSegment StartX=88.3346 StartY=-51 StartZ=0 EndX=88.3346 EndY=51 EndZ=0
    g13: Circle CenterX=0 CenterY=0 CenterZ=0 NormalX=0 NormalY=0 NormalZ=1 AngleXU=0 Radius=102
  constraints (32):
    c: Coincident(g0,g1)
    c: Coincident(g1,g2)
    c: Coincident(g2,g3)
    c: Coincident(g3,g4)
    c: Coincident(g4,g5)
    c: Coincident(g5,g0)
    c: Equal(g0, g1-g5) x5
    c: PointOnObject(g0,g6)
    c: PointOnObject(g1,g6)
    c: PointOnObject(g2,g6)
    c: PointOnObject(g3,g6)
    c: PointOnObject(g4,g6)
    c: PointOnObject(g5,g6)
    c: Coincident(g6,g-1)
    c: PointOnObject(g3,g-2)
    c: DistanceY(g5,g5) = 100
    c: Coincident(g7,g8)
    c: Coincident(g8,g9)
    c: Coincident(g9,g10)
    c: Coincident(g10,g11)
    c: Coincident(g11,g12)
    c: Coincident(g12,g7)
    c: Equal(g7, g8-g12) x5
    c: PointOnObject(g7,g13)
    c: PointOnObject(g8,g13)
    c: PointOnObject(g9,g13)
    c: PointOnObject(g10,g13)
    c: PointOnObject(g11,g13)
    c: PointOnObject(g12,g13)
    c: Coincident(g13,g6)
    c: Distance(g0,g7) = 2
    c: PointOnObject(g7,g-2)
FEATURE [PartDesign::Pad] Pad
  Direction = (0,0,1)
  Length = 150
  Length2 = 10
  Profile = -> Sketch007
  ReferenceAxis = -> Sketch007 [N_Axis]
  Type = 0
FEATURE [Sketcher::SketchObject] Sketch
  ExternalGeometry = -> [Pad]
  FullyConstrained = true
  MapMode = 5
  Placement = pos=(86.6025,-1.21e-14,0) rot=(-0.57735,0.57735,0.57735;4.18879rad)
  Support = -> [Pad]
  sketch-geometry (4):
    g0: LineSegment StartX=-31 StartY=150 StartZ=0 EndX=31 EndY=150 EndZ=0
    g1: LineSegment StartX=31 StartY=150 StartZ=0 EndX=31 EndY=0 EndZ=0
    g2: LineSegment StartX=31 StartY=0 StartZ=0 EndX=-31 EndY=0 EndZ=0
    g3: LineSegment StartX=-31 StartY=0 StartZ=0 EndX=-31 EndY=150 EndZ=0
  constraints (11):
    c: Coincident(g0,g1)
    c: Coincident(g1,g2)
    c: Coincident(g2,g3)
    c: Coincident(g3,g0)
    c: Horizontal(g2)
    c: Vertical(g1)
    c: Vertical(g3)
    c: PointOnObject(g1,g-1)
    c: PointOnObject(g0,g-3)
    c: Symmetric(g0,g0,g-2)
    c: DistanceX(g0,g0) = 62
FEATURE [PartDesign::Pad] Pad001
  BaseFeature = -> Pad
  Direction = (-1,1e-16,1e-16)
  Length = 12
  Length2 = 10
  Profile = -> Sketch
  ReferenceAxis = -> Sketch [N_Axis]
  Type = 0
FEATURE [Sketcher::SketchObject] Sketch008
  FullyConstrained = true
  MapMode = 5
  Placement = pos=(88.3346,0,0) rot=(0.57735,0.57735,0.57735;2.0944rad)
  Support = -> [Pad001]
  sketch-geometry (4):
    g0: LineSegment StartX=-30.25 StartY=120 StartZ=0 EndX=30.25 EndY=120 EndZ=0
    g1: LineSegment StartX=30.25 StartY=120 StartZ=0 EndX=30.25 EndY=0 EndZ=0
    g2: LineSegment StartX=30.25 StartY=0 StartZ=0 EndX=-30.25 EndY=0 EndZ=0
    g3: LineSegment StartX=-30.25 StartY=0 StartZ=0 EndX=-30.25 EndY=120 EndZ=0
  constraints (11):
    c: Coincident(g0,g1)
    c: Coincident(g1,g2)
    c: Coincident(g2,g3)
    c: Coincident(g3,g0)
    c: Horizontal(g0)
    c: Vertical(g1)
    c: Vertical(g3)
    c: PointOnObject(g1,g-1)
    c: Symmetric(g1,g2,g-2)
    c: DistanceX(g2,g1) = 60.5
    c: DistanceY(g1,g1) = 120
FEATURE [PartDesign::Pocket] Pocket
  BaseFeature = -> Pad001
  Direction = (-1,0,0)
  Length = 12.5
  Length2 = 5
  Profile = -> Sketch008
  ReferenceAxis = -> Sketch008 [N_Axis]
  Type = 0
FEATURE [Sketcher::SketchObject] Sketch009
  ExternalGeometry = -> [Pocket]
  FullyConstrained = true
  MapMode = 5
  Placement = pos=(0,0,120) rot=(1,0,0;3.14159rad)
  Support = -> [Pocket]
  sketch-geometry (4):
    g0: LineSegment StartX=80.8346 StartY=26.5 StartZ=0 EndX=83.8346 EndY=26.5 EndZ=0
    g1: LineSegment StartX=83.8346 StartY=26.5 StartZ=0 EndX=83.8346 EndY=-26.5 EndZ=0
    g2: LineSegment StartX=83.8346 StartY=-26.5 StartZ=0 EndX=80.8346 EndY=-26.5 EndZ=0
    g3: LineSegment StartX=80.8346 StartY=-26.5 StartZ=0 EndX=80.8346 EndY=26.5 EndZ=0
  constraints (12):
    c: Coincident(g0,g1)
    c: Coincident(g1,g2)
    c: Coincident(g2,g3)
    c: Coincident(g3,g0)
    c: Horizontal(g0)
    c: Horizontal(g2)
    c: Vertical(g3)
    c: DistanceY(g1,g1) = 53
    c: DistanceX(g2,g2) = 3
    c: Symmetric(g1,g0,g-1)
    c: DistanceX(g-5,g2) = 5
    c: DistanceX(g1,g-3) = 4.5
FEATURE [PartDesign::Pad] Pad002  label="connectorPad"
  BaseFeature = -> Pocket
  Direction = (0,0,-1)
  Length = 120
  Length2 = 10
  Profile = -> Sketch009
  ReferenceAxis = -> Sketch009 [N_Axis]
  Type = 0
FEATURE [Sketcher::SketchObject] Sketch010
  ExternalGeometry = -> [Pad002]
  FullyConstrained = true
  MapMode = 5
  Placement = pos=(-44.1673,76.5,0) rot=(-0.186157,0.694747,0.694747;3.50969rad)
  Support = -> [Pad002]
  sketch-geometry (4):
    g0: LineSegment StartX=-31 StartY=130 StartZ=0 EndX=-26 EndY=130 EndZ=0
    g1: LineSegment StartX=-26 StartY=130 StartZ=0 EndX=-26 EndY=129 EndZ=0
    g2: LineSegment StartX=-26 StartY=129 StartZ=0 EndX=-31 EndY=129 EndZ=0
    g3: LineSegment StartX=-31 StartY=129 StartZ=0 EndX=-31 EndY=130 EndZ=0
  constraints (12):
    c: Coincident(g0,g1)
    c: Coincident(g1,g2)
    c: Coincident(g2,g3)
    c: Coincident(g3,g0)
    c: Horizontal(g0)
    c: Horizontal(g2)
    c: Vertical(g1)
    c: Vertical(g3)
    c: DistanceY(g0,g-4) = 20
    c: DistanceX(g-4,g0) = 20
    c: DistanceX(g0,g0) = 5
    c: DistanceY(g1,g1) = 1
FEATURE [PartDesign::Pad] Pad003
  BaseFeature = -> Pad002
  Direction = (-0.5,0.866025,1e-16)
  Length = 20
  Length2 = 10
  Profile = -> Sketch010
  ReferenceAxis = -> Sketch010 [N_Axis]
  Type = 0
FEATURE [Sketcher::SketchObject] Sketch011
  ExternalGeometry = -> [Pad003]
  FullyConstrained = true
  MapMode = 5
  Placement = pos=(-54.1673,93.8205,1.972e-13) rot=(-0.186157,0.694747,0.694747;3.50969rad)
  Support = -> [Pad003]
  sketch-geometry (6):
    g0: LineSegment StartX=-33.5 StartY=132 StartZ=0 EndX=-33.5 EndY=127 EndZ=0
    g1: LineSegment StartX=-33.5 StartY=127 StartZ=0 EndX=-23.5 EndY=127 EndZ=0
    g2: LineSegment StartX=-23.5 StartY=127 StartZ=0 EndX=-23.5 EndY=132 EndZ=0
    g3: LineSegment StartX=-23.5 StartY=132 StartZ=0 EndX=-33.5 EndY=132 EndZ=0
    g4: GeomPoint X=-28.5 Y=129.5 Z=0
    g5: GeomPoint X=-28.5 Y=129.5 Z=0
  constraints (13):
    c: Coincident(g0,g1)
    c: Coincident(g1,g2)
    c: Coincident(g2,g3)
    c: Coincident(g3,g0)
    c: Horizontal(g1)
    c: Horizontal(g3)
    c: Vertical(g0)
    c: Vertical(g2)
    c: Symmetric(g1,g0,g4)
    c: Symmetric(g-3,g-4,g5)
    c: Coincident(g4,g5)
    c: DistanceY(g2,g2) = 5
    c: DistanceX(g1,g1) = 10
FEATURE [PartDesign::Pad] Pad004
  BaseFeature = -> Pad003
  Direction = (-0.5,0.866025,1.5e-15)
  Length = 1
  Length2 = 10
  Profile = -> Sketch011
  ReferenceAxis = -> Sketch011 [N_Axis]
  Type = 0
FEATURE [Sketcher::SketchObject] Sketch012
  ExternalGeometry = -> [Pad004]
  FullyConstrained = true
  MapMode = 5
  Placement = pos=(-44.1673,-76.5,0) rot=(0.935113,-0.250563,-0.250563;1.63783rad)
  Support = -> [Pad004]
  sketch-geometry (5):
    g0: LineSegment StartX=26 StartY=130 StartZ=0 EndX=26 EndY=129 EndZ=0
    g1: LineSegment StartX=26 StartY=129 StartZ=0 EndX=31 EndY=129 EndZ=0
    g2: LineSegment StartX=31 StartY=129 StartZ=0 EndX=31 EndY=130 EndZ=0
    g3: LineSegment StartX=31 StartY=130 StartZ=0 EndX=26 EndY=130 EndZ=0
    g4: GeomPoint X=28.5 Y=129.5 Z=0
  constraints (13):
    c: Coincident(g0,g1)
    c: Coincident(g1,g2)
    c: Coincident(g2,g3)
    c: Coincident(g3,g0)
    c: Horizontal(g1)
    c: Horizontal(g3)
    c: Vertical(g0)
    c: Vertical(g2)
    c: Symmetric(g1,g0,g4)
    c: DistanceY(g2,g-4) = 20
    c: DistanceX(g2,g-4) = 20
    c: DistanceY(g2,g2) = 1
    c: DistanceX(g1,g1) = 5
FEATURE [PartDesign::Pad] Pad005
  BaseFeature = -> Pad004
  Direction = (-0.5,-0.866025,-1e-16)
  Length = 20
  Length2 = 10
  Profile = -> Sketch012
  ReferenceAxis = -> Sketch012 [N_Axis]
  Type = 0
FEATURE [Sketcher::SketchObject] Sketch013
  ExternalGeometry = -> [Pad005]
  FullyConstrained = true
  MapMode = 5
  Placement = pos=(-54.1673,-93.8205,-2.004e-13) rot=(0.935113,-0.250563,-0.250563;1.63783rad)
  Support = -> [Pad005]
  sketch-geometry (6):
    g0: LineSegment StartX=23.5 StartY=132 StartZ=0 EndX=23.5 EndY=127 EndZ=0
    g1: LineSegment StartX=23.5 StartY=127 StartZ=0 EndX=33.5 EndY=127 EndZ=0
    g2: LineSegment StartX=33.5 StartY=127 StartZ=0 EndX=33.5 EndY=132 EndZ=0
    g3: LineSegment StartX=33.5 StartY=132 StartZ=0 EndX=23.5 EndY=132 EndZ=0
    g4: GeomPoint X=28.5 Y=129.5 Z=0
    g5: GeomPoint X=28.5 Y=129.5 Z=0
  constraints (13):
    c: Coincident(g0,g1)
    c: Coincident(g1,g2)
    c: Coincident(g2,g3)
    c: Coincident(g3,g0)
    c: Horizontal(g1)
    c: Horizontal(g3)
    c: Vertical(g0)
    c: Vertical(g2)
    c: Symmetric(g1,g0,g4)
    c: Symmetric(g-4,g-3,g5)
    c: Coincident(g4,g5)
    c: DistanceX(g1,g1) = 10
    c: DistanceY(g2,g2) = 5
FEATURE [PartDesign::Pad] Pad006
  BaseFeature = -> Pad005
  Direction = (-0.5,-0.866025,-1.9e-15)
  Length = 1
  Length2 = 10
  Profile = -> Sketch013
  ReferenceAxis = -> Sketch013 [N_Axis]
  Type = 0
FEATURE [Sketcher::SketchObject] Sketch014
  ExternalGeometry = -> [Pad006]
  FullyConstrained = true
  MapMode = 5
  Placement = pos=(1.65e-14,-1.65e-14,150) rot=(0,0,1;0rad)
  Support = -> [Pad006]
  sketch-geometry (6):
    g0: LineSegment StartX=77.1025 StartY=-2.5 StartZ=0 EndX=77.1025 EndY=2.5 EndZ=0
    g1: LineSegment StartX=77.1025 StartY=2.5 StartZ=0 EndX=78.1025 EndY=2.5 EndZ=0
    g2: LineSegment StartX=78.1025 StartY=2.5 StartZ=0 EndX=78.1025 EndY=-2.5 EndZ=0
    g3: LineSegment StartX=78.1025 StartY=-2.5 StartZ=0 EndX=77.1025 EndY=-2.5 EndZ=0
    g4: GeomPoint X=77.6025 Y=0 Z=0
    g5: GeomPoint X=86.6025 Y=0 Z=0
  constraints (15):
    c: Coincident(g0,g1)
    c: Coincident(g1,g2)
    c: Coincident(g2,g3)
    c: Coincident(g3,g0)
    c: Horizontal(g1)
    c: Horizontal(g3)
    c: Vertical(g0)
    c: Vertical(g2)
    c: Symmetric(g1,g0,g4)
    c: PointOnObject(g4,g-1)
    c: DistanceY(g2,g2) = 5
    c: DistanceX(g1,g1) = 1
    c: PointOnObject(g5,g-3)
    c: PointOnObject(g5,g-1)
    c: DistanceX(g4,g5) = 9
FEATURE [PartDesign::Pad] Pad007
  BaseFeature = -> Pad006
  Direction = (1e-16,-1e-16,1)
  Length = 20
  Length2 = 10
  Profile = -> Sketch014
  ReferenceAxis = -> Sketch014 [N_Axis]
  Type = 0
FEATURE [Sketcher::SketchObject] Sketch015
  ExternalGeometry = -> [Pad007]
  FullyConstrained = true
  MapMode = 5
  Placement = pos=(0,0,170) rot=(0,0,1;0rad)
  Support = -> [Pad007]
  sketch-geometry (6):
    g0: GeomPoint X=77.6025 Y=-2.11e-14 Z=0
    g1: LineSegment StartX=75.1025 StartY=5 StartZ=0 EndX=75.1025 EndY=-5 EndZ=0
    g2: LineSegment StartX=75.1025 StartY=-5 StartZ=0 EndX=80.1025 EndY=-5 EndZ=0
    g3: LineSegment StartX=80.1025 StartY=-5 StartZ=0 EndX=80.1025 EndY=5 EndZ=0
    g4: LineSegment StartX=80.1025 StartY=5 StartZ=0 EndX=75.1025 EndY=5 EndZ=0
    g5: GeomPoint X=77.6025 Y=-2.11e-14 Z=0
  constraints (13):
    c: Symmetric(g-3,g-4,g0)
    c: Coincident(g1,g2)
    c: Coincident(g2,g3)
    c: Coincident(g3,g4)
    c: Coincident(g4,g1)
    c: Horizontal(g2)
    c: Horizontal(g4)
    c: Vertical(g1)
    c: Vertical(g3)
    c: Symmetric(g2,g1,g5)
    c: Coincident(g5,g0)
    c: DistanceX(g2,g2) = 5
    c: DistanceY(g3,g3) = 10
FEATURE [PartDesign::Pad] Pad008
  BaseFeature = -> Pad007
  Direction = (0,0,1)
  Length = 1
  Length2 = 10
  Profile = -> Sketch015
  ReferenceAxis = -> Sketch015 [N_Axis]
  Type = 0
FEATURE [Sketcher::SketchObject] Sketch016
  FullyConstrained = false
  MapMode = 5
  Placement = pos=(-88.3346,-1.24e-14,0) rot=(0.57735,-0.57735,-0.57735;2.0944rad)
  Support = -> [Pad008]
  sketch-geometry (6):
    g0: LineSegment StartX=-2.5 StartY=80.5 StartZ=0 EndX=-2.5 EndY=79.5 EndZ=0
    g1: LineSegment StartX=-2.5 StartY=79.5 StartZ=0 EndX=2.5 EndY=79.5 EndZ=0
    g2: LineSegment StartX=2.5 StartY=79.5 StartZ=0 EndX=2.5 EndY=80.5 EndZ=0
    g3: LineSegment StartX=2.5 StartY=80.5 StartZ=0 EndX=-2.5 EndY=80.5 EndZ=0
    g4: GeomPoint X=0 Y=80 Z=0
    g5: GeomPoint X=0 Y=150 Z=0
  constraints (14):
    c: Coincident(g0,g1)
    c: Coincident(g1,g2)
    c: Coincident(g2,g3)
    c: Coincident(g3,g0)
    c: Horizontal(g1)
    c: Horizontal(g3)
    c: Vertical(g0)
    c: Vertical(g2)
    c: Symmetric(g1,g0,g4)
    c: PointOnObject(g4,g-2)
    c: DistanceX(g1,g1) = 5
    c: DistanceY(g2,g2) = 1
    c: PointOnObject(g5,g-2)
    c: DistanceY(g4,g5) = 70
FEATURE [PartDesign::Pad] Pad009
  BaseFeature = -> Pad008
  Direction = (-1,-1e-16,-1e-16)
  Length = 20
  Length2 = 10
  Profile = -> Sketch016
  ReferenceAxis = -> Sketch016 [N_Axis]
  Type = 0
FEATURE [Sketcher::SketchObject] Sketch017
  ExternalGeometry = -> [Pad009]
  FullyConstrained = true
  MapMode = 5
  Placement = pos=(-108.335,0,0) rot=(0.57735,-0.57735,-0.57735;2.0944rad)
  Support = -> [Pad009]
  sketch-geometry (7):
    g0: LineSegment StartX=-5 StartY=82.5 StartZ=0 EndX=-5 EndY=77.5 EndZ=0
    g1: LineSegment StartX=-5 StartY=77.5 StartZ=0 EndX=5 EndY=77.5 EndZ=0
    g2: LineSegment StartX=5 StartY=77.5 StartZ=0 EndX=5 EndY=82.5 EndZ=0
    g3: LineSegment StartX=5 StartY=82.5 StartZ=0 EndX=-5 EndY=82.5 EndZ=0
    g4: GeomPoint X=2.27e-14 Y=80 Z=0
    g5: GeomPoint X=2.27e-14 Y=80 Z=0
    g6: GeomPoint X=2.27e-14 Y=80 Z=0
  constraints (14):
    c: Coincident(g0,g1)
    c: Coincident(g1,g2)
    c: Coincident(g2,g3)
    c: Coincident(g3,g0)
    c: Horizontal(g1)
    c: Horizontal(g3)
    c: Vertical(g0)
    c: Vertical(g2)
    c: Symmetric(g1,g0,g4)
    c: Coincident(g4,g5)
    c: DistanceX(g1,g1) = 10
    c: DistanceY(g2,g2) = 5
    c: Symmetric(g-4,g-3,g6)
    c: Coincident(g4,g6)
FEATURE [PartDesign::Pad] Pad010
  BaseFeature = -> Pad009
  Direction = (-1,0,0)
  Length = 1
  Length2 = 10
  Profile = -> Sketch017
  ReferenceAxis = -> Sketch017 [N_Axis]
  Type = 0
FEATURE [Sketcher::SketchObject] Sketch018
  ExternalGeometry = -> [Pad010]
  FullyConstrained = true
  MapMode = 5
  Placement = pos=(1.65e-14,-1.65e-14,150) rot=(0,0,1;0rad)
  Support = -> [Pad010]
  sketch-geometry (4):
    g0: LineSegment StartX=84.3346 StartY=26.5 StartZ=0 EndX=88.3346 EndY=26.5 EndZ=0
    g1: LineSegment StartX=88.3346 StartY=26.5 StartZ=0 EndX=88.3346 EndY=-26.5 EndZ=0
    g2: LineSegment StartX=88.3346 StartY=-26.5 StartZ=0 EndX=84.3346 EndY=-26.5 EndZ=0
    g3: LineSegment StartX=84.3346 StartY=-26.5 StartZ=0 EndX=84.3346 EndY=26.5 EndZ=0
  constraints (12):
    c: Coincident(g0,g1)
    c: Coincident(g1,g2)
    c: Coincident(g2,g3)
    c: Coincident(g3,g0)
    c: Horizontal(g0)
    c: Horizontal(g2)
    c: Vertical(g3)
    c: DistanceY(g1,g1) = 53
    c: Symmetric(g0,g1,g-1)
    c: Tangent(g1,g-3)
    c: Tangent(g1,g-3) = 1.5708
    c: DistanceX(g2,g2) = 4
FEATURE [PartDesign::CoordinateSystem] LCS_1
  AttacherType = Attacher::AttachEngine3D
  AttachmentOffset = pos=(0,0,0) rot=(-1,0,0;1.5708rad)
  MapMode = 45
  Placement = pos=(83.8346,1.8e-15,120) rot=(0,0,1;3.14159rad)
  Support = -> [Pad010]
FEATURE [PartDesign::Pocket] Pocket001
  BaseFeature = -> Pad010
  Direction = (-1e-16,1e-16,-1)
  Length = 30
  Length2 = 5
  Profile = -> Sketch018
  ReferenceAxis = -> Sketch018 [N_Axis]
  Type = 0
FEATURE [Sketcher::SketchObject] Sketch019
  ExternalGeometry = -> [Pocket001]
  FullyConstrained = true
  MapMode = 5
  Placement = pos=(0,0,0) rot=(1,0,0;3.14159rad)
  Support = -> [Pocket001]
  sketch-geometry (12):
    g0: LineSegment StartX=88.3346 StartY=-51 StartZ=0 EndX=88.3346 EndY=51 EndZ=0
    g1: LineSegment StartX=88.3346 StartY=51 StartZ=0 EndX=-1.42e-14 EndY=102 EndZ=0
    g2: LineSegment StartX=-1.42e-14 StartY=102 StartZ=0 EndX=-88.3346 EndY=51 EndZ=0
    g3: LineSegment StartX=-88.3346 StartY=51 StartZ=0 EndX=-88.3346 EndY=-51 EndZ=0
    g4: LineSegment StartX=-88.3346 StartY=-51 StartZ=0 EndX=0 EndY=-102 EndZ=0
    g5: LineSegment StartX=0 StartY=-102 StartZ=0 EndX=88.3346 EndY=-51 EndZ=0
    g6: Circle CenterX=0 CenterY=0 CenterZ=0 NormalX=0 NormalY=0 NormalZ=1 AngleXU=0 Radius=102
    g7: LineSegment StartX=88.3346 StartY=-31 StartZ=0 EndX=88.3346 EndY=-51 EndZ=0
    g8: LineSegment StartX=88.3346 StartY=-31 StartZ=0 EndX=74.6025 EndY=-31 EndZ=0
    g9: LineSegment StartX=74.6025 StartY=-31 StartZ=0 EndX=74.6025 EndY=31 EndZ=0
    g10: LineSegment StartX=88.3346 StartY=31 StartZ=0 EndX=74.6025 EndY=31 EndZ=0
    g11: LineSegment StartX=88.3346 StartY=51 StartZ=0 EndX=88.3346 EndY=31 EndZ=0
  constraints (27):
    c: Coincident(g0,g1)
    c: Coincident(g1,g2)
    c: Coincident(g2,g3)
    c: Coincident(g3,g4)
    c: Coincident(g4,g5)
    c: Coincident(g5,g0)
    c: Equal(g0, g1-g5) x5
    c: PointOnObject(g0,g6)
    c: PointOnObject(g1,g6)
    c: PointOnObject(g2,g6)
    c: PointOnObject(g3,g6)
    c: PointOnObject(g4,g6)
    c: PointOnObject(g5,g6)
    c: Coincident(g6,g-1)
    c: Coincident(g0,g-3)
    c: PointOnObject(g7,g0)
    c: Coincident(g7,g5)
    c: Coincident(g8,g7)
    c: Coincident(g8,g-5)
    c: Horizontal(g8)
    c: Coincident(g9,g8)
    c: Coincident(g9,g-4)
    c: PointOnObject(g10,g0)
    c: Coincident(g10,g9)
    c: Horizontal(g10)
    c: Coincident(g11,g1)
    c: Coincident(g11,g10)
FEATURE [PartDesign::Pad] Pad011
  BaseFeature = -> Pocket001
  Direction = (0,0,-1)
  Length = 2
  Length2 = 10
  Profile = -> Sketch019
  ReferenceAxis = -> Sketch019 [N_Axis]
  Type = 0
FEATURE [PartDesign::Body] Body  label="ClassifierPartBody"
  Group = -> [Sketch007,Pad,Sketch,Pad001,Sketch008,Pocket,Sketch009,Pad002,Sketch010,Pad003,Sketch011,Pad004,Sketch012,Pad005,Sketch013,Pad006,Sketch014,Pad007,Sketch015,Pad008,Sketch016,Sketch017,Pad009,Pad010,Sketch018,LCS_1,Pocket001,Sketch019,Pad011]
  Origin = -> Origin
  Tip = -> Pad011
---- part esp32camMountRefined.FCStd = doc fcstd_4b9deea06e1b ----
FCSTD DOCUMENT  (FreeCAD 0.20R29177 +426 (Git))
Label: esp32camMountRefined
License: All rights reserved
LicenseURL: http://en.wikipedia.org/wiki/All_rights_reserved
objects: Part::Feature×2, Mesh::Feature×1, Part::Refine×1, PartDesign::FeatureBase×1, PartDesign::CoordinateSystem×1, PartDesign::Body×1
note: 6 computed .brp shape members not serialized (recipe doc carries the construction recipe); baked Part::Feature solids carry a one-line shape summary decoded from their .brp

FEATURE [Mesh::Feature] ImageToStl_com_esp_32_cam_mount  label="ImageToStl.com_esp+32+cam+mount"
  Placement = pos=(-52,-21,0) rot=(0,0,1;0rad)
FEATURE [Part::Feature] ImageToStl_com_esp_32_cam_mount001
  shape: bbox 40.3 x 20 x 20 mm, 552 faces, 0 solids (baked)
FEATURE [Part::Refine] ImageToStl_com_esp_32_cam_mount001001
  Source = -> ImageToStl_com_esp_32_cam_mount001
FEATURE [Part::Feature] ImageToStl_com_esp_32_cam_mount001001_solid  label="ImageToStl_com_esp_32_cam_mount001001 (Solid)"
  shape: bbox 40.3 x 20 x 20 mm, 137 faces (baked)
FEATURE [PartDesign::FeatureBase] BaseFeature
  BaseFeature = -> ImageToStl_com_esp_32_cam_mount001001_solid
FEATURE [PartDesign::CoordinateSystem] LCS_1
  AttacherType = Attacher::AttachEngine3D
  MapMode = 45
  Placement = pos=(-21,9,10) rot=(0.57735,0.57735,0.57735;2.0944rad)
  Support = -> [BaseFeature]
FEATURE [PartDesign::Body] Body  label="mountBody"
  BaseFeature = -> ImageToStl_com_esp_32_cam_mount001001_solid
  Group = -> [BaseFeature,LCS_1]
  Origin = -> Origin
  Tip = -> BaseFeature
---- part gear20.FCStd = doc fcstd_0624d7b559ef ----
FCSTD DOCUMENT  (FreeCAD 0.20R29177 +426 (Git))
Label: gear20
License: All rights reserved
LicenseURL: http://en.wikipedia.org/wiki/All_rights_reserved
objects: Sketcher::SketchObject×5, PartDesign::Pad×4, Part::FeaturePython×2, PartDesign::CoordinateSystem×2, PartDesign::FeaturePython×1, PartDesign::Pocket×1, App::AnnotationLabel×1, App::DocumentObjectGroup×1, PartDesign::Body×1
note: 21 computed .brp shape members not serialized (recipe doc carries the construction recipe); baked Part::Feature solids carry a one-line shape summary decoded from their .brp

FEATURE [PartDesign::FeaturePython] TimingGear002  # WARN: FeaturePython — macro-defined, semantics opaque (R4)
  AttacherType = Attacher::AttachEngine3D
  h = 0.75
  height = 6
  num_teeth = 20
  offset = 0.4
  pitch = 2
  r0 = 0.555
  r1 = 1
  rs = 0.15
  type = 0
  u = 0.254
  version = 1.3.0
FEATURE [Sketcher::SketchObject] Sketch047
  FullyConstrained = true
  MapMode = 5
  Placement = pos=(0,0,6) rot=(0,0,1;0rad)
  Support = -> [TimingGear002]
  sketch-geometry (1):
    g0: Circle CenterX=0 CenterY=0 CenterZ=0 NormalX=0 NormalY=0 NormalZ=1 AngleXU=0 Radius=5
  constraints (2):
    c: Coincident(g0,g-1)
    c: Diameter(g0) = 10
FEATURE [PartDesign::Pad] Pad027
  BaseFeature = -> TimingGear002
  Direction = (0,0,1)
  Length = 0.5
  Length2 = 10
  Profile = -> Sketch047
  ReferenceAxis = -> Sketch047 [N_Axis]
  Refine = true
  Type = 0
FEATURE [Sketcher::SketchObject] Sketch048
  FullyConstrained = true
  MapMode = 5
  Placement = pos=(0,0,6.5) rot=(0,0,1;0rad)
  Support = -> [Pad027]
  sketch-geometry (1):
    g0: Circle CenterX=0 CenterY=0 CenterZ=0 NormalX=0 NormalY=0 NormalZ=1 AngleXU=0 Radius=10
  constraints (2):
    c: Coincident(g0,g-1)
    c: Diameter(g0) = 20
FEATURE [PartDesign::Pad] Pad028
  BaseFeature = -> Pad027
  Direction = (0,0,1)
  Length = 2
  Length2 = 10
  Profile = -> Sketch048
  ReferenceAxis = -> Sketch048 [N_Axis]
  Refine = true
  Type = 0
FEATURE [Sketcher::SketchObject] Sketch049
  FullyConstrained = true
  MapMode = 5
  Placement = pos=(0,0,0) rot=(1,0,0;3.14159rad)
  Support = -> [Pad028]
  sketch-geometry (1):
    g0: Circle CenterX=0 CenterY=0 CenterZ=0 NormalX=0 NormalY=0 NormalZ=1 AngleXU=0 Radius=5
  constraints (2):
    c: Coincident(g0,g-1)
    c: Diameter(g0) = 10
FEATURE [PartDesign::Pad] Pad029
  BaseFeature = -> Pad028
  Direction = (0,0,-1)
  Length = 0.5
  Length2 = 10
  Profile = -> Sketch049
  ReferenceAxis = -> Sketch049 [N_Axis]
  Refine = true
  Type = 0
FEATURE [Sketcher::SketchObject] Sketch050
  FullyConstrained = true
  MapMode = 5
  Placement = pos=(0,0,-0.5) rot=(1,0,0;3.14159rad)
  Support = -> [Pad029]
  sketch-geometry (1):
    g0: Circle CenterX=0 CenterY=0 CenterZ=0 NormalX=0 NormalY=0 NormalZ=1 AngleXU=0 Radius=10
  constraints (2):
    c: Coincident(g0,g-1)
    c: Diameter(g0) = 20
FEATURE [PartDesign::Pad] Pad030
  BaseFeature = -> Pad029
  Direction = (0,0,-1)
  Length = 2
  Length2 = 10
  Profile = -> Sketch050
  ReferenceAxis = -> Sketch050 [N_Axis]
  Refine = true
  Type = 0
FEATURE [Sketcher::SketchObject] Sketch051
  FullyConstrained = true
  MapMode = 5
  Placement = pos=(0,0,8.5) rot=(0,0,1;0rad)
  Support = -> [Pad030]
  sketch-geometry (3):
    g0: ArcOfCircle CenterX=0 CenterY=0 CenterZ=0 NormalX=0 NormalY=0 NormalZ=1 AngleXU=0 Radius=2.475 StartAngle=0.651099 EndAngle=5.63209
    g1: LineSegment StartX=1.96866 StartY=0 StartZ=0 EndX=1.96866 EndY=1.5 EndZ=0
    g2: LineSegment StartX=1.96866 StartY=0 StartZ=0 EndX=1.96866 EndY=-1.5 EndZ=0
  constraints (9):
    c: Coincident(g0,g-1)
    c: Diameter(g0) = 4.95
    c: PointOnObject(g1,g-1)
    c: Vertical(g1)
    c: Vertical(g2)
    c: Coincident(g0,g1)
    c: Coincident(g0,g2)
    c: Coincident(g1,g2)
    c: DistanceY(g1,g1) = 1.5
FEATURE [PartDesign::Pocket] Pocket013
  BaseFeature = -> Pad030
  Direction = (0,0,-1)
  Length = 50
  Length2 = 5
  Profile = -> Sketch051
  ReferenceAxis = -> Sketch051 [N_Axis]
  Refine = true
  Type = 0
FEATURE [Part::FeaturePython] aCircle  # WARN: FeaturePython — macro-defined, semantics opaque (R4)
FEATURE [Part::FeaturePython] Radius  # WARN: FeaturePython — macro-defined, semantics opaque (R4)
FEATURE [App::AnnotationLabel] MeasureLbl
  BasePosition = (5,0,51.5)
  LabelText = R = 5,00 mm
  TextPosition = (0,0,0)
FEATURE [App::DocumentObjectGroup] Measures
  Group = -> [aCircle,Radius,MeasureLbl]
FEATURE [PartDesign::CoordinateSystem] LCS_belt
  AttacherType = Attacher::AttachEngine3D
  MapMode = 45
  Placement = pos=(2.37e-14,-1e-16,0) rot=(0,0,1;0rad)
  Support = -> [Pocket013]
FEATURE [PartDesign::CoordinateSystem] LCS_shaftStepper
  AttacherType = Attacher::AttachEngine3D
  MapMode = 11
  Placement = pos=(2e-16,4e-16,8.5) rot=(0,0,1;2.22189rad)
  Support = -> [Pocket013]
FEATURE [PartDesign::Body] Body005  label="gear20_body"
  Group = -> [TimingGear002,Sketch047,Pad027,Sketch048,Pad028,Sketch049,Pad029,Sketch050,Pad030,Sketch051,Pocket013,LCS_belt,LCS_shaftStepper]
  Origin = -> Origin005
  Placement = pos=(0,0,45) rot=(0,0,1;0rad)
  Tip = -> Pocket013
---- part gear60_lower.FCStd = doc fcstd_29fc62aa47c3 ----
FCSTD DOCUMENT  (FreeCAD 0.20R29177 +426 (Git))
Label: gear60_lower
License: All rights reserved
LicenseURL: http://en.wikipedia.org/wiki/All_rights_reserved
objects: Sketcher::SketchObject×8, PartDesign::Pad×6, PartDesign::CoordinateSystem×2, PartDesign::FeaturePython×1, PartDesign::Fillet×1, PartDesign::Pocket×1, PartDesign::Hole×1, PartDesign::Body×1
note: 30 computed .brp shape members not serialized (recipe doc carries the construction recipe); baked Part::Feature solids carry a one-line shape summary decoded from their .brp

FEATURE [Sketcher::SketchObject] Sketch012
  FullyConstrained = true
  MapMode = 5
  Placement = pos=(0,0,6) rot=(0,0,1;0rad)
  sketch-geometry (1):
    g0: Circle CenterX=0 CenterY=0 CenterZ=0 NormalX=0 NormalY=0 NormalZ=1 AngleXU=0 Radius=17.5
  constraints (2):
    c: Coincident(g0,g-1)
    c: Diameter(g0) = 35
FEATURE [Sketcher::SketchObject] Sketch013
  FullyConstrained = true
  MapMode = 5
  Placement = pos=(0,0,6.5) rot=(0,0,1;0rad)
  sketch-geometry (1):
    g0: Circle CenterX=0 CenterY=0 CenterZ=0 NormalX=0 NormalY=0 NormalZ=1 AngleXU=0 Radius=21
  constraints (2):
    c: Coincident(g0,g-1)
    c: Diameter(g0) = 42
FEATURE [Sketcher::SketchObject] Sketch014
  FullyConstrained = true
  MapMode = 5
  Placement = pos=(0,0,8.5) rot=(0,0,1;0rad)
  sketch-geometry (1):
    g0: Circle CenterX=0 CenterY=0 CenterZ=0 NormalX=0 NormalY=0 NormalZ=1 AngleXU=0 Radius=17.5
  constraints (2):
    c: Coincident(g0,g-1)
    c: Diameter(g0) = 35
FEATURE [Sketcher::SketchObject] Sketch015
  FullyConstrained = true
  MapMode = 5
  Placement = pos=(0,0,9) rot=(0,0,1;0rad)
  sketch-geometry (1):
    g0: Circle CenterX=0 CenterY=0 CenterZ=0 NormalX=0 NormalY=0 NormalZ=1 AngleXU=0 Radius=21
  constraints (2):
    c: Coincident(g0,g-1)
    c: Diameter(g0) = 42
FEATURE [PartDesign::FeaturePython] TimingGear001  # WARN: FeaturePython — macro-defined, semantics opaque (R4)
  AttacherType = Attacher::AttachEngine3D
  h = 0.75
  height = 6
  num_teeth = 60
  offset = 0.4
  pitch = 2
  r0 = 0.555
  r1 = 1
  rs = 0.15
  type = 0
  u = 0.254
  version = 1.3.0
FEATURE [PartDesign::Pad] Pad003
  BaseFeature = -> TimingGear001
  Direction = (0,0,1)
  Length = 0.5
  Length2 = 10
  Profile = -> Sketch012
  ReferenceAxis = -> Sketch012 [N_Axis]
  Refine = true
  Type = 0
FEATURE [PartDesign::Pad] Pad004
  BaseFeature = -> Pad003
  Direction = (0,0,1)
  Length = 2
  Length2 = 10
  Profile = -> Sketch013
  ReferenceAxis = -> Sketch013 [N_Axis]
  Refine = true
  Type = 0
FEATURE [PartDesign::Pad] Pad005
  BaseFeature = -> Pad004
  Direction = (0,0,1)
  Length = 0.5
  Length2 = 10
  Profile = -> Sketch014
  ReferenceAxis = -> Sketch014 [N_Axis]
  Refine = true
  Type = 0
FEATURE [PartDesign::Pad] Pad006
  BaseFeature = -> Pad005
  Direction = (0,0,1)
  Length = 2
  Length2 = 10
  Profile = -> Sketch015
  ReferenceAxis = -> Sketch015 [N_Axis]
  Refine = true
  Type = 0
FEATURE [PartDesign::Fillet] Fillet001
  Base = -> Pad006 [Edge1087,Edge1089,Edge4,Edge6]
  BaseFeature = -> Pad006
  Radius = 0.2
  Refine = true
  SupportTransform = false
  UseAllEdges = false
FEATURE [Sketcher::SketchObject] Sketch052
  FullyConstrained = true
  MapMode = 5
  Placement = pos=(0,0,0) rot=(1,0,0;3.14159rad)
  Support = -> [Fillet001]
  sketch-geometry (1):
    g0: Circle CenterX=0 CenterY=0 CenterZ=0 NormalX=0 NormalY=0 NormalZ=1 AngleXU=0 Radius=17.5
  constraints (2):
    c: Coincident(g0,g-1)
    c: Diameter(g0) = 35
FEATURE [PartDesign::Pad] Pad031
  BaseFeature = -> Fillet001
  Direction = (0,0,-1)
  Length = 0.5
  Length2 = 10
  Profile = -> Sketch052
  ReferenceAxis = -> Sketch052 [N_Axis]
  Refine = true
  Type = 0
FEATURE [Sketcher::SketchObject] Sketch053
  FullyConstrained = true
  MapMode = 5
  Placement = pos=(0,0,-0.5) rot=(1,0,0;3.14159rad)
  Support = -> [Pad031]
  sketch-geometry (1):
    g0: Circle CenterX=0 CenterY=0 CenterZ=0 NormalX=0 NormalY=0 NormalZ=1 AngleXU=0 Radius=21
  constraints (2):
    c: Coincident(g0,g-1)
    c: Diameter(g0) = 42
FEATURE [PartDesign::Pad] Pad032
  BaseFeature = -> Pad031
  Direction = (0,0,-1)
  Length = 2
  Length2 = 10
  Profile = -> Sketch053
  ReferenceAxis = -> Sketch053 [N_Axis]
  Refine = true
  Type = 0
FEATURE [Sketcher::SketchObject] Sketch054
  FullyConstrained = true
  MapMode = 5
  Placement = pos=(0,0,-2.5) rot=(1,0,0;3.14159rad)
  Support = -> [Pad032]
  sketch-geometry (1):
    g0: Circle CenterX=0 CenterY=0 CenterZ=0 NormalX=0 NormalY=0 NormalZ=1 AngleXU=0 Radius=2.55
  constraints (2):
    c: Coincident(g0,g-1)
    c: Diameter(g0) = 5.1
FEATURE [PartDesign::Pocket] Pocket014
  BaseFeature = -> Pad032
  Direction = (0,0,1)
  Length = 20
  Length2 = 5
  Profile = -> Sketch054
  ReferenceAxis = -> Sketch054 [N_Axis]
  Refine = true
  Type = 0
FEATURE [Sketcher::SketchObject] Sketch063
  FullyConstrained = true
  MapMode = 5
  Placement = pos=(0,0,11) rot=(0,0,1;0rad)
  Support = -> [Pocket014]
  sketch-geometry (7):
    g0: LineSegment StartX=10 StartY=-5.7735 StartZ=0 EndX=0 EndY=11.547 EndZ=0
    g1: LineSegment StartX=0 StartY=11.547 StartZ=0 EndX=-10 EndY=-5.7735 EndZ=0
    g2: LineSegment StartX=-10 StartY=-5.7735 StartZ=0 EndX=10 EndY=-5.7735 EndZ=0
    g3: Circle CenterX=0 CenterY=0 CenterZ=0 NormalX=0 NormalY=0 NormalZ=1 AngleXU=0 Radius=11.547
    g4: Circle CenterX=0 CenterY=11.547 CenterZ=0 NormalX=0 NormalY=0 NormalZ=1 AngleXU=0 Radius=2.8
    g5: Circle CenterX=10 CenterY=-5.7735 CenterZ=0 NormalX=0 NormalY=0 NormalZ=1 AngleXU=0 Radius=2.8
    g6: Circle CenterX=-10 CenterY=-5.7735 CenterZ=0 NormalX=0 NormalY=0 NormalZ=1 AngleXU=0 Radius=2.8
  constraints (17):
    c: Coincident(g0,g1)
    c: Coincident(g1,g2)
    c: Coincident(g2,g0)
    c: Equal(g0,g1)
    c: Equal(g0,g2)
    c: PointOnObject(g0,g3)
    c: PointOnObject(g1,g3)
    c: PointOnObject(g2,g3)
    c: Coincident(g3,g-1)
    c: PointOnObject(g0,g-2)
    c: Coincident(g4,g0)
    c: Coincident(g5,g0)
    c: Coincident(g6,g1)
    c: Equal(g5,g4)
    c: Equal(g4,g6)
    c: Diameter(g5) = 5.6
    c: DistanceX(g2,g2) = 20
FEATURE [PartDesign::Hole] Hole
  BaseFeature = -> Pocket014
  CustomThreadClearance = 0
  Depth = 6
  DepthType = 0
  Diameter = 2.5
  DrillForDepth = true
  DrillPoint = 1
  DrillPointAngle = 118
  HoleCutCountersinkAngle = 90
  HoleCutCustomValues = false
  HoleCutDepth = 0
  HoleCutDiameter = 6.1
  HoleCutType = 0
  ModelThread = false
  Profile = -> Sketch063
  Refine = true
  Tapered = false
  TaperedAngle = 90
  ThreadClass = 0
  ThreadDepth = 6
  ThreadDepthType = 0
  ThreadDirection = 0
  ThreadFit = 0
  ThreadSize = 9
  ThreadType = 1
  Threaded = true
  UseCustomThreadClearance = false
FEATURE [PartDesign::CoordinateSystem] LCS_1
  AttacherType = Attacher::AttachEngine3D
  MapMode = 45
  Placement = pos=(1.21e-14,-1e-16,11) rot=(0,0,1;0rad)
  Support = -> [Hole]
FEATURE [PartDesign::CoordinateSystem] LCS_Belt
  AttacherType = Attacher::AttachEngine3D
  MapMode = 45
  Placement = pos=(8.32e-14,-6e-16,0) rot=(0,0,1;0rad)
  Support = -> [Hole]
FEATURE [PartDesign::Body] Body004  label="gear60_lower_body"
  Group = -> [TimingGear001,Sketch012,Pad003,Sketch013,Pad004,Sketch014,Pad005,Sketch015,Pad006,Fillet001,Sketch052,Pad031,Sketch053,Pad032,Sketch054,Pocket014,Sketch063,Hole,LCS_1,LCS_Belt]
  Origin = -> Origin004
  Placement = pos=(-45,3,45.25) rot=(0,0,1;0rad)
  Tip = -> Hole
---- part gear60_upper.FCStd = doc fcstd_ddbde9e440cc ----
FCSTD DOCUMENT  (FreeCAD 0.20R29177 +426 (Git))
Label: gear60_upper
License: All rights reserved
LicenseURL: http://en.wikipedia.org/wiki/All_rights_reserved
objects: Sketcher::SketchObject×5, PartDesign::Pad×3, Part::FeaturePython×2, PartDesign::CoordinateSystem×2, PartDesign::FeaturePython×1, PartDesign::Fillet×1, PartDesign::Pocket×1, PartDesign::Hole×1, App::AnnotationLabel×1, App::DocumentObjectGroup×1, PartDesign::Body×1
note: 23 computed .brp shape members not serialized (recipe doc carries the construction recipe); baked Part::Feature solids carry a one-line shape summary decoded from their .brp

FEATURE [Sketcher::SketchObject] Sketch016
  FullyConstrained = true
  MapMode = 5
  Placement = pos=(0,0,0) rot=(1,0,0;3.14159rad)
  sketch-geometry (1):
    g0: Circle CenterX=0 CenterY=0 CenterZ=0 NormalX=0 NormalY=0 NormalZ=1 AngleXU=0 Radius=17.5
  constraints (2):
    c: Coincident(g0,g-1)
    c: Diameter(g0) = 35
FEATURE [Sketcher::SketchObject] Sketch017
  FullyConstrained = true
  MapMode = 5
  Placement = pos=(0,0,6) rot=(0,0,1;0rad)
  sketch-geometry (1):
    g0: Circle CenterX=0 CenterY=0 CenterZ=0 NormalX=0 NormalY=0 NormalZ=1 AngleXU=0 Radius=17.5
  constraints (2):
    c: Coincident(g0,g-1)
    c: Diameter(g0) = 35
FEATURE [Sketcher::SketchObject] Sketch018
  FullyConstrained = true
  MapMode = 5
  Placement = pos=(0,0,6.5) rot=(0,0,1;0rad)
  sketch-geometry (1):
    g0: Circle CenterX=0 CenterY=0 CenterZ=0 NormalX=0 NormalY=0 NormalZ=1 AngleXU=0 Radius=21
  constraints (2):
    c: Coincident(g0,g-1)
    c: Diameter(g0) = 42
FEATURE [PartDesign::FeaturePython] TimingGear003  # WARN: FeaturePython — macro-defined, semantics opaque (R4)
  AttacherType = Attacher::AttachEngine3D
  h = 0.75
  height = 6
  num_teeth = 60
  offset = 0.4
  pitch = 2
  r0 = 0.555
  r1 = 1
  rs = 0.15
  type = 0
  u = 0.254
  version = 1.3.0
FEATURE [PartDesign::Pad] Pad007
  BaseFeature = -> TimingGear003
  Direction = (0,0,-1)
  Length = 0.5
  Length2 = 10
  Profile = -> Sketch016
  ReferenceAxis = -> Sketch016 [N_Axis]
  Refine = true
  Type = 0
FEATURE [PartDesign::Pad] Pad008
  BaseFeature = -> Pad007
  Direction = (0,0,1)
  Length = 0.5
  Length2 = 10
  Profile = -> Sketch017
  ReferenceAxis = -> Sketch017 [N_Axis]
  Refine = true
  Type = 0
FEATURE [PartDesign::Pad] Pad009
  BaseFeature = -> Pad008
  Direction = (0,0,1)
  Length = 2
  Length2 = 10
  Profile = -> Sketch018
  ReferenceAxis = -> Sketch018 [N_Axis]
  Refine = true
  Type = 0
FEATURE [PartDesign::Fillet] Fillet
  Base = -> Pad009 [Edge4,Edge6,Edge1087]
  BaseFeature = -> Pad009
  Radius = 0.2
  Refine = true
  SupportTransform = false
  UseAllEdges = false
FEATURE [Sketcher::SketchObject] Sketch029
  FullyConstrained = true
  MapMode = 5
  Placement = pos=(0,0,8.5) rot=(0,0,1;0rad)
  Support = -> [Fillet]
  sketch-geometry (7):
    g0: LineSegment StartX=10 StartY=-5.7735 StartZ=0 EndX=0 EndY=11.547 EndZ=0
    g1: LineSegment StartX=0 StartY=11.547 StartZ=0 EndX=-10 EndY=-5.7735 EndZ=0
    g2: LineSegment StartX=-10 StartY=-5.7735 StartZ=0 EndX=10 EndY=-5.7735 EndZ=0
    g3: Circle CenterX=0 CenterY=0 CenterZ=0 NormalX=0 NormalY=0 NormalZ=1 AngleXU=0 Radius=11.547
    g4: Circle CenterX=10 CenterY=-5.7735 CenterZ=0 NormalX=0 NormalY=0 NormalZ=1 AngleXU=0 Radius=2.8
    g5: Circle CenterX=0 CenterY=11.547 CenterZ=0 NormalX=0 NormalY=0 NormalZ=1 AngleXU=0 Radius=2.8
    g6: Circle CenterX=-10 CenterY=-5.7735 CenterZ=0 NormalX=0 NormalY=0 NormalZ=1 AngleXU=0 Radius=2.8
  constraints (17):
    c: Coincident(g0,g1)
    c: Coincident(g1,g2)
    c: Coincident(g2,g0)
    c: Equal(g0,g1)
    c: Equal(g0,g2)
    c: PointOnObject(g0,g3)
    c: PointOnObject(g1,g3)
    c: PointOnObject(g2,g3)
    c: Coincident(g3,g-1)
    c: PointOnObject(g0,g-2)
    c: DistanceX(g2,g2) = 20
    c: Coincident(g4,g0)
    c: Coincident(g5,g0)
    c: Coincident(g6,g1)
    c: Equal(g5,g6)
    c: Equal(g6,g4)
    c: Diameter(g5) = 5.6
FEATURE [Sketcher::SketchObject] Sketch055
  FullyConstrained = true
  MapMode = 5
  Placement = pos=(0,0,-0.5) rot=(1,0,0;3.14159rad)
  Support = -> [Fillet]
  sketch-geometry (1):
    g0: Circle CenterX=0 CenterY=0 CenterZ=0 NormalX=0 NormalY=0 NormalZ=1 AngleXU=0 Radius=2.55
  constraints (2):
    c: Coincident(g0,g-1)
    c: Diameter(g0) = 5.1
FEATURE [PartDesign::Pocket] Pocket015
  BaseFeature = -> Fillet
  Direction = (0,0,1)
  Length = 12
  Length2 = 5
  Profile = -> Sketch055
  ReferenceAxis = -> Sketch055 [N_Axis]
  Refine = true
  Type = 0
FEATURE [PartDesign::Hole] Hole002
  BaseFeature = -> Pocket015
  CustomThreadClearance = 0
  Depth = 25
  DepthType = 0
  Diameter = 2.52
  DrillForDepth = true
  DrillPoint = 1
  DrillPointAngle = 118
  HoleCutCountersinkAngle = 90
  HoleCutCustomValues = false
  HoleCutDepth = 0
  HoleCutDiameter = 6.1
  HoleCutType = 2
  ModelThread = true
  Profile = -> Sketch029
  Refine = true
  Tapered = false
  TaperedAngle = 90
  ThreadClass = 0
  ThreadDepth = 25
  ThreadDepthType = 0
  ThreadDirection = 0
  ThreadFit = 0
  ThreadSize = 9
  ThreadType = 1
  Threaded = true
  UseCustomThreadClearance = false
FEATURE [Part::FeaturePython] aCircle  # WARN: FeaturePython — macro-defined, semantics opaque (R4)
FEATURE [Part::FeaturePython] Radius  # WARN: FeaturePython — macro-defined, semantics opaque (R4)
FEATURE [App::AnnotationLabel] MeasureLbl
  BasePosition = (-24.2,3,63.25)
  LabelText = R = 20,80 mm
  TextPosition = (0,0,0)
FEATURE [App::DocumentObjectGroup] Measures
  Group = -> [aCircle,Radius,MeasureLbl]
FEATURE [PartDesign::CoordinateSystem] LCS_belt
  AttacherType = Attacher::AttachEngine3D
  MapMode = 45
  Placement = pos=(8.32e-14,6e-16,6) rot=(0,0,1;0rad)
  Support = -> [Hole002]
FEATURE [PartDesign::CoordinateSystem] LCS_for_gear60lower
  AttacherType = Attacher::AttachEngine3D
  MapMode = 45
  Placement = pos=(1.21e-14,-1e-16,-0.5) rot=(0,0,1;0rad)
  Support = -> [Hole002]
FEATURE [PartDesign::Body] Body006  label="gear60_upperBody"
  Group = -> [TimingGear003,Sketch016,Pad007,Sketch017,Pad008,Sketch018,Pad009,Fillet,Sketch029,Sketch055,Pocket015,Hole002,LCS_belt,LCS_for_gear60lower]
  Origin = -> Origin006
  Placement = pos=(-45,3,56.75) rot=(0,0,1;0rad)
  Tip = -> Hole002
---- part gear66.FCStd = doc fcstd_0326d686318a ----
FCSTD DOCUMENT  (FreeCAD 0.20R29177 +426 (Git))
Label: gear66
License: All rights reserved
LicenseURL: http://en.wikipedia.org/wiki/All_rights_reserved
objects: Sketcher::SketchObject×6, PartDesign::Pad×3, PartDesign::Pocket×2, PartDesign::CoordinateSystem×2, Part::FeaturePython×2, PartDesign::FeaturePython×1, PartDesign::Hole×1, App::AnnotationLabel×1, App::DocumentObjectGroup×1, PartDesign::Body×1
note: 24 computed .brp shape members not serialized (recipe doc carries the construction recipe); baked Part::Feature solids carry a one-line shape summary decoded from their .brp

FEATURE [Sketcher::SketchObject] Sketch020
  FullyConstrained = true
  MapMode = 5
  Placement = pos=(0,0,6) rot=(0,0,1;0rad)
  sketch-geometry (1):
    g0: Circle CenterX=0 CenterY=0 CenterZ=0 NormalX=0 NormalY=0 NormalZ=1 AngleXU=0 Radius=17.5
  constraints (2):
    c: Coincident(g0,g-1)
    c: Diameter(g0) = 35
FEATURE [Sketcher::SketchObject] Sketch023
  FullyConstrained = true
  MapMode = 5
  Placement = pos=(0,0,0) rot=(1,0,0;3.14159rad)
  sketch-geometry (1):
    g0: Circle CenterX=0 CenterY=0 CenterZ=0 NormalX=0 NormalY=0 NormalZ=1 AngleXU=0 Radius=12.5
  constraints (2):
    c: Coincident(g0,g-1)
    c: Diameter(g0) = 25
FEATURE [PartDesign::FeaturePython] TimingGear  label="TimingGear66"  # WARN: FeaturePython — macro-defined, semantics opaque (R4)
  AttacherType = Attacher::AttachEngine3D
  h = 0.75
  height = 6
  num_teeth = 66
  offset = 0.4
  pitch = 2
  r0 = 0.555
  r1 = 1
  rs = 0.15
  type = 0
  u = 0.254
  version = 1.3.0
FEATURE [PartDesign::Pocket] Pocket009
  BaseFeature = -> TimingGear
  Direction = (0,0,1)
  Length = 30
  Length2 = 5
  Profile = -> Sketch023
  ReferenceAxis = -> Sketch023 [N_Axis]
  Refine = true
  Type = 0
FEATURE [PartDesign::Pad] Pad014
  BaseFeature = -> Pocket009
  Direction = (0,0,1)
  Length = 0.5
  Length2 = 10
  Profile = -> Sketch020
  ReferenceAxis = -> Sketch020 [N_Axis]
  Refine = true
  Type = 0
FEATURE [Sketcher::SketchObject] Sketch028
  FullyConstrained = true
  MapMode = 5
  Placement = pos=(0,0,6.5) rot=(0,0,1;0rad)
  Support = -> [Pad014]
  sketch-geometry (1):
    g0: Circle CenterX=0 CenterY=0 CenterZ=0 NormalX=0 NormalY=0 NormalZ=1 AngleXU=0 Radius=22.5
  constraints (2):
    c: Coincident(g0,g-1)
    c: Diameter(g0) = 45
FEATURE [PartDesign::Pad] Pad015
  BaseFeature = -> Pad014
  Direction = (0,0,1)
  Length = 10
  Length2 = 10
  Profile = -> Sketch028
  ReferenceAxis = -> Sketch028 [N_Axis]
  Refine = true
  Type = 0
FEATURE [Sketcher::SketchObject] Sketch021
  FullyConstrained = true
  MapMode = 5
  Placement = pos=(0,0,16.5) rot=(0,0,1;0rad)
  Support = -> [Pad015]
  sketch-geometry (1):
    g0: Circle CenterX=0 CenterY=0 CenterZ=0 NormalX=0 NormalY=0 NormalZ=1 AngleXU=0 Radius=50
  constraints (2):
    c: Coincident(g0,g-1)
    c: Diameter(g0) = 100
FEATURE [PartDesign::Pad] Pad016
  BaseFeature = -> Pad015
  Direction = (0,0,1)
  Length = 10
  Length2 = 10
  Profile = -> Sketch021
  ReferenceAxis = -> Sketch021 [N_Axis]
  Refine = true
  Type = 0
FEATURE [Sketcher::SketchObject] Sketch022
  FullyConstrained = true
  MapMode = 5
  Placement = pos=(0,0,16.5) rot=(1,0,0;3.14159rad)
  Support = -> [Pad016]
  sketch-geometry (7):
    g0: LineSegment StartX=35 StartY=-20.2073 StartZ=0 EndX=0 EndY=40.4145 EndZ=0
    g1: LineSegment StartX=0 StartY=40.4145 StartZ=0 EndX=-35 EndY=-20.2073 EndZ=0
    g2: LineSegment StartX=-35 StartY=-20.2073 StartZ=0 EndX=35 EndY=-20.2073 EndZ=0
    g3: Circle CenterX=0 CenterY=0 CenterZ=0 NormalX=0 NormalY=0 NormalZ=1 AngleXU=0 Radius=40.4145
    g4: Circle CenterX=0 CenterY=40.4145 CenterZ=0 NormalX=0 NormalY=0 NormalZ=1 AngleXU=0 Radius=2
    g5: Circle CenterX=35 CenterY=-20.2073 CenterZ=0 NormalX=0 NormalY=0 NormalZ=1 AngleXU=0 Radius=2
    g6: Circle CenterX=-35 CenterY=-20.2073 CenterZ=0 NormalX=0 NormalY=0 NormalZ=1 AngleXU=0 Radius=2
  constraints (17):
    c: Coincident(g0,g1)
    c: Coincident(g1,g2)
    c: Coincident(g2,g0)
    c: Equal(g0,g1)
    c: Equal(g0,g2)
    c: PointOnObject(g0,g3)
    c: PointOnObject(g1,g3)
    c: PointOnObject(g2,g3)
    c: Coincident(g3,g-1)
    c: PointOnObject(g0,g-2)
    c: Coincident(g4,g0)
    c: DistanceX(g2,g2) = 70
    c: Coincident(g5,g0)
    c: Coincident(g6,g1)
    c: Equal(g6,g4)
    c: Equal(g4,g5)
    c: Diameter(g6) = 4
FEATURE [Sketcher::SketchObject] Sketch065
  FullyConstrained = true
  MapMode = 5
  Placement = pos=(0,0,26.5) rot=(0,0,1;0rad)
  Support = -> [Pad016]
  sketch-geometry (1):
    g0: Circle CenterX=0 CenterY=0 CenterZ=0 NormalX=0 NormalY=0 NormalZ=1 AngleXU=0 Radius=12.5
  constraints (2):
    c: Coincident(g0,g-1)
    c: Diameter(g0) = 25
FEATURE [PartDesign::Pocket] Pocket016
  BaseFeature = -> Pad016
  Direction = (0,0,-1)
  Length = 30
  Length2 = 5
  Profile = -> Sketch065
  ReferenceAxis = -> Sketch065 [N_Axis]
  Refine = true
  Type = 0
FEATURE [PartDesign::Hole] Hole003
  BaseFeature = -> Pocket016
  CustomThreadClearance = 0
  Depth = 25
  DepthType = 0
  Diameter = 2.52
  DrillForDepth = false
  DrillPoint = 1
  DrillPointAngle = 118
  HoleCutCountersinkAngle = 90
  HoleCutCustomValues = false
  HoleCutDepth = 0
  HoleCutDiameter = 6.1
  HoleCutType = 2
  ModelThread = true
  Profile = -> Sketch022
  Refine = true
  Tapered = false
  TaperedAngle = 90
  ThreadClass = 0
  ThreadDepth = 25
  ThreadDepthType = 0
  ThreadDirection = 0
  ThreadFit = 0
  ThreadSize = 9
  ThreadType = 1
  Threaded = true
  UseCustomThreadClearance = false
FEATURE [PartDesign::CoordinateSystem] LCS_1
  AttacherType = Attacher::AttachEngine3D
  MapMode = 45
  Placement = pos=(5.94e-14,4e-16,26.5) rot=(0,0,1;0rad)
  Support = -> [Hole003]
FEATURE [Part::FeaturePython] aCircle  # WARN: FeaturePython — macro-defined, semantics opaque (R4)
FEATURE [Part::FeaturePython] Radius  # WARN: FeaturePython — macro-defined, semantics opaque (R4)
FEATURE [App::AnnotationLabel] MeasureLbl
  BasePosition = (25.45,54.95,63.25)
  LabelText = R = 22,50 mm
  TextPosition = (0,0,0)
FEATURE [App::DocumentObjectGroup] Measures
  Group = -> [aCircle,Radius,MeasureLbl]
FEATURE [PartDesign::CoordinateSystem] LCS_belt
  AttacherType = Attacher::AttachEngine3D
  MapMode = 45
  Placement = pos=(5.94e-14,-4e-16,0) rot=(0,0,1;0rad)
  Support = -> [Hole003]
FEATURE [PartDesign::Body] Body003  label="gear66Body"
  Group = -> [TimingGear,Sketch020,Sketch021,Sketch022,Sketch023,Pocket009,Pad014,Sketch028,Pad015,Pad016,Sketch065,Pocket016,Hole003,LCS_1,LCS_belt]
  Origin = -> Origin003
  Placement = pos=(2.95,54.95,56.75) rot=(0,0,1;0rad)
  Tip = -> Hole003
---- part hornHexagonModified.FCStd = doc fcstd_71265372c9fc ----
FCSTD DOCUMENT  (FreeCAD 0.20R29177 +426 (Git))
Label: hornHexagonModified
License: All rights reserved
LicenseURL: http://en.wikipedia.org/wiki/All_rights_reserved
objects: Sketcher::SketchObject×3, PartDesign::Pad×1, PartDesign::Pocket×1, PartDesign::Hole×1, PartDesign::CoordinateSystem×1, PartDesign::Body×1
note: 11 computed .brp shape members not serialized (recipe doc carries the construction recipe); baked Part::Feature solids carry a one-line shape summary decoded from their .brp

FEATURE [Sketcher::SketchObject] Sketch
  FullyConstrained = true
  MapMode = 5
  Support = -> [XY_Plane]
  sketch-geometry (7):
    g0: LineSegment StartX=86.6025 StartY=-50 StartZ=0 EndX=86.6025 EndY=50 EndZ=0
    g1: LineSegment StartX=86.6025 StartY=50 StartZ=0 EndX=0 EndY=100 EndZ=0
    g2: LineSegment StartX=6e-15 StartY=100 StartZ=0 EndX=-86.6025 EndY=50 EndZ=0
    g3: LineSegment StartX=-86.6025 StartY=50 StartZ=0 EndX=-86.6025 EndY=-50 EndZ=0
    g4: LineSegment StartX=-86.6025 StartY=-50 StartZ=0 EndX=0 EndY=-100 EndZ=0
    g5: LineSegment StartX=0 StartY=-100 StartZ=0 EndX=86.6025 EndY=-50 EndZ=0
    g6: Circle CenterX=0 CenterY=0 CenterZ=0 NormalX=0 NormalY=0 NormalZ=1 AngleXU=0 Radius=100
  constraints (16):
    c: Coincident(g0,g1)
    c: Coincident(g1,g2)
    c: Coincident(g2,g3)
    c: Coincident(g3,g4)
    c: Coincident(g4,g5)
    c: Coincident(g5,g0)
    c: Equal(g0, g1-g5) x5
    c: PointOnObject(g0,g6)
    c: PointOnObject(g1,g6)
    c: PointOnObject(g2,g6)
    c: PointOnObject(g3,g6)
    c: PointOnObject(g4,g6)
    c: PointOnObject(g5,g6)
    c: Coincident(g6,g-1)
    c: Vertical(g0)
    c: Diameter(g6) = 200
FEATURE [PartDesign::Pad] Pad
  Direction = (0,0,1)
  Length = 5
  Length2 = 10
  Profile = -> Sketch
  ReferenceAxis = -> Sketch [N_Axis]
  Type = 0
FEATURE [Sketcher::SketchObject] Sketch003
  ExternalGeometry = -> [Pad]
  FullyConstrained = true
  MapMode = 5
  Placement = pos=(0,0,0) rot=(1,0,0;3.14159rad)
  Support = -> [Pad]
  sketch-geometry (5):
    g0: ArcOfCircle CenterX=82.4925 CenterY=24 CenterZ=0 NormalX=0 NormalY=0 NormalZ=1 AngleXU=0 Radius=3.24 StartAngle=4.6245 EndAngle=7.94187
    g1: ArcOfCircle CenterX=67.6825 CenterY=24 CenterZ=0 NormalX=0 NormalY=0 NormalZ=1 AngleXU=0 Radius=1.94 StartAngle=1.65869 EndAngle=4.6245
    g2: LineSegment StartX=67.5123 StartY=25.9325 StartZ=0 EndX=82.2081 EndY=27.2275 EndZ=0
    g3: LineSegment StartX=67.5123 StartY=22.0675 StartZ=0 EndX=82.2081 EndY=20.7725 EndZ=0
    g4: GeomPoint X=85.7325 Y=24 Z=0
  constraints (12):
    c: Diameter(g1) = 3.88
    c: Diameter(g0) = 6.48
    c: Tangent(g2,g0) = 1.5708
    c: Tangent(g2,g1) = 1.5708
    c: Tangent(g3,g1) = -1.5708
    c: Tangent(g3,g0) = -1.5708
    c: DistanceX(g1,g0) = 14.81
    c: Horizontal(g0,g1)
    c: PointOnObject(g4,g0)
    c: Horizontal(g4,g0)
    c: DistanceY(g4,g-3) = 26
    c: DistanceX(g4,g-3) = 0.87
FEATURE [PartDesign::Pocket] Pocket
  BaseFeature = -> Pad
  Direction = (0,0,1)
  Length = 3
  Length2 = 5
  Profile = -> Sketch003
  ReferenceAxis = -> Sketch003 [N_Axis]
  Type = 0
FEATURE [Sketcher::SketchObject] Sketch004
  ExternalGeometry = -> [Pocket]
  FullyConstrained = true
  MapMode = 5
  Placement = pos=(0,0,3) rot=(1,0,0;3.14159rad)
  Support = -> [Pocket]
  sketch-geometry (4):
    g0: Circle CenterX=67.2125 CenterY=24 CenterZ=0 NormalX=0 NormalY=0 NormalZ=1 AngleXU=0 Radius=0.5
    g1: GeomPoint X=65.7425 Y=24 Z=0
    g2: Circle CenterX=70.7825 CenterY=24 CenterZ=0 NormalX=0 NormalY=0 NormalZ=1 AngleXU=0 Radius=0.5
    g3: Circle CenterX=74.3525 CenterY=24 CenterZ=0 NormalX=0 NormalY=0 NormalZ=1 AngleXU=0 Radius=0.5
  constraints (11):
    c: Horizontal(g-3,g0)
    c: PointOnObject(g1,g-3)
    c: Horizontal(g-3,g1)
    c: DistanceX(g1,g0) = 1.47
    c: Horizontal(g2,g0)
    c: DistanceX(g0,g2) = 3.57
    c: Equal(g2,g0)
    c: Diameter(g2) = 1
    c: Diameter(g3) = 1
    c: Horizontal(g3,g2)
    c: DistanceX(g2,g3) = 3.57
FEATURE [PartDesign::Hole] Hole
  BaseFeature = -> Pocket
  CustomThreadClearance = 0
  Depth = 25
  DepthType = 0
  Diameter = 1.6
  DrillForDepth = false
  DrillPoint = 1
  DrillPointAngle = 118
  HoleCutCountersinkAngle = 90
  HoleCutCustomValues = false
  HoleCutDepth = 0
  HoleCutDiameter = 6.1
  HoleCutType = 0
  ModelThread = false
  Profile = -> Sketch004
  Tapered = false
  TaperedAngle = 90
  ThreadClass = 0
  ThreadDepth = 25
  ThreadDepthType = 0
  ThreadDirection = 0
  ThreadFit = 0
  ThreadSize = 6
  ThreadType = 1
  Threaded = true
  UseCustomThreadClearance = false
FEATURE [PartDesign::CoordinateSystem] hexagonPlacement
  AttacherType = Attacher::AttachEngine3D
  MapMode = 45
  Placement = pos=(76.9057,-24,3) rot=(0,0,1;1.5708rad)
  Support = -> [Hole]
FEATURE [PartDesign::Body] Body  label="hornHexagonBody"
  Group = -> [Sketch,Pad,Sketch003,Pocket,Sketch004,Hole,hexagonPlacement]
  Origin = -> Origin
  Tip = -> Hole
---- part lowershaftHolder.FCStd = doc fcstd_8b0c963f3a0f ----
FCSTD DOCUMENT  (FreeCAD 0.20R29177 +426 (Git))
Label: lowershaftHolder
License: All rights reserved
LicenseURL: https://en.wikipedia.org/wiki/All_rights_reserved
objects: Sketcher::SketchObject×4, Part::Feature×3, Part::Refine×3, Part::MultiFuse×1, PartDesign::FeatureBase×1, PartDesign::Pad×1, PartDesign::AdditiveLoft×1, PartDesign::Pocket×1, PartDesign::CoordinateSystem×1, PartDesign::Body×1
note: 20 computed .brp shape members not serialized (recipe doc carries the construction recipe); baked Part::Feature solids carry a one-line shape summary decoded from their .brp

FEATURE [Part::Feature] Component003_solid  label="Component003 (Solid)"
  shape: bbox 15.99 x 80 x 4.799 mm, 20521 faces (baked)
FEATURE [Part::Feature] Component001001_solid  label="Component001001 (Solid)"
  shape: bbox 12 x 79.98 x 4.799 mm, 9304 faces (baked)
FEATURE [Part::Feature] Component002001_solid  label="Component002001 (Solid)"
  shape: bbox 12 x 79.97 x 4.799 mm, 9128 faces (baked)
FEATURE [Part::Refine] Component003_solid001  label="Component003 (Solid)001"
  Source = -> Component003_solid
FEATURE [Part::Refine] Component001001_solid001  label="Component001001 (Solid)001"
  Source = -> Component001001_solid
FEATURE [Part::Refine] Component002001_solid001  label="Component002001 (Solid)001"
  Source = -> Component002001_solid
FEATURE [Part::MultiFuse] Fusion
  Refine = true
  Shapes = -> [Component002001_solid001,Component003_solid001,Component001001_solid001]
FEATURE [PartDesign::FeatureBase] BaseFeature
  BaseFeature = -> Fusion
FEATURE [Sketcher::SketchObject] Sketch
  ExternalGeometry = -> [BaseFeature]
  FullyConstrained = true
  MapMode = 5
  Placement = pos=(0,0,3.2) rot=(0,0,1;0rad)
  Support = -> [BaseFeature]
  sketch-geometry (5):
    g0: LineSegment StartX=-38 StartY=-25 StartZ=0 EndX=-38 EndY=-55 EndZ=0
    g1: LineSegment StartX=-38 StartY=-55 StartZ=0 EndX=2 EndY=-55 EndZ=0
    g2: LineSegment StartX=2 StartY=-55 StartZ=0 EndX=2 EndY=-25 EndZ=0
    g3: LineSegment StartX=2 StartY=-25 StartZ=0 EndX=-38 EndY=-25 EndZ=0
    g4: GeomPoint X=-18 Y=-40 Z=0
  constraints (13):
    c: Coincident(g0,g1)
    c: Coincident(g1,g2)
    c: Coincident(g2,g3)
    c: Coincident(g3,g0)
    c: Horizontal(g1)
    c: Horizontal(g3)
    c: Vertical(g0)
    c: Vertical(g2)
    c: Symmetric(g1,g0,g4)
    c: PointOnObject(g1,g-3)
    c: DistanceY(g0,g0) = 30
    c: DistanceX(g4,g-3) = 20
    c: DistanceY(g-3,g4) = 40
FEATURE [PartDesign::Pad] Pad
  BaseFeature = -> BaseFeature
  Direction = (0,0,1)
  Length = 30
  Length2 = 10
  Profile = -> Sketch
  ReferenceAxis = -> Sketch [N_Axis]
  Refine = true
  Type = 0
FEATURE [Sketcher::SketchObject] Sketch001
  AttachmentOffset = pos=(0,0,20) rot=(0,0,1;0rad)
  FullyConstrained = true
  MapMode = 45
  Placement = pos=(-18,-40,53.2) rot=(0,0,1;1.5708rad)
  Support = -> [Pad]
  sketch-geometry (1):
    g0: Circle CenterX=0 CenterY=0 CenterZ=0 NormalX=0 NormalY=0 NormalZ=1 AngleXU=0 Radius=7
  constraints (2):
    c: Coincident(g0,g-1)
    c: Diameter(g0) = 14
FEATURE [Sketcher::SketchObject] Sketch002
  ExternalGeometry = -> [Pad]
  FullyConstrained = true
  MapMode = 45
  Placement = pos=(-18,-40,33.2) rot=(0,0,1;1.5708rad)
  Support = -> [Pad]
  sketch-geometry (5):
    g0: LineSegment StartX=-15 StartY=20 StartZ=0 EndX=-15 EndY=-20 EndZ=0
    g1: LineSegment StartX=-15 StartY=-20 StartZ=0 EndX=15 EndY=-20 EndZ=0
    g2: LineSegment StartX=15 StartY=-20 StartZ=0 EndX=15 EndY=20 EndZ=0
    g3: LineSegment StartX=15 StartY=20 StartZ=0 EndX=-15 EndY=20 EndZ=0
    g4: GeomPoint X=0 Y=0 Z=0
  constraints (12):
    c: Coincident(g0,g1)
    c: Coincident(g1,g2)
    c: Coincident(g2,g3)
    c: Coincident(g3,g0)
    c: Horizontal(g1)
    c: Horizontal(g3)
    c: Vertical(g0)
    c: Vertical(g2)
    c: Symmetric(g1,g0,g4)
    c: Coincident(g4,g-1)
    c: Equal(g-4,g2)
    c: Equal(g-3,g1)
FEATURE [PartDesign::AdditiveLoft] AdditiveLoft
  BaseFeature = -> Pad
  Closed = false
  Profile = -> Sketch002
  Refine = true
  Ruled = false
  Sections = -> [Sketch001]
FEATURE [Sketcher::SketchObject] Sketch003
  FullyConstrained = true
  MapMode = 45
  Placement = pos=(-18,-40,53.2) rot=(0,0,1;0rad)
  Support = -> [AdditiveLoft]
  sketch-geometry (1):
    g0: Circle CenterX=0 CenterY=0 CenterZ=0 NormalX=0 NormalY=0 NormalZ=1 AngleXU=0 Radius=6
  constraints (2):
    c: Coincident(g0,g-1)
    c: Diameter(g0) = 12
FEATURE [PartDesign::Pocket] Pocket
  BaseFeature = -> AdditiveLoft
  Direction = (0,0,-1)
  Length = 45
  Length2 = 5
  Profile = -> Sketch003
  ReferenceAxis = -> Sketch003 [N_Axis]
  Refine = true
  Type = 0
FEATURE [PartDesign::CoordinateSystem] LCS_1
  AttacherType = Attacher::AttachEngine3D
  MapMode = 45
  Placement = pos=(-17.9992,-40.0002,19.8008) rot=(0.576787,0.577583,0.57768;2.09485rad)
  Support = -> [Pocket]
FEATURE [PartDesign::Body] Body
  BaseFeature = -> Fusion
  Group = -> [BaseFeature,Sketch,Pad,Sketch001,Sketch002,AdditiveLoft,Sketch003,Pocket,LCS_1]
  Origin = -> Origin
  Tip = -> Pocket
---- part mid_hexagon_cmmon.FCStd = doc fcstd_b46b5ebb078d ----
FCSTD DOCUMENT  (FreeCAD 0.20R29177 +426 (Git))
Label: mid_hexagon_cmmon
License: All rights reserved
LicenseURL: http://en.wikipedia.org/wiki/All_rights_reserved
objects: Sketcher::SketchObject×5, PartDesign::Pocket×2, PartDesign::Hole×2, PartDesign::CoordinateSystem×2, PartDesign::Pad×1, PartDesign::Body×1
note: 18 computed .brp shape members not serialized (recipe doc carries the construction recipe); baked Part::Feature solids carry a one-line shape summary decoded from their .brp

FEATURE [Sketcher::SketchObject] Sketch007
  FullyConstrained = true
  MapMode = 5
  sketch-geometry (7):
    g0: LineSegment StartX=86.6025 StartY=50 StartZ=0 EndX=-1.42e-14 EndY=100 EndZ=0
    g1: LineSegment StartX=-1.42e-14 StartY=100 StartZ=0 EndX=-86.6025 EndY=50 EndZ=0
    g2: LineSegment StartX=-86.6025 StartY=50 StartZ=0 EndX=-86.6025 EndY=-50 EndZ=0
    g3: LineSegment StartX=-86.6025 StartY=-50 StartZ=0 EndX=0 EndY=-100 EndZ=0
    g4: LineSegment StartX=0 StartY=-100 StartZ=0 EndX=86.6025 EndY=-50 EndZ=0
    g5: LineSegment StartX=86.6025 StartY=-50 StartZ=0 EndX=86.6025 EndY=50 EndZ=0
    g6: Circle CenterX=0 CenterY=0 CenterZ=0 NormalX=0 NormalY=0 NormalZ=1 AngleXU=0 Radius=100
  constraints (16):
    c: Coincident(g0,g1)
    c: Coincident(g1,g2)
    c: Coincident(g2,g3)
    c: Coincident(g3,g4)
    c: Coincident(g4,g5)
    c: Coincident(g5,g0)
    c: Equal(g0, g1-g5) x5
    c: PointOnObject(g0,g6)
    c: PointOnObject(g1,g6)
    c: PointOnObject(g2,g6)
    c: PointOnObject(g3,g6)
    c: PointOnObject(g4,g6)
    c: PointOnObject(g5,g6)
    c: Coincident(g6,g-1)
    c: PointOnObject(g3,g-2)
    c: DistanceY(g5,g5) = 100
FEATURE [PartDesign::Pad] Pad002
  Direction = (0,0,1)
  Length = 10
  Length2 = 10
  Profile = -> Sketch007
  ReferenceAxis = -> Sketch007 [N_Axis]
  Refine = true
  Type = 0
FEATURE [Sketcher::SketchObject] Sketch008  label="lock001"
  FullyConstrained = true
  MapMode = 5
  Placement = pos=(0,0,10) rot=(0,0,1;0rad)
  sketch-geometry (1):
    g0: Circle CenterX=0 CenterY=0 CenterZ=0 NormalX=0 NormalY=0 NormalZ=1 AngleXU=0 Radius=15
  constraints (2):
    c: Coincident(g0,g-1)
    c: Diameter(g0) = 30
FEATURE [Sketcher::SketchObject] Sketch009  label="press-fit"
  FullyConstrained = true
  MapMode = 5
  Placement = pos=(0,0,0) rot=(1,0,0;3.14159rad)
  sketch-geometry (1):
    g0: Circle CenterX=0 CenterY=0 CenterZ=0 NormalX=0 NormalY=0 NormalZ=1 AngleXU=0 Radius=15.975
  constraints (2):
    c: Coincident(g0,g-1)
    c: Diameter(g0) = 31.95
FEATURE [PartDesign::Pocket] Pocket007
  BaseFeature = -> Pad002
  Direction = (0,0,1)
  Length = 5
  Length2 = 5
  Profile = -> Sketch009
  ReferenceAxis = -> Sketch009 [N_Axis]
  Refine = true
  Type = 0
FEATURE [PartDesign::Pocket] Pocket008
  BaseFeature = -> Pocket007
  Direction = (0,0,-1)
  Length = 5
  Length2 = 5
  Profile = -> Sketch008
  ReferenceAxis = -> Sketch008 [N_Axis]
  Refine = true
  Type = 0
FEATURE [Sketcher::SketchObject] Sketch024
  FullyConstrained = true
  MapMode = 5
  Placement = pos=(0,0,10) rot=(0,0,1;0rad)
  sketch-geometry (7):
    g0: LineSegment StartX=35 StartY=-20.2073 StartZ=0 EndX=0 EndY=40.4145 EndZ=0
    g1: LineSegment StartX=0 StartY=40.4145 StartZ=0 EndX=-35 EndY=-20.2073 EndZ=0
    g2: LineSegment StartX=-35 StartY=-20.2073 StartZ=0 EndX=35 EndY=-20.2073 EndZ=0
    g3: Circle CenterX=0 CenterY=0 CenterZ=0 NormalX=0 NormalY=0 NormalZ=1 AngleXU=0 Radius=40.4145
    g4: Circle CenterX=35 CenterY=-20.2073 CenterZ=0 NormalX=0 NormalY=0 NormalZ=1 AngleXU=0 Radius=3
    g5: Circle CenterX=0 CenterY=40.4145 CenterZ=0 NormalX=0 NormalY=0 NormalZ=1 AngleXU=0 Radius=3
    g6: Circle CenterX=-35 CenterY=-20.2073 CenterZ=0 NormalX=0 NormalY=0 NormalZ=1 AngleXU=0 Radius=3
  constraints (17):
    c: Coincident(g0,g1)
    c: Coincident(g1,g2)
    c: Coincident(g2,g0)
    c: Equal(g0,g1)
    c: Equal(g0,g2)
    c: PointOnObject(g0,g3)
    c: PointOnObject(g1,g3)
    c: PointOnObject(g2,g3)
    c: Coincident(g3,g-1)
    c: PointOnObject(g0,g-2)
    c: DistanceX(g2,g2) = 70
    c: Coincident(g4,g0)
    c: Diameter(g4) = 6
    c: Coincident(g5,g0)
    c: Coincident(g6,g1)
    c: Equal(g6,g5)
    c: Equal(g5,g4)
FEATURE [PartDesign::Hole] Hole004
  BaseFeature = -> Pocket008
  CustomThreadClearance = 0
  Depth = 534.823
  DepthType = 1
  Diameter = 2.5
  DrillForDepth = true
  DrillPoint = 1
  DrillPointAngle = 118
  HoleCutCountersinkAngle = 90
  HoleCutCustomValues = false
  HoleCutDepth = 0
  HoleCutDiameter = 6.1
  HoleCutType = 0
  ModelThread = false
  Profile = -> Sketch024
  Refine = true
  Tapered = false
  TaperedAngle = 90
  ThreadClass = 0
  ThreadDepth = 534.823
  ThreadDepthType = 0
  ThreadDirection = 0
  ThreadFit = 0
  ThreadSize = 9
  ThreadType = 1
  Threaded = true
  UseCustomThreadClearance = false
FEATURE [Sketcher::SketchObject] Sketch066
  FullyConstrained = true
  MapMode = 5
  Placement = pos=(0,0,0) rot=(1,0,0;3.14159rad)
  Support = -> [Hole004]
  sketch-geometry (7):
    g0: LineSegment StartX=35 StartY=-20.2073 StartZ=0 EndX=0 EndY=40.4145 EndZ=0
    g1: LineSegment StartX=0 StartY=40.4145 StartZ=0 EndX=-35 EndY=-20.2073 EndZ=0
    g2: LineSegment StartX=-35 StartY=-20.2073 StartZ=0 EndX=35 EndY=-20.2073 EndZ=0
    g3: Circle CenterX=0 CenterY=0 CenterZ=0 NormalX=0 NormalY=0 NormalZ=1 AngleXU=0 Radius=40.4145
    g4: Circle CenterX=35 CenterY=-20.2073 CenterZ=0 NormalX=0 NormalY=0 NormalZ=1 AngleXU=0 Radius=3
    g5: Circle CenterX=0 CenterY=40.4145 CenterZ=0 NormalX=0 NormalY=0 NormalZ=1 AngleXU=0 Radius=3
    g6: Circle CenterX=-35 CenterY=-20.2073 CenterZ=0 NormalX=0 NormalY=0 NormalZ=1 AngleXU=0 Radius=3
  constraints (17):
    c: Coincident(g0,g1)
    c: Coincident(g1,g2)
    c: Coincident(g2,g0)
    c: Equal(g0,g1)
    c: Equal(g0,g2)
    c: PointOnObject(g0,g3)
    c: PointOnObject(g1,g3)
    c: PointOnObject(g2,g3)
    c: Coincident(g3,g-1)
    c: PointOnObject(g0,g-2)
    c: DistanceX(g2,g2) = 70
    c: Coincident(g4,g0)
    c: Coincident(g5,g0)
    c: Coincident(g6,g1)
    c: Equal(g6,g4)
    c: Equal(g4,g5)
    c: Diameter(g5) = 6
FEATURE [PartDesign::Hole] Hole005
  BaseFeature = -> Hole004
  CustomThreadClearance = 0
  Depth = 7
  DepthType = 0
  Diameter = 2.5
  DrillForDepth = true
  DrillPoint = 1
  DrillPointAngle = 118
  HoleCutCountersinkAngle = 90
  HoleCutCustomValues = false
  HoleCutDepth = 0
  HoleCutDiameter = 6.1
  HoleCutType = 0
  ModelThread = false
  Profile = -> Sketch066
  Refine = true
  Tapered = false
  TaperedAngle = 90
  ThreadClass = 0
  ThreadDepth = 7
  ThreadDepthType = 0
  ThreadDirection = 0
  ThreadFit = 0
  ThreadSize = 9
  ThreadType = 1
  Threaded = true
  UseCustomThreadClearance = false
FEATURE [PartDesign::CoordinateSystem] LCS_1
  AttacherType = Attacher::AttachEngine3D
  AttachmentOffset = pos=(0,0,0) rot=(1,0,0;1.5708rad)
  MapMode = 12
  Placement = pos=(0,0,5) rot=(1,0,0;3.14159rad)
  Support = -> [Hole005]
FEATURE [PartDesign::CoordinateSystem] LCS_bottom
  AttacherType = Attacher::AttachEngine3D
  AttachmentOffset = pos=(0,0,0) rot=(1,0,0;3.14159rad)
  MapMode = 45
  Placement = pos=(7.01e-14,-5e-16,10) rot=(1,0,0;3.14159rad)
  Support = -> [Hole005]
FEATURE [PartDesign::Body] Body002  label="mid_hexagon"
  Group = -> [Sketch007,Pad002,Sketch008,Sketch009,Pocket007,Pocket008,Sketch024,Hole004,Sketch066,Hole005,LCS_1,LCS_bottom]
  Origin = -> Origin002
  Placement = pos=(3.1,54.8,93.3) rot=(1,0,0;3.14159rad)
  Tip = -> Hole005
---- part mid_hexagon_cmmon_w_side_holes.FCStd = doc fcstd_2f4bcb8ad681 ----
FCSTD DOCUMENT  (FreeCAD 0.20R29177 +426 (Git))
Label: mid_hexagon_cmmon_w_side_holes
License: All rights reserved
LicenseURL: http://en.wikipedia.org/wiki/All_rights_reserved
objects: PartDesign::CoordinateSystem×10, Sketcher::SketchObject×7, PartDesign::Hole×4, PartDesign::Pocket×2, PartDesign::Pad×1, PartDesign::Body×1
note: 32 computed .brp shape members not serialized (recipe doc carries the construction recipe); baked Part::Feature solids carry a one-line shape summary decoded from their .brp

FEATURE [Sketcher::SketchObject] Sketch092
  FullyConstrained = true
  MapMode = 5
  sketch-geometry (7):
    g0: LineSegment StartX=86.6025 StartY=50 StartZ=0 EndX=-1.42e-14 EndY=100 EndZ=0
    g1: LineSegment StartX=-1.42e-14 StartY=100 StartZ=0 EndX=-86.6025 EndY=50 EndZ=0
    g2: LineSegment StartX=-86.6025 StartY=50 StartZ=0 EndX=-86.6025 EndY=-50 EndZ=0
    g3: LineSegment StartX=-86.6025 StartY=-50 StartZ=0 EndX=0 EndY=-100 EndZ=0
    g4: LineSegment StartX=0 StartY=-100 StartZ=0 EndX=86.6025 EndY=-50 EndZ=0
    g5: LineSegment StartX=86.6025 StartY=-50 StartZ=0 EndX=86.6025 EndY=50 EndZ=0
    g6: Circle CenterX=0 CenterY=0 CenterZ=0 NormalX=0 NormalY=0 NormalZ=1 AngleXU=0 Radius=100
  constraints (16):
    c: Coincident(g0,g1)
    c: Coincident(g1,g2)
    c: Coincident(g2,g3)
    c: Coincident(g3,g4)
    c: Coincident(g4,g5)
    c: Coincident(g5,g0)
    c: Equal(g0, g1-g5) x5
    c: PointOnObject(g0,g6)
    c: PointOnObject(g1,g6)
    c: PointOnObject(g2,g6)
    c: PointOnObject(g3,g6)
    c: PointOnObject(g4,g6)
    c: PointOnObject(g5,g6)
    c: Coincident(g6,g-1)
    c: PointOnObject(g3,g-2)
    c: DistanceY(g5,g5) = 100
FEATURE [PartDesign::Pad] Pad041
  Direction = (0,0,1)
  Length = 10
  Length2 = 10
  Profile = -> Sketch092
  ReferenceAxis = -> Sketch092 [N_Axis]
  Refine = true
  Type = 0
FEATURE [Sketcher::SketchObject] Sketch093  label="lock003"
  FullyConstrained = true
  MapMode = 5
  Placement = pos=(0,0,10) rot=(0,0,1;0rad)
  sketch-geometry (1):
    g0: Circle CenterX=0 CenterY=0 CenterZ=0 NormalX=0 NormalY=0 NormalZ=1 AngleXU=0 Radius=15
  constraints (2):
    c: Coincident(g0,g-1)
    c: Diameter(g0) = 30
FEATURE [Sketcher::SketchObject] Sketch094  label="press_fit002"
  FullyConstrained = true
  MapMode = 5
  Placement = pos=(0,0,0) rot=(1,0,0;3.14159rad)
  sketch-geometry (1):
    g0: Circle CenterX=0 CenterY=0 CenterZ=0 NormalX=0 NormalY=0 NormalZ=1 AngleXU=0 Radius=15.975
  constraints (2):
    c: Coincident(g0,g-1)
    c: Diameter(g0) = 31.95
FEATURE [PartDesign::Pocket] Pocket017
  BaseFeature = -> Pad041
  Direction = (0,0,1)
  Length = 5
  Length2 = 5
  Profile = -> Sketch094
  ReferenceAxis = -> Sketch094 [N_Axis]
  Refine = true
  Type = 0
FEATURE [PartDesign::Pocket] Pocket018
  BaseFeature = -> Pocket017
  Direction = (0,0,-1)
  Length = 5
  Length2 = 5
  Profile = -> Sketch093
  ReferenceAxis = -> Sketch093 [N_Axis]
  Refine = true
  Type = 0
FEATURE [Sketcher::SketchObject] Sketch095
  FullyConstrained = true
  MapMode = 5
  Placement = pos=(0,0,10) rot=(0,0,1;0rad)
  Support = -> [Pocket018]
  sketch-geometry (7):
    g0: LineSegment StartX=35 StartY=-20.2073 StartZ=0 EndX=0 EndY=40.4145 EndZ=0
    g1: LineSegment StartX=0 StartY=40.4145 StartZ=0 EndX=-35 EndY=-20.2073 EndZ=0
    g2: LineSegment StartX=-35 StartY=-20.2073 StartZ=0 EndX=35 EndY=-20.2073 EndZ=0
    g3: Circle CenterX=0 CenterY=0 CenterZ=0 NormalX=0 NormalY=0 NormalZ=1 AngleXU=0 Radius=40.4145
    g4: Circle CenterX=0 CenterY=40.4145 CenterZ=0 NormalX=0 NormalY=0 NormalZ=1 AngleXU=0 Radius=3
    g5: Circle CenterX=35 CenterY=-20.2073 CenterZ=0 NormalX=0 NormalY=0 NormalZ=1 AngleXU=0 Radius=3
    g6: Circle CenterX=-35 CenterY=-20.2073 CenterZ=0 NormalX=0 NormalY=0 NormalZ=1 AngleXU=0 Radius=3
  constraints (17):
    c: Coincident(g0,g1)
    c: Coincident(g1,g2)
    c: Coincident(g2,g0)
    c: Equal(g0,g1)
    c: Equal(g0,g2)
    c: PointOnObject(g0,g3)
    c: PointOnObject(g1,g3)
    c: PointOnObject(g2,g3)
    c: Coincident(g3,g-1)
    c: PointOnObject(g0,g-2)
    c: DistanceX(g2,g2) = 70
    c: Coincident(g4,g0)
    c: Coincident(g5,g0)
    c: Coincident(g6,g1)
    c: Equal(g4,g6)
    c: Equal(g6,g5)
    c: Diameter(g4) = 6
FEATURE [PartDesign::Hole] Hole016
  BaseFeature = -> Pocket018
  CustomThreadClearance = 0
  Depth = 25
  DepthType = 0
  Diameter = 2.5
  DrillForDepth = false
  DrillPoint = 1
  DrillPointAngle = 118
  HoleCutCountersinkAngle = 90
  HoleCutCustomValues = false
  HoleCutDepth = 0
  HoleCutDiameter = 6.1
  HoleCutType = 2
  ModelThread = false
  Profile = -> Sketch095
  Refine = true
  Tapered = false
  TaperedAngle = 90
  ThreadClass = 0
  ThreadDepth = 25
  ThreadDepthType = 0
  ThreadDirection = 0
  ThreadFit = 0
  ThreadSize = 9
  ThreadType = 1
  Threaded = true
  UseCustomThreadClearance = false
FEATURE [Sketcher::SketchObject] Sketch096
  FullyConstrained = true
  MapMode = 5
  Placement = pos=(86.6025,-5.664e-13,0) rot=(0.57735,0.57735,0.57735;2.0944rad)
  Support = -> [Hole016]
  sketch-geometry (1):
    g0: Circle CenterX=0 CenterY=5 CenterZ=0 NormalX=0 NormalY=0 NormalZ=1 AngleXU=0 Radius=3
  constraints (3):
    c: PointOnObject(g0,g-2)
    c: Diameter(g0) = 6
    c: DistanceY(g-1,g0) = 5
FEATURE [PartDesign::Hole] Hole017
  BaseFeature = -> Hole016
  CustomThreadClearance = 0
  Depth = 15
  DepthType = 0
  Diameter = 2.5
  DrillForDepth = true
  DrillPoint = 1
  DrillPointAngle = 118
  HoleCutCountersinkAngle = 90
  HoleCutCustomValues = false
  HoleCutDepth = 0
  HoleCutDiameter = 6.1
  HoleCutType = 0
  ModelThread = false
  Profile = -> Sketch096
  Refine = true
  Tapered = false
  TaperedAngle = 90
  ThreadClass = 0
  ThreadDepth = 15
  ThreadDepthType = 0
  ThreadDirection = 0
  ThreadFit = 0
  ThreadSize = 9
  ThreadType = 1
  Threaded = true
  UseCustomThreadClearance = false
FEATURE [Sketcher::SketchObject] Sketch097
  FullyConstrained = true
  MapMode = 5
  Placement = pos=(-43.3013,75,0) rot=(-0.186157,0.694747,0.694747;3.50969rad)
  Support = -> [Hole017]
  sketch-geometry (1):
    g0: Circle CenterX=0 CenterY=5 CenterZ=0 NormalX=0 NormalY=0 NormalZ=1 AngleXU=0 Radius=3
  constraints (3):
    c: PointOnObject(g0,g-2)
    c: Diameter(g0) = 6
    c: DistanceY(g-1,g0) = 5
FEATURE [PartDesign::Hole] Hole018
  BaseFeature = -> Hole017
  CustomThreadClearance = 0
  Depth = 15
  DepthType = 0
  Diameter = 2.5
  DrillForDepth = true
  DrillPoint = 1
  DrillPointAngle = 118
  HoleCutCountersinkAngle = 90
  HoleCutCustomValues = false
  HoleCutDepth = 0
  HoleCutDiameter = 6.1
  HoleCutType = 0
  ModelThread = false
  Profile = -> Sketch097
  Refine = true
  Tapered = false
  TaperedAngle = 90
  ThreadClass = 0
  ThreadDepth = 15
  ThreadDepthType = 0
  ThreadDirection = 0
  ThreadFit = 0
  ThreadSize = 9
  ThreadType = 1
  Threaded = true
  UseCustomThreadClearance = false
FEATURE [Sketcher::SketchObject] Sketch
  FullyConstrained = true
  MapMode = 5
  Placement = pos=(-43.3013,-75,0) rot=(0.935113,-0.250563,-0.250563;1.63783rad)
  Support = -> [Hole018]
  sketch-geometry (1):
    g0: Circle CenterX=0 CenterY=5 CenterZ=0 NormalX=0 NormalY=0 NormalZ=1 AngleXU=0 Radius=3
  constraints (3):
    c: PointOnObject(g0,g-2)
    c: Diameter(g0) = 6
    c: DistanceY(g-1,g0) = 5
FEATURE [PartDesign::Hole] Hole
  BaseFeature = -> Hole018
  CustomThreadClearance = 0
  Depth = 15
  DepthType = 0
  Diameter = 2.5
  DrillForDepth = true
  DrillPoint = 1
  DrillPointAngle = 118
  HoleCutCountersinkAngle = 90
  HoleCutCustomValues = false
  HoleCutDepth = 0
  HoleCutDiameter = 6.1
  HoleCutType = 0
  ModelThread = false
  Profile = -> Sketch
  Tapered = false
  TaperedAngle = 90
  ThreadClass = 0
  ThreadDepth = 15
  ThreadDepthType = 0
  ThreadDirection = 0
  ThreadFit = 0
  ThreadSize = 9
  ThreadType = 1
  Threaded = true
  UseCustomThreadClearance = false
FEATURE [PartDesign::CoordinateSystem] LCS_1
  AttacherType = Attacher::AttachEngine3D
  MapMode = 12
  Placement = pos=(0,0,5) rot=(1,0,0;1.5708rad)
  Support = -> [Hole]
FEATURE [PartDesign::CoordinateSystem] LCS_Side1  label="LCS_Side001"
  AttacherType = Attacher::AttachEngine3D
  AttachmentOffset = pos=(0,0,0) rot=(-0.707107,-0.707107,0;3.14159rad)
  MapMode = 45
  Placement = pos=(-43.3013,-75,5) rot=(0.935113,-0.250563,-0.250563;1.63783rad)
  Support = -> [Hole]
FEATURE [PartDesign::CoordinateSystem] LCS_Side002
  AttacherType = Attacher::AttachEngine3D
  AttachmentOffset = pos=(0,0,0) rot=(-0.707107,-0.707107,0;3.14159rad)
  MapMode = 45
  Placement = pos=(43.3013,-75,5) rot=(-0.935113,-0.250563,-0.250563;4.64535rad)
  Support = -> [Hole]
FEATURE [PartDesign::CoordinateSystem] LCS_Side003
  AttacherType = Attacher::AttachEngine3D
  AttachmentOffset = pos=(0,0,0) rot=(0.707107,0.707107,0;3.14159rad)
  MapMode = 45
  Placement = pos=(-86.6025,-2.7e-15,5) rot=(-0.57735,0.57735,0.57735;4.18879rad)
  Support = -> [Hole]
FEATURE [PartDesign::CoordinateSystem] LCS_Side004
  AttacherType = Attacher::AttachEngine3D
  AttachmentOffset = pos=(0,0,0) rot=(0,0,-1;1.5708rad)
  MapMode = 45
  Placement = pos=(-43.3013,75,5) rot=(0.186157,-0.694747,-0.694747;2.77349rad)
  Support = -> [Hole]
FEATURE [PartDesign::CoordinateSystem] LCS_Side005
  AttacherType = Attacher::AttachEngine3D
  AttachmentOffset = pos=(0,0,0) rot=(0,0,-1;1.5708rad)
  MapMode = 45
  Placement = pos=(43.3013,75,5) rot=(0.186157,0.694747,0.694747;2.77349rad)
  Support = -> [Hole]
FEATURE [PartDesign::CoordinateSystem] LCS_Side006
  AttacherType = Attacher::AttachEngine3D
  AttachmentOffset = pos=(0,0,0) rot=(0,0,-1;1.5708rad)
  MapMode = 45
  Placement = pos=(86.6025,-1.6699e-12,5) rot=(0.57735,0.57735,0.57735;2.0944rad)
  Support = -> [Hole]
FEATURE [PartDesign::CoordinateSystem] LCS_2
  AttacherType = Attacher::AttachEngine3D
  AttachmentOffset = pos=(0,0,5) rot=(0,0,1;0rad)
  MapMode = 45
  Placement = pos=(86.6025,-50,10) rot=(0,0,1;0rad)
  Support = -> [Hole]
FEATURE [PartDesign::CoordinateSystem] LCS_3
  AttacherType = Attacher::AttachEngine3D
  AttachmentOffset = pos=(0,0,5) rot=(0,0,1;2.0944rad)
  MapMode = 45
  Placement = pos=(-1.42e-14,100,10) rot=(0,0,1;2.0944rad)
  Support = -> [Hole]
FEATURE [PartDesign::CoordinateSystem] LCS_4
  AttacherType = Attacher::AttachEngine3D
  AttachmentOffset = pos=(0,0,5) rot=(0,0,-1;2.0944rad)
  MapMode = 45
  Placement = pos=(-86.6025,-50,10) rot=(0,0,-1;2.0944rad)
  Support = -> [Hole]
FEATURE [PartDesign::Body] Body019  label="mid_hexagon_w_holes"
  Group = -> [Sketch092,Pad041,Sketch093,Sketch094,Pocket017,Pocket018,Sketch095,Hole016,Sketch096,Hole017,Sketch097,Hole018,Sketch,Hole,LCS_1,LCS_Side1,LCS_Side002,LCS_Side003,LCS_Side004,LCS_Side005,LCS_Side006,LCS_2,LCS_3,LCS_4]
  Origin = -> Origin027
  Tip = -> Hole
---- part refinedHorn.FCStd = doc fcstd_d6d8a35d817a ----
FCSTD DOCUMENT  (FreeCAD 0.20R29177 +426 (Git))
Label: refinedHorn
License: All rights reserved
LicenseURL: http://en.wikipedia.org/wiki/All_rights_reserved
objects: Part::Feature×2, PartDesign::CoordinateSystem×2, Mesh::Feature×1, Part::Refine×1, PartDesign::FeatureBase×1, Sketcher::SketchObject×1, PartDesign::Body×1
note: 8 computed .brp shape members not serialized (recipe doc carries the construction recipe); baked Part::Feature solids carry a one-line shape summary decoded from their .brp

FEATURE [Mesh::Feature] _0mm_servoHorn  label="20mm-servoHorn"
FEATURE [Part::Feature] _0mm_servoHorn001
  shape: bbox 20 x 6.479 x 6.445 mm, 2350 faces, 0 solids (baked)
FEATURE [Part::Refine] _0mm_servoHorn001001
  Source = -> _0mm_servoHorn001
FEATURE [Part::Feature] _0mm_servoHorn001001_solid  label="_0mm_servoHorn001001 (Solid)"
  shape: bbox 20 x 6.479 x 6.445 mm, 888 faces (baked)
FEATURE [PartDesign::FeatureBase] BaseFeature
  BaseFeature = -> _0mm_servoHorn001001_solid
FEATURE [PartDesign::CoordinateSystem] LCS_1
  AttacherType = Attacher::AttachEngine3D
  AttachmentOffset = pos=(0,0,0) rot=(0.382683,0.92388,0;3.14159rad)
  MapMode = 45
  Placement = pos=(-80.5131,-325.745,1.691) rot=(-0.686181,0.727431,0;3.14159rad)
  Support = -> [BaseFeature]
FEATURE [Sketcher::SketchObject] Sketch
  ExternalGeometry = -> [BaseFeature]
  FullyConstrained = true
  MapMode = 5
  Placement = pos=(0,0,0.002) rot=(1,0,0;3.14159rad)
  Support = -> [BaseFeature]
  sketch-geometry (5):
    g0: Circle CenterX=-95.4317 CenterY=325.96 CenterZ=0 NormalX=0 NormalY=0 NormalZ=1 AngleXU=0 Radius=1.94454
    g1: Circle CenterX=-80.6171 CenterY=325.74 CenterZ=0 NormalX=0 NormalY=0 NormalZ=1 AngleXU=0 Radius=3.24089
    g2: Circle CenterX=-95.9081 CenterY=325.959 CenterZ=0 NormalX=0 NormalY=0 NormalZ=1 AngleXU=0 Radius=0.435168
    g3: Circle CenterX=-92.3401 CenterY=325.959 CenterZ=0 NormalX=0 NormalY=0 NormalZ=1 AngleXU=0 Radius=0.435168
    g4: Circle CenterX=-88.7721 CenterY=325.959 CenterZ=0 NormalX=0 NormalY=0 NormalZ=1 AngleXU=0 Radius=0.435168
  constraints (21):
    c: PointOnObject(g-10,g0)
    c: PointOnObject(g-11,g0)
    c: PointOnObject(g-9,g0)
    c: PointOnObject(g-6,g1)
    c: PointOnObject(g-8,g1)
    c: PointOnObject(g-7,g1)
    c: Diameter(g1) = 6.48178
    c: Diameter(g0) = 3.88909
    c: DistanceX(g0,g1) = 14.8146
    c: PointOnObject(g-12,g2)
    c: PointOnObject(g-14,g2)
    c: PointOnObject(g-13,g2)
    c: PointOnObject(g-15,g3)
    c: PointOnObject(g-17,g3)
    c: PointOnObject(g-16,g3)
    c: DistanceX(g2,g3) = 3.568
    c: DistanceX(g-9,g2) = 1.46816
    c: PointOnObject(g-19,g4)
    c: PointOnObject(g-20,g4)
    c: PointOnObject(g-18,g4)
    c: DistanceX(g3,g4) = 3.568
FEATURE [PartDesign::CoordinateSystem] hexagonPlacement_LCS
  AttacherType = Attacher::AttachEngine3D
  AttachmentOffset = pos=(0,0,0) rot=(0,1,0;3.14159rad)
  MapMode = 45
  Placement = pos=(-87.3366,-325.835,0.002) rot=(-0.712245,0.701931,0;3.14159rad)
  Support = -> [BaseFeature]
FEATURE [PartDesign::Body] Body  label="HornBody"
  BaseFeature = -> _0mm_servoHorn001001_solid
  Group = -> [BaseFeature,LCS_1,Sketch,hexagonPlacement_LCS]
  Origin = -> Origin
  Tip = -> BaseFeature
---- part smallerBelt.FCStd = doc fcstd_5d0615a69983 ----
FCSTD DOCUMENT  (FreeCAD 0.20R29177 +426 (Git))
Label: smallerBelt
License: All rights reserved
LicenseURL: http://en.wikipedia.org/wiki/All_rights_reserved
objects: PartDesign::CoordinateSystem×2, Sketcher::SketchObject×1, PartDesign::Pad×1, PartDesign::Body×1
note: 6 computed .brp shape members not serialized (recipe doc carries the construction recipe); baked Part::Feature solids carry a one-line shape summary decoded from their .brp

FEATURE [Sketcher::SketchObject] Sketch
  FullyConstrained = false
  MapMode = 5
  Support = -> [XY_Plane]
  sketch-geometry (8):
    g0: ArcOfCircle CenterX=-48.7141 CenterY=0 CenterZ=0 NormalX=0 NormalY=0 NormalZ=1 AngleXU=0 Radius=20 StartAngle=1.3933 EndAngle=4.88989
    g1: ArcOfCircle CenterX=27.743 CenterY=0 CenterZ=0 NormalX=0 NormalY=0 NormalZ=1 AngleXU=0 Radius=6.5 StartAngle=4.88989 EndAngle=7.67648
    g2: LineSegment StartX=-45.1827 StartY=19.6858 StartZ=0 EndX=28.8907 EndY=6.39787 EndZ=0
    g3: LineSegment StartX=-45.1827 StartY=-19.6858 StartZ=0 EndX=28.8907 EndY=-6.39787 EndZ=0
    g4: ArcOfCircle CenterX=-48.7141 CenterY=0 CenterZ=0 NormalX=0 NormalY=0 NormalZ=1 AngleXU=0 Radius=20.5 StartAngle=1.3933 EndAngle=4.88989
    g5: ArcOfCircle CenterX=27.743 CenterY=0 CenterZ=0 NormalX=0 NormalY=0 NormalZ=1 AngleXU=0 Radius=7 StartAngle=4.88989 EndAngle=7.67648
    g6: LineSegment StartX=-45.0944 StartY=20.1779 StartZ=0 EndX=28.979 EndY=6.89002 EndZ=0
    g7: LineSegment StartX=-45.0944 StartY=-20.1779 StartZ=0 EndX=28.979 EndY=-6.89002 EndZ=0
  constraints (16):
    c: PointOnObject(g0,g-1)
    c: PointOnObject(g1,g-1)
    c: Diameter(g0) = 40
    c: Diameter(g1) = 13
    c: Tangent(g0,g3) = -1.5708
    c: Tangent(g0,g2) = 1.5708
    c: Tangent(g1,g2) = 1.5708
    c: Tangent(g1,g3) = -1.5708
    c: Diameter(g4) = 41
    c: Diameter(g5) = 14
    c: Tangent(g4,g7) = -1.5708
    c: Tangent(g4,g6) = 1.5708
    c: Tangent(g5,g6) = 1.5708
    c: Tangent(g5,g7) = -1.5708
    c: Coincident(g5,g1)
    c: Coincident(g4,g0)
FEATURE [PartDesign::Pad] Pad
  Direction = (0,0,1)
  Length = 5
  Length2 = 10
  Profile = -> Sketch
  ReferenceAxis = -> Sketch [N_Axis]
  Type = 0
FEATURE [PartDesign::CoordinateSystem] LCS_gear60
  AttacherType = Attacher::AttachEngine3D
  MapMode = 11
  Placement = pos=(-48.7141,3.6e-15,0) rot=(0,0,1;2.96409rad)
  Support = -> [Pad]
FEATURE [PartDesign::CoordinateSystem] LCS_gear20
  AttacherType = Attacher::AttachEngine3D
  MapMode = 11
  Placement = pos=(27.743,9e-16,0) rot=(0,0,1;0.1775rad)
  Support = -> [Pad]
FEATURE [PartDesign::Body] Body  label="smallerBelt_Body"
  Group = -> [Sketch,Pad,LCS_gear60,LCS_gear20]
  Origin = -> Origin
  Tip = -> Pad
---- part stepperMotorStand.FCStd = doc fcstd_30e448889c03 ----
FCSTD DOCUMENT  (FreeCAD 0.20R29177 +426 (Git))
Label: stepperMotorStand
License: All rights reserved
LicenseURL: http://en.wikipedia.org/wiki/All_rights_reserved
objects: Sketcher::SketchObject×1, PartDesign::Pad×1, PartDesign::CoordinateSystem×1, PartDesign::Body×1
note: 5 computed .brp shape members not serialized (recipe doc carries the construction recipe); baked Part::Feature solids carry a one-line shape summary decoded from their .brp

FEATURE [Sketcher::SketchObject] Sketch
  FullyConstrained = false
  MapMode = 5
  Support = -> [XY_Plane]
  sketch-geometry (16):
    g0: LineSegment StartX=-84.2002 StartY=48.613 StartZ=0 EndX=-84.2002 EndY=-48.613 EndZ=0
    g1: LineSegment StartX=-84.2002 StartY=-48.613 StartZ=0 EndX=0 EndY=-97.226 EndZ=0
    g2: LineSegment StartX=0 StartY=-97.226 StartZ=0 EndX=84.2002 EndY=-48.613 EndZ=0
    g3: LineSegment StartX=84.2002 StartY=-48.613 StartZ=0 EndX=84.2002 EndY=48.613 EndZ=0
    g4: LineSegment StartX=84.2002 StartY=48.613 StartZ=0 EndX=0 EndY=97.226 EndZ=0
    g5: LineSegment StartX=-6e-16 StartY=97.226 StartZ=0 EndX=-84.2002 EndY=48.613 EndZ=0
    g6: Circle CenterX=0 CenterY=0 CenterZ=0 NormalX=0 NormalY=0 NormalZ=1 AngleXU=0 Radius=97.226
    g7: LineSegment StartX=-33.6434 StartY=19.424 StartZ=0 EndX=-33.6434 EndY=-19.424 EndZ=0
    g8: LineSegment StartX=-33.6434 StartY=-19.424 StartZ=0 EndX=0 EndY=-38.848 EndZ=0
    g9: LineSegment StartX=0 StartY=-38.848 StartZ=0 EndX=33.6434 EndY=-19.424 EndZ=0
    g10: LineSegment StartX=33.6434 StartY=-19.424 StartZ=0 EndX=33.6434 EndY=19.424 EndZ=0
    g11: LineSegment StartX=33.6434 StartY=19.424 StartZ=0 EndX=7.1e-15 EndY=38.848 EndZ=0
    g12: LineSegment StartX=3.8e-15 StartY=38.848 StartZ=0 EndX=-33.6434 EndY=19.424 EndZ=0
    g13: Circle CenterX=0 CenterY=0 CenterZ=0 NormalX=0 NormalY=0 NormalZ=1 AngleXU=0 Radius=38.848
    g14: LineSegment StartX=33.6434 StartY=-19.424 StartZ=0 EndX=84.2002 EndY=-48.613 EndZ=0
    g15: LineSegment StartX=-84.2002 StartY=48.613 StartZ=0 EndX=-33.6434 EndY=19.424 EndZ=0
  constraints (34):
    c: Coincident(g0,g1)
    c: Coincident(g1,g2)
    c: Coincident(g2,g3)
    c: Coincident(g3,g4)
    c: Coincident(g4,g5)
    c: Coincident(g5,g0)
    c: Equal(g0, g1-g5) x5
    c: PointOnObject(g0,g6)
    c: PointOnObject(g1,g6)
    c: PointOnObject(g2,g6)
    c: PointOnObject(g3,g6)
    c: PointOnObject(g4,g6)
    c: PointOnObject(g5,g6)
    c: Coincident(g6,g-1)
    c: Vertical(g0)
    c: Coincident(g7,g8)
    c: Coincident(g8,g9)
    c: Coincident(g9,g10)
    c: Coincident(g10,g11)
    c: Coincident(g11,g12)
    c: Coincident(g12,g7)
    c: Equal(g7, g8-g12) x5
    c: PointOnObject(g7,g13)
    c: PointOnObject(g8,g13)
    c: PointOnObject(g9,g13)
    c: PointOnObject(g10,g13)
    c: PointOnObject(g11,g13)
    c: PointOnObject(g12,g13)
    c: Vertical(g7)
    c: Coincident(g13,g6)
    c: Coincident(g14,g10)
    c: Coincident(g14,g3)
    c: Coincident(g15,g5)
    c: Coincident(g15,g12)
FEATURE [PartDesign::Pad] Pad
  Direction = (0,0,1)
  Length = 46.3
  Length2 = 10
  Profile = -> Sketch
  ReferenceAxis = -> Sketch [N_Axis]
  Type = 0
FEATURE [PartDesign::CoordinateSystem] LCS_forStepper
  AttacherType = Attacher::AttachEngine3D
  AttachmentOffset = pos=(20,0,0) rot=(0,0,1;0rad)
  MapMode = 45
  Placement = pos=(30.8456,53.4261,46.3) rot=(0,0,1;1.0472rad)
  Support = -> [Pad]
FEATURE [PartDesign::Body] Body  label="stand_Body"
  Group = -> [Sketch,Pad,LCS_forStepper]
  Origin = -> Origin
  Tip = -> Pad
